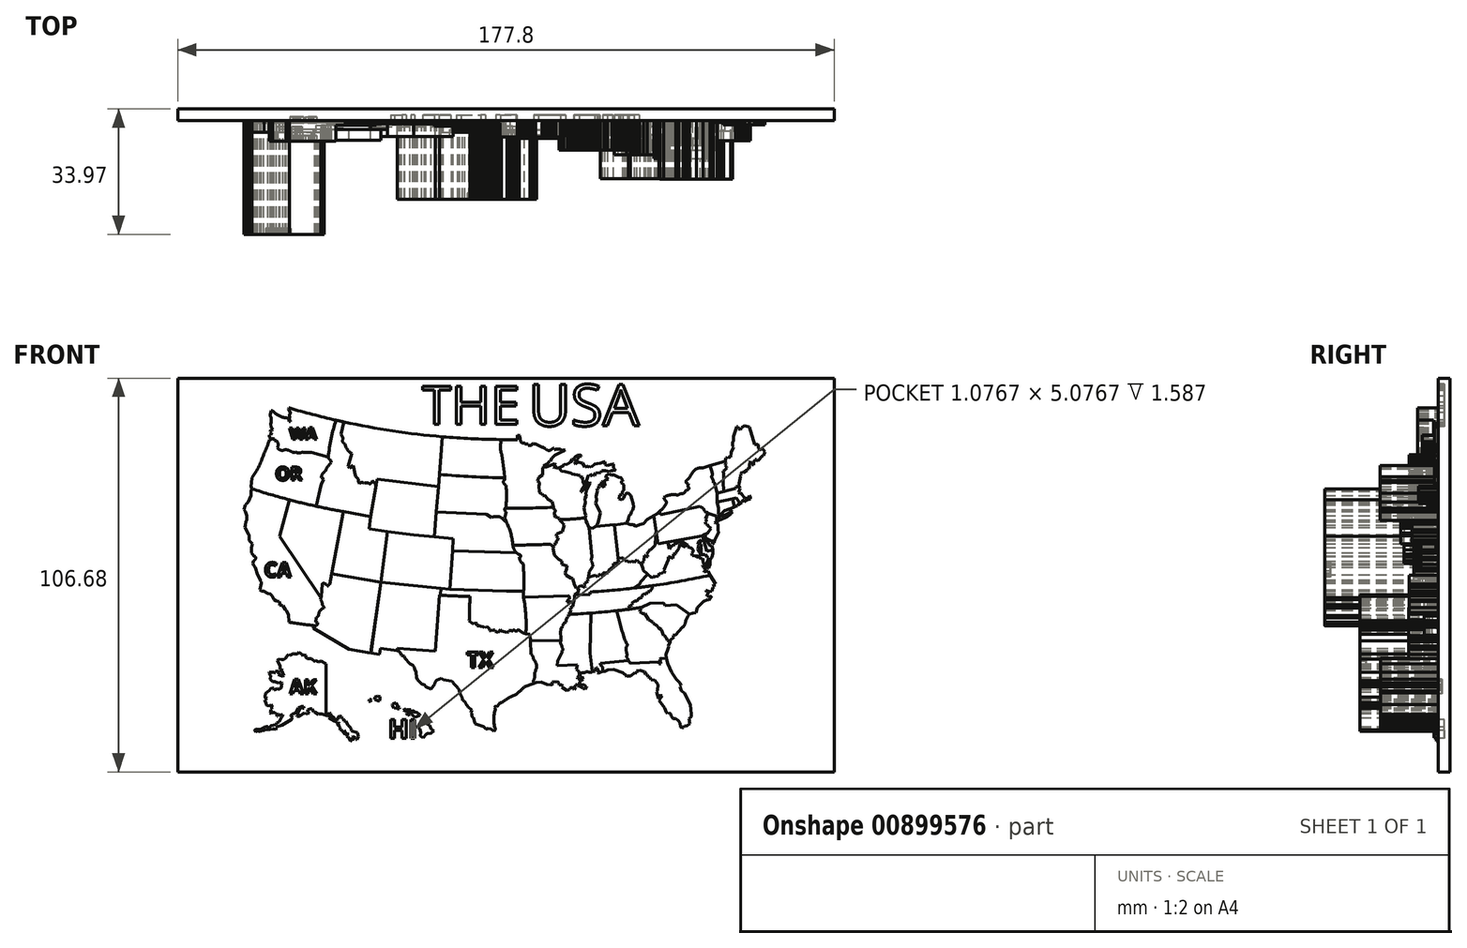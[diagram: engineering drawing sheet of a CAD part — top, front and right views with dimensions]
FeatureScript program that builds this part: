
annotation { "Feature Type Name" : "Feature", "Feature Type Description" : "" }
export const myFeature = defineFeature(function(context is Context, id is Id, definition is map)
    precondition{}
    {
        {
            var Q0;
            Q0=qCreatedBy(makeId("Front.planeOp"),FACE);
            var sketch = newSketch(context, id + "F0", { "sketchPlane" : qUnion([Q0])});
            skLineSegment(sketch, "E0.bottom", {"start": v(-88.8, 56.27) * mm, "end": v(89, 56.27) * mm});
            skLineSegment(sketch, "E0.top", {"start": v(-88.8, -50.4) * mm, "end": v(89, -50.4) * mm});
            skLineSegment(sketch, "E0.left", {"start": v(-88.8, 56.27) * mm, "end": v(-88.8, -50.4) * mm});
            skLineSegment(sketch, "E0.right", {"start": v(89, 56.27) * mm, "end": v(89, -50.4) * mm});
            skSolve(sketch);
        }
        {
            var Q0;
            Q0=qSketchRegion(id+"F0",true);
            extrude(context, id + "F1", {"entities" : qUnion([Q0]), "depth" : 3.17 * mm, "offsetDistance" : 25.4 * mm});
        }
        {
            var Q0;
            Q0=makeQuery(id+"F1.opExtrude","CAP_FACE",FACE,{"disambiguationData":[OSD([sQuery(id+"F0.wireOp",EDGE,"E0.bottom"),sQuery(id+"F0.wireOp",EDGE,"E0.top"),sQuery(id+"F0.wireOp",EDGE,"E0.left"),sQuery(id+"F0.wireOp",EDGE,"E0.right")])],"isStart":false});
            var sketch = newSketch(context, id + "F2", { "sketchPlane" : qUnion([Q0])});
            skLineSegment(sketch, "E1", {"start": v(-9.1, -34.54) * mm, "end": v(-9.38, -34.36) * mm});
            skLineSegment(sketch, "E2", {"start": v(-9.38, -34.36) * mm, "end": v(-9.15, -33.69) * mm});
            skLineSegment(sketch, "E3", {"start": v(-9.48, -33.25) * mm, "end": v(-9.15, -33.69) * mm});
            skLineSegment(sketch, "E4", {"start": v(-9.48, -33.25) * mm, "end": v(-9.93, -33.05) * mm});
            skArc(sketch, "E5", {"start": v(-11.02, -31.35) * mm, "mid": v(-10.52, -32.23) * mm, "end": v(-9.93, -33.05) * mm});
            skArc(sketch, "E6", {"start": v(-11.62, -30.95) * mm, "mid": v(-11.32, -31.15) * mm, "end": v(-11.02, -31.35) * mm});
            skArc(sketch, "E7", {"start": v(-11.62, -30.6) * mm, "mid": v(-11.62, -30.77) * mm, "end": v(-11.62, -30.95) * mm});
            skArc(sketch, "E8", {"start": v(-12.45, -28.74) * mm, "mid": v(-12.06, -29.68) * mm, "end": v(-11.62, -30.6) * mm});
            skArc(sketch, "E9", {"start": v(-12.57, -28.08) * mm, "mid": v(-12.72, -27.93) * mm, "end": v(-12.88, -27.8) * mm});
            skArc(sketch, "E10", {"start": v(-12.57, -28.08) * mm, "mid": v(-12.52, -28.41) * mm, "end": v(-12.45, -28.74) * mm});
            skLineSegment(sketch, "E11", {"start": v(-32.02, 14.71) * mm, "end": v(-33.75, 1.04) * mm});
            skLineSegment(sketch, "E12", {"start": v(-14.18, 12.88) * mm, "end": v(-14.4, 9.48) * mm});
            skLineSegment(sketch, "E13", {"start": v(-43.9, 20.13) * mm, "end": v(-36.59, 18.84) * mm});
            skLineSegment(sketch, "E14", {"start": v(-36.59, 18.84) * mm, "end": v(-36.99, 15.45) * mm});
            skLineSegment(sketch, "E15", {"start": v(-36.99, 15.45) * mm, "end": v(-32.02, 14.71) * mm});
            skLineSegment(sketch, "E16", {"start": v(-47.13, 3.28) * mm, "end": v(-43.9, 20.13) * mm});
            skArc(sketch, "E17", {"start": v(-68.66, 26.3) * mm, "mid": v(-56.39, 22.78) * mm, "end": v(-43.9, 20.13) * mm});
            skLineSegment(sketch, "E18", {"start": v(-61.22, 13.45) * mm, "end": v(-58.54, 23.33) * mm});
            skLineSegment(sketch, "E19", {"start": v(-61.22, 13.45) * mm, "end": v(-50.06, -3.17) * mm});
            skLineSegment(sketch, "E20", {"start": v(-36.59, 18.84) * mm, "end": v(-34.8, 28.96) * mm});
            skLineSegment(sketch, "E21", {"start": v(-18.19, 26.91) * mm, "end": v(-34.8, 28.96) * mm});
            skLineSegment(sketch, "E22", {"start": v(-19.02, -17.7) * mm, "end": v(-17.83, -2.47) * mm});
            skLineSegment(sketch, "E23", {"start": v(-17.83, -2.47) * mm, "end": v(-17.67, -2.48) * mm});
            skLineSegment(sketch, "E24", {"start": v(-17.67, -2.48) * mm, "end": v(-17.55, -0.7) * mm});
            skLineSegment(sketch, "E25", {"start": v(-36.49, -18.16) * mm, "end": v(-34.1, -18.5) * mm});
            skLineSegment(sketch, "E26", {"start": v(-34.1, -18.5) * mm, "end": v(-33.94, -16.9) * mm});
            skLineSegment(sketch, "E27", {"start": v(-33.94, -16.9) * mm, "end": v(-29.3, -17.55) * mm});
            skLineSegment(sketch, "E28", {"start": v(-29.3, -17.55) * mm, "end": v(-29.3, -16.9) * mm});
            skLineSegment(sketch, "E29", {"start": v(-29.3, -16.9) * mm, "end": v(-19.02, -17.7) * mm});
            skLineSegment(sketch, "E30", {"start": v(-52.08, -11.46) * mm, "end": v(-42.37, -17.2) * mm});
            skLineSegment(sketch, "E31", {"start": v(-42.37, -17.2) * mm, "end": v(-36.49, -18.16) * mm});
            skArc(sketch, "E32", {"start": v(-17.67, -2.48) * mm, "mid": v(-13.64, -2.72) * mm, "end": v(-9.6, -2.8) * mm});
            skArc(sketch, "E33", {"start": v(-9.6, -2.8) * mm, "mid": v(-9.75, -6.1) * mm, "end": v(-9.83, -9.42) * mm});
            skArc(sketch, "E34", {"start": v(-58.57, 48.22) * mm, "mid": v(-28.03, 41.65) * mm, "end": v(3.15, 39.65) * mm});
            skLineSegment(sketch, "E35", {"start": v(-18.19, 26.91) * mm, "end": v(-17.13, 40.43) * mm});
            skLineSegment(sketch, "E36", {"start": v(-18.72, 20.1) * mm, "end": v(-5.16, 19.43) * mm});
            skLineSegment(sketch, "E37", {"start": v(-14.4, 9.48) * mm, "end": v(2.98, 8.97) * mm});
            skArc(sketch, "E38", {"start": v(-0.16, 21.02) * mm, "mid": v(6.38, 21.09) * mm, "end": v(12.91, 21.3) * mm});
            skArc(sketch, "E39", {"start": v(1.99, 11.04) * mm, "mid": v(7.08, 11.14) * mm, "end": v(12.16, 11.34) * mm});
            skArc(sketch, "E40", {"start": v(14.65, 18.08) * mm, "mid": v(18.11, 18.12) * mm, "end": v(21.55, 18.48) * mm});
            skLineSegment(sketch, "E41", {"start": v(24.38, 16.11) * mm, "end": v(29.49, 16.69) * mm});
            skLineSegment(sketch, "E42", {"start": v(29.49, 16.69) * mm, "end": v(30.5, 7.53) * mm});
            skLineSegment(sketch, "E43", {"start": v(29.51, 16.46) * mm, "end": v(32.84, 16.98) * mm});
            skLineSegment(sketch, "E44", {"start": v(41.78, 20.28) * mm, "end": v(41.88, 19.31) * mm});
            skLineSegment(sketch, "E45", {"start": v(41.88, 19.31) * mm, "end": v(52.75, 21.52) * mm});
            skLineSegment(sketch, "E46", {"start": v(4.89, -1.39) * mm, "end": v(4.89, -3.06) * mm});
            skLineSegment(sketch, "E47", {"start": v(4.89, -3.06) * mm, "end": v(17.03, -2.65) * mm});
            skArc(sketch, "E48", {"start": v(4.89, -1.39) * mm, "mid": v(4.97, 2.33) * mm, "end": v(4.78, 6.05) * mm});
            skArc(sketch, "E49", {"start": v(-45.96, 44.93) * mm, "mid": v(-47.2, 40) * mm, "end": v(-48.05, 34.97) * mm});
            skArc(sketch, "E50", {"start": v(22.93, -1.62) * mm, "mid": v(39.24, 0) * mm, "end": v(55.38, 2.91) * mm});
            skLineSegment(sketch, "E51", {"start": v(18.72, -2.44) * mm, "end": v(22.88, -2.24) * mm});
            skLineSegment(sketch, "E52", {"start": v(22.88, -2.24) * mm, "end": v(22.93, -1.62) * mm});
            skArc(sketch, "E53", {"start": v(17.09, -7.7) * mm, "mid": v(26.93, -7.04) * mm, "end": v(36.73, -5.84) * mm});
            skLineSegment(sketch, "E54", {"start": v(6.77, -14.92) * mm, "end": v(14.99, -14.76) * mm});
            skLineSegment(sketch, "E55", {"start": v(-50.06, -3.17) * mm, "end": v(-49.84, -2.85) * mm});
            skLineSegment(sketch, "E56", {"start": v(-49.84, -2.85) * mm, "end": v(-49.7, 0.5) * mm});
            skArc(sketch, "E57", {"start": v(-49.19, 0.72) * mm, "mid": v(-49.46, 0.66) * mm, "end": v(-49.7, 0.5) * mm});
            skArc(sketch, "E58", {"start": v(-48.81, 0.5) * mm, "mid": v(-48.99, 0.64) * mm, "end": v(-49.19, 0.72) * mm});
            skArc(sketch, "E59", {"start": v(-48.55, 0.5) * mm, "mid": v(-48.68, 0.5) * mm, "end": v(-48.81, 0.5) * mm});
            skArc(sketch, "E60", {"start": v(-47.61, 0.5) * mm, "mid": v(-47.84, 0.3) * mm, "end": v(-48, 0.05) * mm});
            skArc(sketch, "E61", {"start": v(-48.34, 0.07) * mm, "mid": v(-48.42, 0.3) * mm, "end": v(-48.55, 0.5) * mm});
            skArc(sketch, "E62", {"start": v(-48.34, 0.07) * mm, "mid": v(-48.17, 0.03) * mm, "end": v(-48, 0.05) * mm});
            skLineSegment(sketch, "E63", {"start": v(-47.61, 0.5) * mm, "end": v(-47.13, 3.28) * mm});
            skArc(sketch, "E64", {"start": v(-58.69, -9.8) * mm, "mid": v(-55.2, -10.33) * mm, "end": v(-51.7, -10.77) * mm});
            skArc(sketch, "E65", {"start": v(-51.7, -10.77) * mm, "mid": v(-51.9, -11.1) * mm, "end": v(-52.08, -11.46) * mm});
            skLineSegment(sketch, "E66", {"start": v(-58.76, -7.76) * mm, "end": v(-58.69, -9.8) * mm});
            skLineSegment(sketch, "E67", {"start": v(-58.76, -7.76) * mm, "end": v(-59.36, -6.66) * mm});
            skLineSegment(sketch, "E68", {"start": v(-59.36, -6.66) * mm, "end": v(-59.68, -6.35) * mm});
            skLineSegment(sketch, "E69", {"start": v(-59.68, -6.35) * mm, "end": v(-60.33, -5.37) * mm});
            skLineSegment(sketch, "E70", {"start": v(-60.33, -5.37) * mm, "end": v(-61.25, -5.21) * mm});
            skLineSegment(sketch, "E71", {"start": v(-61.25, -5.21) * mm, "end": v(-61.25, -5.03) * mm});
            skLineSegment(sketch, "E72", {"start": v(-61.25, -5.03) * mm, "end": v(-61.11, -4.93) * mm});
            skLineSegment(sketch, "E73", {"start": v(-61.11, -4.93) * mm, "end": v(-61.17, -4.47) * mm});
            skLineSegment(sketch, "E74", {"start": v(-61.17, -4.47) * mm, "end": v(-61.38, -4.15) * mm});
            skLineSegment(sketch, "E75", {"start": v(-61.38, -4.15) * mm, "end": v(-62.13, -4.01) * mm});
            skLineSegment(sketch, "E76", {"start": v(-62.13, -4.01) * mm, "end": v(-62.7, -3.72) * mm});
            skLineSegment(sketch, "E77", {"start": v(-62.7, -3.72) * mm, "end": v(-63.29, -2.67) * mm});
            skLineSegment(sketch, "E78", {"start": v(-63.29, -2.67) * mm, "end": v(-63.76, -2.12) * mm});
            skLineSegment(sketch, "E79", {"start": v(-63.76, -2.12) * mm, "end": v(-64.32, -2.05) * mm});
            skLineSegment(sketch, "E80", {"start": v(-64.32, -2.05) * mm, "end": v(-65.53, -1.47) * mm});
            skLineSegment(sketch, "E81", {"start": v(-65.53, -1.47) * mm, "end": v(-66.13, -1.4) * mm});
            skLineSegment(sketch, "E82", {"start": v(-66.13, -1.4) * mm, "end": v(-66.55, -0.98) * mm});
            skLineSegment(sketch, "E83", {"start": v(-66.55, -0.98) * mm, "end": v(-66.13, 0.75) * mm});
            skLineSegment(sketch, "E84", {"start": v(-66.13, 0.75) * mm, "end": v(-66.13, 1.1) * mm});
            skLineSegment(sketch, "E85", {"start": v(-66.13, 1.1) * mm, "end": v(-66.37, 1.3) * mm});
            skLineSegment(sketch, "E86", {"start": v(-66.37, 1.3) * mm, "end": v(-66.37, 1.68) * mm});
            skLineSegment(sketch, "E87", {"start": v(-66.37, 1.68) * mm, "end": v(-67.18, 3.06) * mm});
            skLineSegment(sketch, "E88", {"start": v(-67.18, 3.06) * mm, "end": v(-67.82, 5.01) * mm});
            skLineSegment(sketch, "E89", {"start": v(-67.82, 5.01) * mm, "end": v(-68.25, 5.66) * mm});
            skLineSegment(sketch, "E90", {"start": v(-68.25, 5.66) * mm, "end": v(-68.4, 6.07) * mm});
            skLineSegment(sketch, "E91", {"start": v(-68.4, 6.07) * mm, "end": v(-68.3, 6.77) * mm});
            skArc(sketch, "E92", {"start": v(-68.3, 6.77) * mm, "mid": v(-67.74, 7.25) * mm, "end": v(-67.78, 7.99) * mm});
            skLineSegment(sketch, "E93", {"start": v(-67.78, 7.99) * mm, "end": v(-68.16, 8.08) * mm});
            skLineSegment(sketch, "E94", {"start": v(-68.16, 8.08) * mm, "end": v(-68.84, 9.03) * mm});
            skLineSegment(sketch, "E95", {"start": v(-68.84, 9.03) * mm, "end": v(-68.84, 10.39) * mm});
            skLineSegment(sketch, "E96", {"start": v(-68.84, 10.39) * mm, "end": v(-68.6, 11.38) * mm});
            skLineSegment(sketch, "E97", {"start": v(-68.6, 11.38) * mm, "end": v(-69.44, 12.35) * mm});
            skLineSegment(sketch, "E98", {"start": v(-69.44, 12.35) * mm, "end": v(-69.44, 12.72) * mm});
            skArc(sketch, "E99", {"start": v(-69.44, 12.72) * mm, "mid": v(-69.4, 13.38) * mm, "end": v(-69.61, 14.02) * mm});
            skLineSegment(sketch, "E100", {"start": v(-70.6, 15.92) * mm, "end": v(-69.61, 14.02) * mm});
            skLineSegment(sketch, "E101", {"start": v(-70.6, 15.92) * mm, "end": v(-70.44, 16.52) * mm});
            skLineSegment(sketch, "E102", {"start": v(-70.44, 16.52) * mm, "end": v(-70.37, 17.42) * mm});
            skLineSegment(sketch, "E103", {"start": v(-70.37, 17.42) * mm, "end": v(-70.09, 17.87) * mm});
            skLineSegment(sketch, "E104", {"start": v(-70.09, 17.87) * mm, "end": v(-70.04, 19) * mm});
            skLineSegment(sketch, "E105", {"start": v(-70.04, 19) * mm, "end": v(-70.44, 20.15) * mm});
            skLineSegment(sketch, "E106", {"start": v(-70.44, 20.15) * mm, "end": v(-70.87, 20.73) * mm});
            skLineSegment(sketch, "E107", {"start": v(-70.87, 20.73) * mm, "end": v(-70.52, 21.95) * mm});
            skLineSegment(sketch, "E108", {"start": v(-70.52, 21.95) * mm, "end": v(-70.25, 22.03) * mm});
            skLineSegment(sketch, "E109", {"start": v(-70.25, 22.03) * mm, "end": v(-70.2, 22.25) * mm});
            skLineSegment(sketch, "E110", {"start": v(-70.2, 22.25) * mm, "end": v(-69.73, 22.67) * mm});
            skLineSegment(sketch, "E111", {"start": v(-69.73, 22.67) * mm, "end": v(-68.92, 24.45) * mm});
            skLineSegment(sketch, "E112", {"start": v(-68.92, 24.45) * mm, "end": v(-68.92, 25.63) * mm});
            skLineSegment(sketch, "E113", {"start": v(-68.92, 25.63) * mm, "end": v(-68.66, 26.3) * mm});
            skArc(sketch, "E114", {"start": v(-49.62, -5.14) * mm, "mid": v(-49.75, -4.4) * mm, "end": v(-50.12, -3.72) * mm});
            skLineSegment(sketch, "E115", {"start": v(-50.06, -3.17) * mm, "end": v(-50.12, -3.72) * mm});
            skArc(sketch, "E116", {"start": v(-51.7, -10.77) * mm, "mid": v(-51.06, -10.59) * mm, "end": v(-50.91, -9.95) * mm});
            skLineSegment(sketch, "E117", {"start": v(-50.91, -9.95) * mm, "end": v(-51.41, -9.83) * mm});
            skLineSegment(sketch, "E118", {"start": v(-51.41, -9.83) * mm, "end": v(-51.35, -8.59) * mm});
            skArc(sketch, "E119", {"start": v(-51.35, -8.59) * mm, "mid": v(-50.95, -8.36) * mm, "end": v(-50.63, -8.02) * mm});
            skArc(sketch, "E120", {"start": v(-49.17, -5.94) * mm, "mid": v(-50.25, -6.73) * mm, "end": v(-50.63, -8.02) * mm});
            skArc(sketch, "E121", {"start": v(-49.17, -5.94) * mm, "mid": v(-49.33, -5.5) * mm, "end": v(-49.62, -5.14) * mm});
            skLineSegment(sketch, "E122", {"start": v(-51.27, 21.59) * mm, "end": v(-49.84, 27.7) * mm});
            skLineSegment(sketch, "E123", {"start": v(-49.84, 27.7) * mm, "end": v(-49.3, 28.86) * mm});
            skLineSegment(sketch, "E124", {"start": v(-49.3, 28.86) * mm, "end": v(-49.46, 29.22) * mm});
            skLineSegment(sketch, "E125", {"start": v(-49.46, 29.22) * mm, "end": v(-49.9, 29.33) * mm});
            skLineSegment(sketch, "E126", {"start": v(-48.05, 34.97) * mm, "end": v(-52.51, 36.15) * mm});
            skLineSegment(sketch, "E127", {"start": v(-52.51, 36.15) * mm, "end": v(-54.88, 36.15) * mm});
            skLineSegment(sketch, "E128", {"start": v(-54.88, 36.15) * mm, "end": v(-54.88, 36.33) * mm});
            skLineSegment(sketch, "E129", {"start": v(-54.88, 36.33) * mm, "end": v(-55.67, 36.03) * mm});
            skLineSegment(sketch, "E130", {"start": v(-55.67, 36.03) * mm, "end": v(-56.35, 36.03) * mm});
            skLineSegment(sketch, "E131", {"start": v(-56.35, 36.03) * mm, "end": v(-56.82, 36.36) * mm});
            skLineSegment(sketch, "E132", {"start": v(-56.82, 36.36) * mm, "end": v(-57.02, 36.24) * mm});
            skLineSegment(sketch, "E133", {"start": v(-57.02, 36.24) * mm, "end": v(-57.71, 36.24) * mm});
            skArc(sketch, "E134", {"start": v(-57.71, 36.24) * mm, "mid": v(-58.63, 36.7) * mm, "end": v(-59.61, 36.98) * mm});
            skArc(sketch, "E135", {"start": v(-61.79, 37.4) * mm, "mid": v(-60.78, 36.77) * mm, "end": v(-59.61, 36.98) * mm});
            skArc(sketch, "E136", {"start": v(-61.79, 37.4) * mm, "mid": v(-61.62, 38.43) * mm, "end": v(-62.05, 39.38) * mm});
            skLineSegment(sketch, "E137", {"start": v(-62.05, 39.38) * mm, "end": v(-62.63, 39.38) * mm});
            skLineSegment(sketch, "E138", {"start": v(-62.63, 39.38) * mm, "end": v(-62.63, 39.8) * mm});
            skLineSegment(sketch, "E139", {"start": v(-62.63, 39.8) * mm, "end": v(-62.98, 39.8) * mm});
            skLineSegment(sketch, "E140", {"start": v(-62.98, 39.8) * mm, "end": v(-63.4, 40.12) * mm});
            skLineSegment(sketch, "E141", {"start": v(-63.4, 40.12) * mm, "end": v(-63.66, 40.01) * mm});
            skLineSegment(sketch, "E142", {"start": v(-63.66, 40.01) * mm, "end": v(-64.02, 40.43) * mm});
            skLineSegment(sketch, "E143", {"start": v(-64.02, 40.43) * mm, "end": v(-63.96, 40.89) * mm});
            skLineSegment(sketch, "E144", {"start": v(-63.96, 40.89) * mm, "end": v(-63.56, 40.89) * mm});
            skLineSegment(sketch, "E145", {"start": v(-63.56, 40.89) * mm, "end": v(-63.31, 41.55) * mm});
            skLineSegment(sketch, "E146", {"start": v(-63.31, 41.55) * mm, "end": v(-63.7, 41.75) * mm});
            skLineSegment(sketch, "E147", {"start": v(-63.7, 41.75) * mm, "end": v(-63.64, 42.3) * mm});
            skLineSegment(sketch, "E148", {"start": v(-63.64, 42.3) * mm, "end": v(-62.94, 42.37) * mm});
            skLineSegment(sketch, "E149", {"start": v(-62.94, 42.37) * mm, "end": v(-63.43, 42.86) * mm});
            skLineSegment(sketch, "E150", {"start": v(-63.43, 42.86) * mm, "end": v(-63.63, 43.93) * mm});
            skLineSegment(sketch, "E151", {"start": v(-63.63, 43.93) * mm, "end": v(-63.53, 44.29) * mm});
            skLineSegment(sketch, "E152", {"start": v(-63.53, 44.29) * mm, "end": v(-63.53, 45.61) * mm});
            skLineSegment(sketch, "E153", {"start": v(-63.53, 45.61) * mm, "end": v(-63.8, 46.06) * mm});
            skLineSegment(sketch, "E154", {"start": v(-63.8, 46.06) * mm, "end": v(-63.8, 46.32) * mm});
            skLineSegment(sketch, "E155", {"start": v(-63.8, 46.32) * mm, "end": v(-63.5, 47.54) * mm});
            skLineSegment(sketch, "E156", {"start": v(-63.5, 47.54) * mm, "end": v(-63.15, 47.5) * mm});
            skArc(sketch, "E157", {"start": v(-63.15, 47.5) * mm, "mid": v(-61.45, 46.16) * mm, "end": v(-59.37, 45.54) * mm});
            skArc(sketch, "E158", {"start": v(-58.6, 44.6) * mm, "mid": v(-58.84, 45.18) * mm, "end": v(-59.37, 45.54) * mm});
            skArc(sketch, "E159", {"start": v(-58.43, 45.74) * mm, "mid": v(-58.55, 45.28) * mm, "end": v(-58.33, 44.85) * mm});
            skArc(sketch, "E160", {"start": v(-58.27, 46.84) * mm, "mid": v(-58.51, 46.32) * mm, "end": v(-58.43, 45.74) * mm});
            skLineSegment(sketch, "E161", {"start": v(-58.33, 44.85) * mm, "end": v(-58.33, 44.58) * mm});
            skLineSegment(sketch, "E162", {"start": v(-58.33, 44.58) * mm, "end": v(-58.6, 44.6) * mm});
            skLineSegment(sketch, "E163", {"start": v(-58.27, 46.84) * mm, "end": v(-58.75, 47.98) * mm});
            skLineSegment(sketch, "E164", {"start": v(-58.75, 47.98) * mm, "end": v(-58.67, 48.22) * mm});
            skLineSegment(sketch, "E165", {"start": v(-58.67, 48.22) * mm, "end": v(-58.57, 48.22) * mm});
            skArc(sketch, "E166", {"start": v(-48.84, 31.04) * mm, "mid": v(-49.61, 30.33) * mm, "end": v(-49.9, 29.33) * mm});
            skArc(sketch, "E167", {"start": v(-48.84, 31.04) * mm, "mid": v(-48.7, 31.33) * mm, "end": v(-48.66, 31.66) * mm});
            skArc(sketch, "E168", {"start": v(-47.26, 33.37) * mm, "mid": v(-48, 32.54) * mm, "end": v(-48.66, 31.66) * mm});
            skArc(sketch, "E169", {"start": v(-48.05, 34.97) * mm, "mid": v(-47.81, 34.4) * mm, "end": v(-47.35, 34) * mm});
            skLineSegment(sketch, "E170", {"start": v(-47.35, 34) * mm, "end": v(-47.26, 33.37) * mm});
            skArc(sketch, "E171", {"start": v(41.78, 20.28) * mm, "mid": v(42.8, 21.26) * mm, "end": v(43.6, 22.45) * mm});
            skArc(sketch, "E172", {"start": v(42.87, 24) * mm, "mid": v(43, 23.62) * mm, "end": v(43.15, 23.24) * mm});
            skArc(sketch, "E173", {"start": v(43.6, 22.45) * mm, "mid": v(43.5, 22.92) * mm, "end": v(43.15, 23.24) * mm});
            skArc(sketch, "E174", {"start": v(46.14, 24.74) * mm, "mid": v(44.44, 24.63) * mm, "end": v(42.87, 24) * mm});
            skArc(sketch, "E175", {"start": v(46.14, 24.74) * mm, "mid": v(46.51, 24.58) * mm, "end": v(46.88, 24.74) * mm});
            skArc(sketch, "E176", {"start": v(48.13, 24.97) * mm, "mid": v(47.48, 24.97) * mm, "end": v(46.88, 24.74) * mm});
            skArc(sketch, "E177", {"start": v(48.13, 24.97) * mm, "mid": v(48.6, 25.5) * mm, "end": v(49.04, 26.06) * mm});
            skArc(sketch, "E178", {"start": v(49.04, 26.06) * mm, "mid": v(49.61, 26.3) * mm, "end": v(49.4, 26.88) * mm});
            skArc(sketch, "E179", {"start": v(49.6, 27.7) * mm, "mid": v(49.44, 27.3) * mm, "end": v(49.4, 26.88) * mm});
            skArc(sketch, "E180", {"start": v(49.31, 28.84) * mm, "mid": v(48.9, 28.13) * mm, "end": v(49.6, 27.7) * mm});
            skArc(sketch, "E181", {"start": v(49.31, 28.84) * mm, "mid": v(49.58, 29.08) * mm, "end": v(49.8, 29.36) * mm});
            skArc(sketch, "E182", {"start": v(51.65, 31.73) * mm, "mid": v(50.6, 30.65) * mm, "end": v(49.8, 29.36) * mm});
            skArc(sketch, "E183", {"start": v(52.75, 21.52) * mm, "mid": v(53.14, 21.22) * mm, "end": v(53.62, 21.08) * mm});
            skArc(sketch, "E184", {"start": v(53.62, 21.08) * mm, "mid": v(53.82, 20.47) * mm, "end": v(54.23, 19.96) * mm});
            skArc(sketch, "E185", {"start": v(54.9, 19.66) * mm, "mid": v(54.62, 19.94) * mm, "end": v(54.23, 19.96) * mm});
            skLineSegment(sketch, "E186", {"start": v(54.9, 19.66) * mm, "end": v(57.2, 18.95) * mm});
            skLineSegment(sketch, "E187", {"start": v(57.2, 18.95) * mm, "end": v(57.2, 17.71) * mm});
            skArc(sketch, "E188", {"start": v(57.2, 17.71) * mm, "mid": v(59.56, 18.49) * mm, "end": v(61.5, 20.05) * mm});
            skLineSegment(sketch, "E189", {"start": v(61.5, 20.05) * mm, "end": v(60.92, 20.3) * mm});
            skArc(sketch, "E190", {"start": v(59.08, 19.13) * mm, "mid": v(60.1, 19.57) * mm, "end": v(60.92, 20.3) * mm});
            skArc(sketch, "E191", {"start": v(58.47, 19.13) * mm, "mid": v(58.78, 19.07) * mm, "end": v(59.08, 19.13) * mm});
            skLineSegment(sketch, "E192", {"start": v(58.47, 19.13) * mm, "end": v(57.77, 18.52) * mm});
            skLineSegment(sketch, "E193", {"start": v(57.77, 18.52) * mm, "end": v(57.5, 18.45) * mm});
            skLineSegment(sketch, "E194", {"start": v(57.5, 18.45) * mm, "end": v(57.5, 18.65) * mm});
            skLineSegment(sketch, "E195", {"start": v(57.5, 18.65) * mm, "end": v(57.78, 18.95) * mm});
            skLineSegment(sketch, "E196", {"start": v(57.78, 18.95) * mm, "end": v(57.78, 19.2) * mm});
            skLineSegment(sketch, "E197", {"start": v(57.78, 19.2) * mm, "end": v(57.49, 19.47) * mm});
            skLineSegment(sketch, "E198", {"start": v(57.49, 19.47) * mm, "end": v(57.67, 19.67) * mm});
            skLineSegment(sketch, "E199", {"start": v(57.67, 19.67) * mm, "end": v(57.67, 21.09) * mm});
            skLineSegment(sketch, "E200", {"start": v(57.67, 21.09) * mm, "end": v(57.28, 22.73) * mm});
            skLineSegment(sketch, "E201", {"start": v(57.28, 22.73) * mm, "end": v(57.28, 25.2) * mm});
            skLineSegment(sketch, "E202", {"start": v(57.28, 25.2) * mm, "end": v(56.71, 27.8) * mm});
            skArc(sketch, "E203", {"start": v(56.71, 27.8) * mm, "mid": v(56.5, 28) * mm, "end": v(56.24, 27.88) * mm});
            skArc(sketch, "E204", {"start": v(53.5, 32.05) * mm, "mid": v(52.56, 31.97) * mm, "end": v(51.65, 31.73) * mm});
            skLineSegment(sketch, "E205", {"start": v(53.5, 32.05) * mm, "end": v(55.36, 32.56) * mm});
            skLineSegment(sketch, "E206", {"start": v(55.36, 32.56) * mm, "end": v(55.96, 30.42) * mm});
            skArc(sketch, "E207", {"start": v(55.76, 29.55) * mm, "mid": v(55.97, 29.96) * mm, "end": v(55.96, 30.42) * mm});
            skLineSegment(sketch, "E208", {"start": v(55.76, 29.55) * mm, "end": v(56.3, 28.53) * mm});
            skLineSegment(sketch, "E209", {"start": v(56.3, 28.53) * mm, "end": v(56.24, 27.88) * mm});
            skLineSegment(sketch, "E210", {"start": v(-68.66, 26.3) * mm, "end": v(-69, 27) * mm});
            skLineSegment(sketch, "E211", {"start": v(-69, 27) * mm, "end": v(-68.78, 27.95) * mm});
            skLineSegment(sketch, "E212", {"start": v(-68.78, 27.95) * mm, "end": v(-68.69, 29.3) * mm});
            skArc(sketch, "E213", {"start": v(-68.69, 29.3) * mm, "mid": v(-66.76, 32.51) * mm, "end": v(-65.4, 36) * mm});
            skLineSegment(sketch, "E214", {"start": v(-62.98, 39.8) * mm, "end": v(-63.97, 39.58) * mm});
            skArc(sketch, "E215", {"start": v(-65.4, 36) * mm, "mid": v(-64.6, 37.76) * mm, "end": v(-63.97, 39.58) * mm});
            skLineSegment(sketch, "E216", {"start": v(-5.16, 19.43) * mm, "end": v(-3.85, 18.56) * mm});
            skArc(sketch, "E217", {"start": v(-0.64, 18.14) * mm, "mid": v(-2.18, 18.8) * mm, "end": v(-3.85, 18.56) * mm});
            skArc(sketch, "E218", {"start": v(-0.64, 18.14) * mm, "mid": v(-0.37, 17.68) * mm, "end": v(0.14, 17.53) * mm});
            skArc(sketch, "E219", {"start": v(1.99, 11.04) * mm, "mid": v(1.38, 14.38) * mm, "end": v(0.14, 17.53) * mm});
            skArc(sketch, "E220", {"start": v(1.99, 11.04) * mm, "mid": v(2.32, 9.92) * mm, "end": v(2.98, 8.97) * mm});
            skArc(sketch, "E221", {"start": v(2.98, 8.97) * mm, "mid": v(3.44, 8.62) * mm, "end": v(3.99, 8.44) * mm});
            skArc(sketch, "E222", {"start": v(3.76, 7.68) * mm, "mid": v(4.1, 8) * mm, "end": v(3.99, 8.44) * mm});
            skArc(sketch, "E223", {"start": v(3.76, 7.68) * mm, "mid": v(4.03, 6.72) * mm, "end": v(4.78, 6.05) * mm});
            skLineSegment(sketch, "E224", {"start": v(-43.85, 44.46) * mm, "end": v(-44.52, 41.17) * mm});
            skLineSegment(sketch, "E225", {"start": v(-44.52, 41.17) * mm, "end": v(-44.01, 40.13) * mm});
            skLineSegment(sketch, "E226", {"start": v(-44.01, 40.13) * mm, "end": v(-44.17, 39.13) * mm});
            skArc(sketch, "E227", {"start": v(-44.17, 39.13) * mm, "mid": v(-43.87, 38.72) * mm, "end": v(-43.45, 38.46) * mm});
            skArc(sketch, "E228", {"start": v(-43.45, 38.46) * mm, "mid": v(-42.84, 36.95) * mm, "end": v(-41.6, 35.9) * mm});
            skLineSegment(sketch, "E229", {"start": v(-42.68, 32.35) * mm, "end": v(-41.6, 35.9) * mm});
            skLineSegment(sketch, "E230", {"start": v(-42.22, 31.95) * mm, "end": v(-42.68, 32.35) * mm});
            skLineSegment(sketch, "E231", {"start": v(-39.88, 28.95) * mm, "end": v(-40.63, 29.7) * mm});
            skLineSegment(sketch, "E232", {"start": v(-40.63, 29.7) * mm, "end": v(-41.21, 32.58) * mm});
            skLineSegment(sketch, "E233", {"start": v(-41.21, 32.58) * mm, "end": v(-42.22, 31.95) * mm});
            skArc(sketch, "E234", {"start": v(-39.88, 28.95) * mm, "mid": v(-39.84, 28.28) * mm, "end": v(-39.57, 27.67) * mm});
            skArc(sketch, "E235", {"start": v(-38.36, 27.82) * mm, "mid": v(-39, 28.06) * mm, "end": v(-39.57, 27.67) * mm});
            skArc(sketch, "E236", {"start": v(-36.82, 27.67) * mm, "mid": v(-37.56, 27.98) * mm, "end": v(-38.36, 27.82) * mm});
            skArc(sketch, "E237", {"start": v(-36.82, 27.67) * mm, "mid": v(-36.42, 27.84) * mm, "end": v(-36.25, 28.24) * mm});
            skArc(sketch, "E238", {"start": v(-35.66, 28.22) * mm, "mid": v(-35.46, 27.73) * mm, "end": v(-35.1, 27.36) * mm});
            skArc(sketch, "E239", {"start": v(-35.66, 28.22) * mm, "mid": v(-35.95, 28.3) * mm, "end": v(-36.25, 28.24) * mm});
            skArc(sketch, "E240", {"start": v(5.5, -12.94) * mm, "mid": v(5.5, -7.98) * mm, "end": v(4.89, -3.06) * mm});
            skLineSegment(sketch, "E241", {"start": v(5.5, -12.94) * mm, "end": v(6.68, -13.15) * mm});
            skLineSegment(sketch, "E242", {"start": v(6.68, -13.15) * mm, "end": v(6.77, -14.92) * mm});
            skLineSegment(sketch, "E243", {"start": v(6.77, -14.92) * mm, "end": v(6.84, -18.48) * mm});
            skLineSegment(sketch, "E244", {"start": v(-9.1, -34.54) * mm, "end": v(-9.1, -35.16) * mm});
            skArc(sketch, "E245", {"start": v(-9.1, -35.16) * mm, "mid": v(-8.97, -35.54) * mm, "end": v(-8.63, -35.76) * mm});
            skArc(sketch, "E246", {"start": v(-8.63, -35.76) * mm, "mid": v(-8.47, -36.57) * mm, "end": v(-8.21, -37.36) * mm});
            skLineSegment(sketch, "E247", {"start": v(-2.72, -39.03) * mm, "end": v(-3.16, -39.35) * mm});
            skLineSegment(sketch, "E248", {"start": v(-3.16, -39.35) * mm, "end": v(-3.9, -38.77) * mm});
            skLineSegment(sketch, "E249", {"start": v(-3.9, -38.77) * mm, "end": v(-4.76, -38.63) * mm});
            skLineSegment(sketch, "E250", {"start": v(-4.76, -38.63) * mm, "end": v(-5.09, -38.73) * mm});
            skLineSegment(sketch, "E251", {"start": v(-5.09, -38.73) * mm, "end": v(-5.36, -38.75) * mm});
            skLineSegment(sketch, "E252", {"start": v(-5.36, -38.75) * mm, "end": v(-6.01, -38.15) * mm});
            skLineSegment(sketch, "E253", {"start": v(-6.01, -38.15) * mm, "end": v(-8.21, -37.36) * mm});
            skLineSegment(sketch, "E254", {"start": v(18.4, -4.3) * mm, "end": v(16.66, -4.3) * mm});
            skArc(sketch, "E255", {"start": v(17.32, -3.48) * mm, "mid": v(16.92, -3.83) * mm, "end": v(16.66, -4.3) * mm});
            skArc(sketch, "E256", {"start": v(17.32, -3.48) * mm, "mid": v(17.3, -3.03) * mm, "end": v(17.03, -2.65) * mm});
            skLineSegment(sketch, "E257", {"start": v(0.14, 17.53) * mm, "end": v(-0.28, 18.36) * mm});
            skLineSegment(sketch, "E258", {"start": v(-0.28, 18.36) * mm, "end": v(0.14, 19.94) * mm});
            skArc(sketch, "E259", {"start": v(-0.16, 21.02) * mm, "mid": v(-0.17, 20.43) * mm, "end": v(0.14, 19.94) * mm});
            skArc(sketch, "E260", {"start": v(-17.93, 30.24) * mm, "mid": v(-9.08, 29.6) * mm, "end": v(-0.22, 29.29) * mm});
            skArc(sketch, "E261", {"start": v(0.14, 21.02) * mm, "mid": v(0.24, 24.11) * mm, "end": v(0.18, 27.2) * mm});
            skArc(sketch, "E262", {"start": v(-0.69, 28.38) * mm, "mid": v(-0.27, 28.74) * mm, "end": v(-0.22, 29.29) * mm});
            skArc(sketch, "E263", {"start": v(-0.69, 28.38) * mm, "mid": v(-0.4, 27.68) * mm, "end": v(0.18, 27.2) * mm});
            skArc(sketch, "E264", {"start": v(-1.32, 38.54) * mm, "mid": v(-1.3, 39.13) * mm, "end": v(-1.56, 39.66) * mm});
            skArc(sketch, "E265", {"start": v(-1.32, 38.54) * mm, "mid": v(-1.36, 36.95) * mm, "end": v(-0.94, 35.43) * mm});
            skLineSegment(sketch, "E266", {"start": v(-0.94, 35.43) * mm, "end": v(-0.31, 30.87) * mm});
            skLineSegment(sketch, "E267", {"start": v(-0.31, 30.87) * mm, "end": v(-0.22, 29.29) * mm});
            skArc(sketch, "E268", {"start": v(7.55, -19.87) * mm, "mid": v(7.39, -19.08) * mm, "end": v(6.84, -18.48) * mm});
            skArc(sketch, "E269", {"start": v(7.83, -23.41) * mm, "mid": v(8.38, -21.59) * mm, "end": v(7.55, -19.87) * mm});
            skArc(sketch, "E270", {"start": v(7.55, -25.7) * mm, "mid": v(7.9, -24.58) * mm, "end": v(7.83, -23.41) * mm});
            skLineSegment(sketch, "E271", {"start": v(7.55, -25.7) * mm, "end": v(7.69, -26.38) * mm});
            skLineSegment(sketch, "E272", {"start": v(7.69, -26.38) * mm, "end": v(5.12, -27.3) * mm});
            skArc(sketch, "E273", {"start": v(1.3, -30.14) * mm, "mid": v(3.38, -28.96) * mm, "end": v(5.12, -27.3) * mm});
            skArc(sketch, "E274", {"start": v(1.3, -30.14) * mm, "mid": v(0.1, -30.82) * mm, "end": v(-1.03, -31.62) * mm});
            skArc(sketch, "E275", {"start": v(-2.72, -33.22) * mm, "mid": v(-3.2, -36.12) * mm, "end": v(-2.72, -39.03) * mm});
            skLineSegment(sketch, "E276", {"start": v(-1.03, -31.62) * mm, "end": v(-1.54, -31.62) * mm});
            skLineSegment(sketch, "E277", {"start": v(-1.54, -31.62) * mm, "end": v(-2.18, -32.56) * mm});
            skLineSegment(sketch, "E278", {"start": v(-2.18, -32.56) * mm, "end": v(-2.8, -32.62) * mm});
            skLineSegment(sketch, "E279", {"start": v(-2.8, -32.62) * mm, "end": v(-2.98, -32.94) * mm});
            skLineSegment(sketch, "E280", {"start": v(-2.98, -32.94) * mm, "end": v(-2.72, -33.22) * mm});
            skLineSegment(sketch, "E281", {"start": v(-12.88, -27.8) * mm, "end": v(-12.88, -27.57) * mm});
            skLineSegment(sketch, "E282", {"start": v(-12.88, -27.57) * mm, "end": v(-14.17, -26.32) * mm});
            skLineSegment(sketch, "E283", {"start": v(-14.17, -26.32) * mm, "end": v(-14.17, -26.08) * mm});
            skLineSegment(sketch, "E284", {"start": v(-14.17, -26.08) * mm, "end": v(-14.61, -25.74) * mm});
            skLineSegment(sketch, "E285", {"start": v(-14.61, -25.74) * mm, "end": v(-16.86, -25.47) * mm});
            skLineSegment(sketch, "E286", {"start": v(-16.86, -25.47) * mm, "end": v(-17.34, -25.08) * mm});
            skLineSegment(sketch, "E287", {"start": v(-17.34, -25.08) * mm, "end": v(-18.65, -25.6) * mm});
            skLineSegment(sketch, "E288", {"start": v(-18.65, -25.6) * mm, "end": v(-19.1, -26.16) * mm});
            skLineSegment(sketch, "E289", {"start": v(-19.1, -26.16) * mm, "end": v(-19.15, -26.6) * mm});
            skLineSegment(sketch, "E290", {"start": v(-19.15, -26.6) * mm, "end": v(-20.13, -27.91) * mm});
            skLineSegment(sketch, "E291", {"start": v(-20.13, -27.91) * mm, "end": v(-21.58, -27.33) * mm});
            skLineSegment(sketch, "E292", {"start": v(-21.58, -27.33) * mm, "end": v(-21.93, -26.85) * mm});
            skLineSegment(sketch, "E293", {"start": v(-21.93, -26.85) * mm, "end": v(-22.74, -26.5) * mm});
            skLineSegment(sketch, "E294", {"start": v(-22.74, -26.5) * mm, "end": v(-23.81, -25.36) * mm});
            skLineSegment(sketch, "E295", {"start": v(-23.81, -25.36) * mm, "end": v(-24.16, -24.75) * mm});
            skLineSegment(sketch, "E296", {"start": v(-24.16, -24.75) * mm, "end": v(-24.2, -23.32) * mm});
            skLineSegment(sketch, "E297", {"start": v(-24.2, -23.32) * mm, "end": v(-24.67, -22.45) * mm});
            skLineSegment(sketch, "E298", {"start": v(-24.67, -22.45) * mm, "end": v(-24.77, -21.92) * mm});
            skLineSegment(sketch, "E299", {"start": v(-24.77, -21.92) * mm, "end": v(-25.17, -21.52) * mm});
            skLineSegment(sketch, "E300", {"start": v(-25.17, -21.52) * mm, "end": v(-25.9, -21.15) * mm});
            skLineSegment(sketch, "E301", {"start": v(-25.9, -21.15) * mm, "end": v(-27.27, -19.57) * mm});
            skLineSegment(sketch, "E302", {"start": v(-27.27, -19.57) * mm, "end": v(-27.46, -19.12) * mm});
            skLineSegment(sketch, "E303", {"start": v(-27.46, -19.12) * mm, "end": v(-28.12, -18.82) * mm});
            skLineSegment(sketch, "E304", {"start": v(-28.12, -18.82) * mm, "end": v(-28.37, -18.17) * mm});
            skLineSegment(sketch, "E305", {"start": v(-28.37, -18.17) * mm, "end": v(-28.88, -17.64) * mm});
            skLineSegment(sketch, "E306", {"start": v(-28.88, -17.64) * mm, "end": v(-29.3, -17.55) * mm});
            skArc(sketch, "E307", {"start": v(30.08, -6.71) * mm, "mid": v(31.14, -10.7) * mm, "end": v(32.33, -14.66) * mm});
            skLineSegment(sketch, "E308", {"start": v(23.1, -7.36) * mm, "end": v(22.94, -18.23) * mm});
            skLineSegment(sketch, "E309", {"start": v(22.94, -18.23) * mm, "end": v(23.56, -23.22) * mm});
            skLineSegment(sketch, "E310", {"start": v(23.56, -23.22) * mm, "end": v(24.1, -23.16) * mm});
            skLineSegment(sketch, "E311", {"start": v(24.1, -23.16) * mm, "end": v(24.5, -22.12) * mm});
            skLineSegment(sketch, "E312", {"start": v(24.5, -22.12) * mm, "end": v(24.82, -22.26) * mm});
            skLineSegment(sketch, "E313", {"start": v(24.82, -22.26) * mm, "end": v(25.33, -23.2) * mm});
            skLineSegment(sketch, "E314", {"start": v(25.33, -23.2) * mm, "end": v(24.86, -23.52) * mm});
            skLineSegment(sketch, "E315", {"start": v(24.86, -23.52) * mm, "end": v(25.22, -23.6) * mm});
            skLineSegment(sketch, "E316", {"start": v(25.22, -23.6) * mm, "end": v(26.3, -23.18) * mm});
            skLineSegment(sketch, "E317", {"start": v(26.3, -23.18) * mm, "end": v(26.89, -23.08) * mm});
            skLineSegment(sketch, "E318", {"start": v(26.89, -23.08) * mm, "end": v(27.75, -22.8) * mm});
            skLineSegment(sketch, "E319", {"start": v(27.75, -22.8) * mm, "end": v(29.29, -22.65) * mm});
            skLineSegment(sketch, "E320", {"start": v(29.29, -22.65) * mm, "end": v(31.83, -23.56) * mm});
            skLineSegment(sketch, "E321", {"start": v(31.83, -23.56) * mm, "end": v(32.1, -23.87) * mm});
            skLineSegment(sketch, "E322", {"start": v(32.1, -23.87) * mm, "end": v(32.28, -23.87) * mm});
            skLineSegment(sketch, "E323", {"start": v(32.28, -23.87) * mm, "end": v(32.61, -24.15) * mm});
            skLineSegment(sketch, "E324", {"start": v(32.61, -24.15) * mm, "end": v(32.77, -24.68) * mm});
            skLineSegment(sketch, "E325", {"start": v(32.77, -24.68) * mm, "end": v(33.15, -24.44) * mm});
            skLineSegment(sketch, "E326", {"start": v(33.15, -24.44) * mm, "end": v(33.97, -24.38) * mm});
            skLineSegment(sketch, "E327", {"start": v(33.97, -24.38) * mm, "end": v(34.98, -23.56) * mm});
            skLineSegment(sketch, "E328", {"start": v(34.98, -23.56) * mm, "end": v(35.53, -23.64) * mm});
            skLineSegment(sketch, "E329", {"start": v(35.53, -23.64) * mm, "end": v(35.49, -23.03) * mm});
            skLineSegment(sketch, "E330", {"start": v(35.49, -23.03) * mm, "end": v(36.5, -22.87) * mm});
            skLineSegment(sketch, "E331", {"start": v(36.5, -22.87) * mm, "end": v(37.55, -23.26) * mm});
            skLineSegment(sketch, "E332", {"start": v(37.55, -23.26) * mm, "end": v(37.99, -23.83) * mm});
            skLineSegment(sketch, "E333", {"start": v(37.99, -23.83) * mm, "end": v(38.42, -24.05) * mm});
            skLineSegment(sketch, "E334", {"start": v(38.42, -24.05) * mm, "end": v(38.6, -24.68) * mm});
            skLineSegment(sketch, "E335", {"start": v(38.6, -24.68) * mm, "end": v(39.09, -24.8) * mm});
            skLineSegment(sketch, "E336", {"start": v(39.09, -24.8) * mm, "end": v(39.4, -25.4) * mm});
            skLineSegment(sketch, "E337", {"start": v(39.4, -25.4) * mm, "end": v(40.45, -25.52) * mm});
            skLineSegment(sketch, "E338", {"start": v(33.74, -21) * mm, "end": v(41.53, -20.61) * mm});
            skLineSegment(sketch, "E339", {"start": v(25.7, -20.91) * mm, "end": v(33.23, -20.14) * mm});
            skLineSegment(sketch, "E340", {"start": v(33.23, -20.14) * mm, "end": v(33.74, -21) * mm});
            skLineSegment(sketch, "E341", {"start": v(25.7, -20.91) * mm, "end": v(25.64, -21.4) * mm});
            skLineSegment(sketch, "E342", {"start": v(25.64, -21.4) * mm, "end": v(26.29, -21.98) * mm});
            skLineSegment(sketch, "E343", {"start": v(26.29, -21.98) * mm, "end": v(26.3, -23.18) * mm});
            skArc(sketch, "E344", {"start": v(32.6, -15.46) * mm, "mid": v(32.58, -15.02) * mm, "end": v(32.33, -14.66) * mm});
            skArc(sketch, "E345", {"start": v(33, -16.01) * mm, "mid": v(32.9, -15.67) * mm, "end": v(32.6, -15.46) * mm});
            skArc(sketch, "E346", {"start": v(33, -16.01) * mm, "mid": v(32.64, -16.94) * mm, "end": v(32.78, -17.93) * mm});
            skArc(sketch, "E347", {"start": v(32.78, -19.33) * mm, "mid": v(32.86, -18.63) * mm, "end": v(32.78, -17.93) * mm});
            skArc(sketch, "E348", {"start": v(33.23, -20.14) * mm, "mid": v(33.1, -19.69) * mm, "end": v(32.78, -19.33) * mm});
            skLineSegment(sketch, "E349", {"start": v(19.43, -21.38) * mm, "end": v(13.98, -21.64) * mm});
            skLineSegment(sketch, "E350", {"start": v(13.98, -21.64) * mm, "end": v(14.06, -20.32) * mm});
            skLineSegment(sketch, "E351", {"start": v(14.06, -20.32) * mm, "end": v(15.41, -17.74) * mm});
            skLineSegment(sketch, "E352", {"start": v(19.43, -21.38) * mm, "end": v(19.24, -22.62) * mm});
            skLineSegment(sketch, "E353", {"start": v(19.24, -22.62) * mm, "end": v(19.79, -23.17) * mm});
            skLineSegment(sketch, "E354", {"start": v(19.79, -23.17) * mm, "end": v(20.13, -24.06) * mm});
            skLineSegment(sketch, "E355", {"start": v(20.13, -24.06) * mm, "end": v(20.73, -23.44) * mm});
            skArc(sketch, "E356", {"start": v(20.73, -23.44) * mm, "mid": v(21.14, -23.5) * mm, "end": v(21.55, -23.44) * mm});
            skArc(sketch, "E357", {"start": v(22.6, -23.44) * mm, "mid": v(22.07, -23.22) * mm, "end": v(21.55, -23.44) * mm});
            skLineSegment(sketch, "E358", {"start": v(23.56, -23.22) * mm, "end": v(23.4, -23.4) * mm});
            skLineSegment(sketch, "E359", {"start": v(23.4, -23.4) * mm, "end": v(22.6, -23.44) * mm});
            skArc(sketch, "E360", {"start": v(3.72, -11.95) * mm, "mid": v(4.52, -12.6) * mm, "end": v(5.5, -12.94) * mm});
            skArc(sketch, "E361", {"start": v(3.72, -11.95) * mm, "mid": v(3.38, -11.92) * mm, "end": v(3.16, -12.18) * mm});
            skArc(sketch, "E362", {"start": v(2.57, -12.16) * mm, "mid": v(2.17, -11.96) * mm, "end": v(1.83, -12.25) * mm});
            skLineSegment(sketch, "E363", {"start": v(3.16, -12.18) * mm, "end": v(2.57, -12.16) * mm});
            skLineSegment(sketch, "E364", {"start": v(1.83, -12.25) * mm, "end": v(1.54, -12.1) * mm});
            skLineSegment(sketch, "E365", {"start": v(1.54, -12.1) * mm, "end": v(0.88, -12.12) * mm});
            skLineSegment(sketch, "E366", {"start": v(0.88, -12.12) * mm, "end": v(0.79, -12.43) * mm});
            skLineSegment(sketch, "E367", {"start": v(0.79, -12.43) * mm, "end": v(0.43, -12.6) * mm});
            skLineSegment(sketch, "E368", {"start": v(0.43, -12.6) * mm, "end": v(-1.14, -12.16) * mm});
            skLineSegment(sketch, "E369", {"start": v(-1.14, -12.16) * mm, "end": v(-1.33, -11.88) * mm});
            skLineSegment(sketch, "E370", {"start": v(-1.33, -11.88) * mm, "end": v(-1.52, -11.9) * mm});
            skLineSegment(sketch, "E371", {"start": v(-1.52, -11.9) * mm, "end": v(-1.83, -12.5) * mm});
            skLineSegment(sketch, "E372", {"start": v(-1.83, -12.5) * mm, "end": v(-2.05, -12.58) * mm});
            skLineSegment(sketch, "E373", {"start": v(-2.05, -12.58) * mm, "end": v(-2.76, -12.3) * mm});
            skLineSegment(sketch, "E374", {"start": v(-2.76, -12.3) * mm, "end": v(-2.86, -11.95) * mm});
            skLineSegment(sketch, "E375", {"start": v(-2.86, -11.95) * mm, "end": v(-3.36, -11.94) * mm});
            skLineSegment(sketch, "E376", {"start": v(-3.36, -11.94) * mm, "end": v(-3.5, -11.83) * mm});
            skLineSegment(sketch, "E377", {"start": v(-3.5, -11.83) * mm, "end": v(-3.9, -12.2) * mm});
            skLineSegment(sketch, "E378", {"start": v(-3.9, -12.2) * mm, "end": v(-4.26, -12.08) * mm});
            skLineSegment(sketch, "E379", {"start": v(-4.26, -12.08) * mm, "end": v(-4.32, -11.75) * mm});
            skLineSegment(sketch, "E380", {"start": v(-4.32, -11.75) * mm, "end": v(-4.82, -11.2) * mm});
            skLineSegment(sketch, "E381", {"start": v(-4.82, -11.2) * mm, "end": v(-5.34, -11.1) * mm});
            skLineSegment(sketch, "E382", {"start": v(-5.34, -11.1) * mm, "end": v(-5.65, -11.37) * mm});
            skLineSegment(sketch, "E383", {"start": v(-5.65, -11.37) * mm, "end": v(-6.14, -11.04) * mm});
            skLineSegment(sketch, "E384", {"start": v(-6.14, -11.04) * mm, "end": v(-6.69, -10.99) * mm});
            skLineSegment(sketch, "E385", {"start": v(-6.69, -10.99) * mm, "end": v(-7.07, -10.8) * mm});
            skLineSegment(sketch, "E386", {"start": v(-7.07, -10.8) * mm, "end": v(-7.7, -10.76) * mm});
            skLineSegment(sketch, "E387", {"start": v(-7.7, -10.76) * mm, "end": v(-7.72, -10.16) * mm});
            skLineSegment(sketch, "E388", {"start": v(-7.72, -10.16) * mm, "end": v(-8.06, -10) * mm});
            skLineSegment(sketch, "E389", {"start": v(-8.06, -10) * mm, "end": v(-8.1, -10.2) * mm});
            skLineSegment(sketch, "E390", {"start": v(-8.1, -10.2) * mm, "end": v(-8.36, -10.21) * mm});
            skLineSegment(sketch, "E391", {"start": v(-8.36, -10.21) * mm, "end": v(-8.63, -9.9) * mm});
            skLineSegment(sketch, "E392", {"start": v(-8.63, -9.9) * mm, "end": v(-8.76, -10.2) * mm});
            skLineSegment(sketch, "E393", {"start": v(-8.76, -10.2) * mm, "end": v(-8.95, -10.21) * mm});
            skLineSegment(sketch, "E394", {"start": v(-8.95, -10.21) * mm, "end": v(-9.83, -9.42) * mm});
            skLineSegment(sketch, "E395", {"start": v(7.69, -26.38) * mm, "end": v(8.3, -26.17) * mm});
            skLineSegment(sketch, "E396", {"start": v(8.3, -26.17) * mm, "end": v(9.62, -26.08) * mm});
            skLineSegment(sketch, "E397", {"start": v(9.62, -26.08) * mm, "end": v(11.23, -26.64) * mm});
            skLineSegment(sketch, "E398", {"start": v(11.23, -26.64) * mm, "end": v(12.18, -26.8) * mm});
            skLineSegment(sketch, "E399", {"start": v(12.18, -26.8) * mm, "end": v(12.9, -26.47) * mm});
            skLineSegment(sketch, "E400", {"start": v(12.9, -26.47) * mm, "end": v(12.58, -26.28) * mm});
            skLineSegment(sketch, "E401", {"start": v(12.58, -26.28) * mm, "end": v(12.67, -26.04) * mm});
            skLineSegment(sketch, "E402", {"start": v(12.67, -26.04) * mm, "end": v(13.15, -25.87) * mm});
            skLineSegment(sketch, "E403", {"start": v(13.15, -25.87) * mm, "end": v(13.42, -26.08) * mm});
            skLineSegment(sketch, "E404", {"start": v(13.42, -26.08) * mm, "end": v(13.74, -25.9) * mm});
            skLineSegment(sketch, "E405", {"start": v(13.74, -25.9) * mm, "end": v(14.2, -26.01) * mm});
            skLineSegment(sketch, "E406", {"start": v(14.2, -26.01) * mm, "end": v(14.49, -26.47) * mm});
            skLineSegment(sketch, "E407", {"start": v(14.49, -26.47) * mm, "end": v(14.48, -26.79) * mm});
            skLineSegment(sketch, "E408", {"start": v(14.48, -26.79) * mm, "end": v(15.2, -26.8) * mm});
            skLineSegment(sketch, "E409", {"start": v(15.2, -26.8) * mm, "end": v(15.48, -27.04) * mm});
            skLineSegment(sketch, "E410", {"start": v(15.48, -27.04) * mm, "end": v(15.22, -27.45) * mm});
            skLineSegment(sketch, "E411", {"start": v(15.22, -27.45) * mm, "end": v(16.7, -28.28) * mm});
            skLineSegment(sketch, "E412", {"start": v(16.7, -28.28) * mm, "end": v(17.3, -28.07) * mm});
            skLineSegment(sketch, "E413", {"start": v(17.3, -28.07) * mm, "end": v(17.4, -27.7) * mm});
            skLineSegment(sketch, "E414", {"start": v(17.4, -27.7) * mm, "end": v(17.83, -27.61) * mm});
            skLineSegment(sketch, "E415", {"start": v(17.83, -27.61) * mm, "end": v(18.04, -27.36) * mm});
            skLineSegment(sketch, "E416", {"start": v(18.04, -27.36) * mm, "end": v(18.31, -27.53) * mm});
            skLineSegment(sketch, "E417", {"start": v(18.31, -27.53) * mm, "end": v(18.41, -27.95) * mm});
            skLineSegment(sketch, "E418", {"start": v(18.41, -27.95) * mm, "end": v(18.59, -28.04) * mm});
            skLineSegment(sketch, "E419", {"start": v(18.59, -28.04) * mm, "end": v(18.98, -27.5) * mm});
            skLineSegment(sketch, "E420", {"start": v(18.98, -27.5) * mm, "end": v(18.98, -27.39) * mm});
            skLineSegment(sketch, "E421", {"start": v(18.98, -27.39) * mm, "end": v(18.8, -27.34) * mm});
            skLineSegment(sketch, "E422", {"start": v(18.8, -27.34) * mm, "end": v(18.9, -27.17) * mm});
            skLineSegment(sketch, "E423", {"start": v(18.9, -27.17) * mm, "end": v(18.94, -26.83) * mm});
            skLineSegment(sketch, "E424", {"start": v(18.94, -26.83) * mm, "end": v(19.24, -26.8) * mm});
            skLineSegment(sketch, "E425", {"start": v(19.24, -26.8) * mm, "end": v(19.42, -26.58) * mm});
            skLineSegment(sketch, "E426", {"start": v(19.42, -26.58) * mm, "end": v(19.56, -26.7) * mm});
            skLineSegment(sketch, "E427", {"start": v(19.56, -26.7) * mm, "end": v(19.53, -27.12) * mm});
            skLineSegment(sketch, "E428", {"start": v(19.53, -27.12) * mm, "end": v(20.03, -27.22) * mm});
            skLineSegment(sketch, "E429", {"start": v(20.03, -27.22) * mm, "end": v(20.9, -27.61) * mm});
            skLineSegment(sketch, "E430", {"start": v(20.9, -27.61) * mm, "end": v(21, -27.8) * mm});
            skLineSegment(sketch, "E431", {"start": v(21, -27.8) * mm, "end": v(21.49, -27.81) * mm});
            skLineSegment(sketch, "E432", {"start": v(21.49, -27.81) * mm, "end": v(21.66, -27.94) * mm});
            skLineSegment(sketch, "E433", {"start": v(21.66, -27.94) * mm, "end": v(22.02, -27.5) * mm});
            skLineSegment(sketch, "E434", {"start": v(22.02, -27.5) * mm, "end": v(22, -27.3) * mm});
            skLineSegment(sketch, "E435", {"start": v(22, -27.3) * mm, "end": v(21.8, -27.26) * mm});
            skLineSegment(sketch, "E436", {"start": v(21.8, -27.26) * mm, "end": v(21.3, -26.84) * mm});
            skLineSegment(sketch, "E437", {"start": v(21.3, -26.84) * mm, "end": v(20.36, -26.67) * mm});
            skLineSegment(sketch, "E438", {"start": v(20.36, -26.67) * mm, "end": v(19.9, -26.4) * mm});
            skLineSegment(sketch, "E439", {"start": v(19.9, -26.4) * mm, "end": v(20.23, -25.87) * mm});
            skLineSegment(sketch, "E440", {"start": v(20.23, -25.87) * mm, "end": v(20.17, -25.66) * mm});
            skLineSegment(sketch, "E441", {"start": v(20.17, -25.66) * mm, "end": v(20.65, -25.65) * mm});
            skLineSegment(sketch, "E442", {"start": v(20.65, -25.65) * mm, "end": v(20.92, -25.26) * mm});
            skLineSegment(sketch, "E443", {"start": v(20.92, -25.26) * mm, "end": v(20.67, -24.5) * mm});
            skLineSegment(sketch, "E444", {"start": v(20.67, -24.5) * mm, "end": v(20.2, -24.72) * mm});
            skLineSegment(sketch, "E445", {"start": v(20.2, -24.72) * mm, "end": v(20.14, -25.2) * mm});
            skLineSegment(sketch, "E446", {"start": v(20.14, -25.2) * mm, "end": v(19.63, -25.12) * mm});
            skLineSegment(sketch, "E447", {"start": v(19.63, -25.12) * mm, "end": v(19.48, -24.83) * mm});
            skLineSegment(sketch, "E448", {"start": v(19.48, -24.83) * mm, "end": v(20.13, -24.06) * mm});
            skLineSegment(sketch, "E449", {"start": v(15.41, -17.74) * mm, "end": v(15.28, -17.4) * mm});
            skLineSegment(sketch, "E450", {"start": v(15.28, -17.4) * mm, "end": v(15.5, -17.37) * mm});
            skLineSegment(sketch, "E451", {"start": v(15.5, -17.37) * mm, "end": v(15.48, -16.93) * mm});
            skLineSegment(sketch, "E452", {"start": v(15.48, -16.93) * mm, "end": v(15.23, -16.69) * mm});
            skLineSegment(sketch, "E453", {"start": v(15.23, -16.69) * mm, "end": v(15.22, -16.26) * mm});
            skLineSegment(sketch, "E454", {"start": v(15.22, -16.26) * mm, "end": v(14.92, -15.52) * mm});
            skLineSegment(sketch, "E455", {"start": v(14.92, -15.52) * mm, "end": v(14.99, -14.76) * mm});
            skLineSegment(sketch, "E456", {"start": v(14.99, -14.76) * mm, "end": v(15.06, -13.88) * mm});
            skLineSegment(sketch, "E457", {"start": v(15.06, -13.88) * mm, "end": v(14.84, -12.79) * mm});
            skLineSegment(sketch, "E458", {"start": v(14.84, -12.79) * mm, "end": v(14.94, -11.5) * mm});
            skLineSegment(sketch, "E459", {"start": v(14.94, -11.5) * mm, "end": v(15.51, -11.06) * mm});
            skLineSegment(sketch, "E460", {"start": v(15.51, -11.06) * mm, "end": v(15.44, -10.78) * mm});
            skLineSegment(sketch, "E461", {"start": v(15.44, -10.78) * mm, "end": v(15.92, -10.02) * mm});
            skLineSegment(sketch, "E462", {"start": v(15.92, -10.02) * mm, "end": v(16.45, -9.82) * mm});
            skLineSegment(sketch, "E463", {"start": v(16.45, -9.82) * mm, "end": v(16.35, -9.14) * mm});
            skLineSegment(sketch, "E464", {"start": v(16.35, -9.14) * mm, "end": v(16.8, -8.34) * mm});
            skLineSegment(sketch, "E465", {"start": v(16.8, -8.34) * mm, "end": v(17, -8.22) * mm});
            skLineSegment(sketch, "E466", {"start": v(17, -8.22) * mm, "end": v(17.17, -7.99) * mm});
            skLineSegment(sketch, "E467", {"start": v(17.17, -7.99) * mm, "end": v(17.09, -7.7) * mm});
            skLineSegment(sketch, "E468", {"start": v(17.09, -7.7) * mm, "end": v(17.56, -7.14) * mm});
            skLineSegment(sketch, "E469", {"start": v(17.56, -7.14) * mm, "end": v(17.71, -6.44) * mm});
            skLineSegment(sketch, "E470", {"start": v(17.71, -6.44) * mm, "end": v(17.52, -5.9) * mm});
            skLineSegment(sketch, "E471", {"start": v(17.52, -5.9) * mm, "end": v(18.16, -5.64) * mm});
            skLineSegment(sketch, "E472", {"start": v(18.16, -5.64) * mm, "end": v(18.4, -4.3) * mm});
            skLineSegment(sketch, "E473", {"start": v(18.72, -2.44) * mm, "end": v(18.72, -3.38) * mm});
            skLineSegment(sketch, "E474", {"start": v(18.72, -3.38) * mm, "end": v(18.4, -4.3) * mm});
            skLineSegment(sketch, "E475", {"start": v(18.72, -2.44) * mm, "end": v(19.66, -1.8) * mm});
            skLineSegment(sketch, "E476", {"start": v(19.66, -1.8) * mm, "end": v(19.72, -1.24) * mm});
            skLineSegment(sketch, "E477", {"start": v(19.72, -1.24) * mm, "end": v(19.83, -0.99) * mm});
            skLineSegment(sketch, "E478", {"start": v(19.83, -0.99) * mm, "end": v(19.82, -0.76) * mm});
            skLineSegment(sketch, "E479", {"start": v(19.82, -0.76) * mm, "end": v(19.59, -0.7) * mm});
            skLineSegment(sketch, "E480", {"start": v(19.59, -0.7) * mm, "end": v(19.18, -0.67) * mm});
            skLineSegment(sketch, "E481", {"start": v(19.18, -0.67) * mm, "end": v(18.63, 0.23) * mm});
            skLineSegment(sketch, "E482", {"start": v(18.63, 0.23) * mm, "end": v(18.18, 2.02) * mm});
            skLineSegment(sketch, "E483", {"start": v(18.18, 2.02) * mm, "end": v(17.6, 2.09) * mm});
            skLineSegment(sketch, "E484", {"start": v(17.6, 2.09) * mm, "end": v(16.39, 2.96) * mm});
            skLineSegment(sketch, "E485", {"start": v(16.39, 2.96) * mm, "end": v(16.13, 3.52) * mm});
            skLineSegment(sketch, "E486", {"start": v(16.13, 3.52) * mm, "end": v(16.47, 4.61) * mm});
            skLineSegment(sketch, "E487", {"start": v(16.47, 4.61) * mm, "end": v(16.68, 5.46) * mm});
            skLineSegment(sketch, "E488", {"start": v(16.68, 5.46) * mm, "end": v(15.26, 5.8) * mm});
            skLineSegment(sketch, "E489", {"start": v(15.26, 5.8) * mm, "end": v(15.22, 6.72) * mm});
            skLineSegment(sketch, "E490", {"start": v(15.22, 6.72) * mm, "end": v(14.39, 7.2) * mm});
            skLineSegment(sketch, "E491", {"start": v(14.39, 7.2) * mm, "end": v(13.26, 8.36) * mm});
            skLineSegment(sketch, "E492", {"start": v(13.26, 8.36) * mm, "end": v(12.82, 10.21) * mm});
            skLineSegment(sketch, "E493", {"start": v(12.82, 10.21) * mm, "end": v(12.95, 10.5) * mm});
            skLineSegment(sketch, "E494", {"start": v(12.95, 10.5) * mm, "end": v(13.18, 10.78) * mm});
            skLineSegment(sketch, "E495", {"start": v(13.18, 10.78) * mm, "end": v(13.15, 11.3) * mm});
            skLineSegment(sketch, "E496", {"start": v(13.15, 11.3) * mm, "end": v(13.71, 11.58) * mm});
            skLineSegment(sketch, "E497", {"start": v(12.16, 11.34) * mm, "end": v(12.95, 10.5) * mm});
            skLineSegment(sketch, "E498", {"start": v(13.71, 11.58) * mm, "end": v(13.71, 12.16) * mm});
            skLineSegment(sketch, "E499", {"start": v(13.71, 12.16) * mm, "end": v(14.1, 12.4) * mm});
            skLineSegment(sketch, "E500", {"start": v(14.1, 12.4) * mm, "end": v(14.19, 13.08) * mm});
            skLineSegment(sketch, "E501", {"start": v(14.19, 13.08) * mm, "end": v(13.74, 13.44) * mm});
            skLineSegment(sketch, "E502", {"start": v(13.74, 13.44) * mm, "end": v(13.92, 14.1) * mm});
            skLineSegment(sketch, "E503", {"start": v(13.92, 14.1) * mm, "end": v(15.4, 14.7) * mm});
            skLineSegment(sketch, "E504", {"start": v(15.4, 14.7) * mm, "end": v(15.87, 16.5) * mm});
            skLineSegment(sketch, "E505", {"start": v(15.87, 16.5) * mm, "end": v(15.22, 17.22) * mm});
            skLineSegment(sketch, "E506", {"start": v(15.22, 17.22) * mm, "end": v(15.19, 17.47) * mm});
            skLineSegment(sketch, "E507", {"start": v(15.19, 17.47) * mm, "end": v(14.64, 17.78) * mm});
            skLineSegment(sketch, "E508", {"start": v(14.64, 17.78) * mm, "end": v(14.65, 18.08) * mm});
            skLineSegment(sketch, "E509", {"start": v(14.45, 18.4) * mm, "end": v(13.59, 18.7) * mm});
            skLineSegment(sketch, "E510", {"start": v(14.45, 18.4) * mm, "end": v(14.65, 18.08) * mm});
            skLineSegment(sketch, "E511", {"start": v(13.59, 18.7) * mm, "end": v(13.23, 19.33) * mm});
            skLineSegment(sketch, "E512", {"start": v(13.23, 19.33) * mm, "end": v(13.2, 19.8) * mm});
            skLineSegment(sketch, "E513", {"start": v(13.2, 19.8) * mm, "end": v(13.48, 20.3) * mm});
            skLineSegment(sketch, "E514", {"start": v(13.48, 20.3) * mm, "end": v(13.47, 20.53) * mm});
            skLineSegment(sketch, "E515", {"start": v(13.47, 20.53) * mm, "end": v(13.1, 20.8) * mm});
            skLineSegment(sketch, "E516", {"start": v(13.1, 20.8) * mm, "end": v(12.91, 21.3) * mm});
            skLineSegment(sketch, "E517", {"start": v(23.33, 7.83) * mm, "end": v(22.67, 15.9) * mm});
            skLineSegment(sketch, "E518", {"start": v(22.67, 15.9) * mm, "end": v(23.48, 15.63) * mm});
            skLineSegment(sketch, "E519", {"start": v(23.48, 15.63) * mm, "end": v(24.38, 16.11) * mm});
            skLineSegment(sketch, "E520", {"start": v(21.55, 18.48) * mm, "end": v(21.76, 17.6) * mm});
            skLineSegment(sketch, "E521", {"start": v(21.76, 17.6) * mm, "end": v(22.16, 17.02) * mm});
            skLineSegment(sketch, "E522", {"start": v(22.16, 17.02) * mm, "end": v(22.45, 16.04) * mm});
            skLineSegment(sketch, "E523", {"start": v(22.45, 16.04) * mm, "end": v(22.67, 15.9) * mm});
            skLineSegment(sketch, "E524", {"start": v(3.15, 39.65) * mm, "end": v(3.25, 40.92) * mm});
            skLineSegment(sketch, "E525", {"start": v(3.25, 40.92) * mm, "end": v(3.8, 40.8) * mm});
            skLineSegment(sketch, "E526", {"start": v(3.8, 40.8) * mm, "end": v(4.13, 39.08) * mm});
            skLineSegment(sketch, "E527", {"start": v(4.13, 39.08) * mm, "end": v(4.46, 38.71) * mm});
            skLineSegment(sketch, "E528", {"start": v(4.46, 38.71) * mm, "end": v(5.2, 38.72) * mm});
            skLineSegment(sketch, "E529", {"start": v(5.2, 38.72) * mm, "end": v(5.22, 38.5) * mm});
            skLineSegment(sketch, "E530", {"start": v(5.22, 38.5) * mm, "end": v(6.17, 38.44) * mm});
            skLineSegment(sketch, "E531", {"start": v(6.17, 38.44) * mm, "end": v(6.15, 38.09) * mm});
            skLineSegment(sketch, "E532", {"start": v(6.15, 38.09) * mm, "end": v(7.06, 38.11) * mm});
            skLineSegment(sketch, "E533", {"start": v(7.06, 38.11) * mm, "end": v(7.24, 38.45) * mm});
            skLineSegment(sketch, "E534", {"start": v(7.24, 38.45) * mm, "end": v(7.54, 38.58) * mm});
            skLineSegment(sketch, "E535", {"start": v(7.54, 38.58) * mm, "end": v(7.77, 38.42) * mm});
            skLineSegment(sketch, "E536", {"start": v(7.77, 38.42) * mm, "end": v(8.2, 38.42) * mm});
            skLineSegment(sketch, "E537", {"start": v(8.2, 38.42) * mm, "end": v(9.97, 37.56) * mm});
            skLineSegment(sketch, "E538", {"start": v(9.97, 37.56) * mm, "end": v(10.29, 37.62) * mm});
            skLineSegment(sketch, "E539", {"start": v(10.29, 37.62) * mm, "end": v(10.33, 37.39) * mm});
            skLineSegment(sketch, "E540", {"start": v(10.33, 37.39) * mm, "end": v(10.77, 37.18) * mm});
            skLineSegment(sketch, "E541", {"start": v(10.77, 37.18) * mm, "end": v(10.96, 37.17) * mm});
            skLineSegment(sketch, "E542", {"start": v(10.96, 37.17) * mm, "end": v(11.01, 36.9) * mm});
            skLineSegment(sketch, "E543", {"start": v(11.01, 36.9) * mm, "end": v(11.42, 36.73) * mm});
            skLineSegment(sketch, "E544", {"start": v(11.42, 36.73) * mm, "end": v(11.77, 36.67) * mm});
            skLineSegment(sketch, "E545", {"start": v(11.77, 36.67) * mm, "end": v(12.07, 36.74) * mm});
            skLineSegment(sketch, "E546", {"start": v(12.07, 36.74) * mm, "end": v(12.8, 37.37) * mm});
            skLineSegment(sketch, "E547", {"start": v(12.8, 37.37) * mm, "end": v(13.07, 37.39) * mm});
            skLineSegment(sketch, "E548", {"start": v(13.07, 37.39) * mm, "end": v(13.22, 37) * mm});
            skLineSegment(sketch, "E549", {"start": v(13.22, 37) * mm, "end": v(13.45, 36.9) * mm});
            skLineSegment(sketch, "E550", {"start": v(13.45, 36.9) * mm, "end": v(13.65, 37.06) * mm});
            skLineSegment(sketch, "E551", {"start": v(13.65, 37.06) * mm, "end": v(14.9, 37.09) * mm});
            skLineSegment(sketch, "E552", {"start": v(14.9, 37.09) * mm, "end": v(15.18, 36.68) * mm});
            skLineSegment(sketch, "E553", {"start": v(15.18, 36.68) * mm, "end": v(15.42, 36.66) * mm});
            skLineSegment(sketch, "E554", {"start": v(15.42, 36.66) * mm, "end": v(15.55, 36.79) * mm});
            skLineSegment(sketch, "E555", {"start": v(15.55, 36.79) * mm, "end": v(16.12, 36.84) * mm});
            skLineSegment(sketch, "E556", {"start": v(16.12, 36.84) * mm, "end": v(15.81, 36.5) * mm});
            skLineSegment(sketch, "E557", {"start": v(15.81, 36.5) * mm, "end": v(15.16, 36.26) * mm});
            skLineSegment(sketch, "E558", {"start": v(15.16, 36.26) * mm, "end": v(13.42, 35.46) * mm});
            skLineSegment(sketch, "E559", {"start": v(13.42, 35.46) * mm, "end": v(12.9, 35.1) * mm});
            skLineSegment(sketch, "E560", {"start": v(12.9, 35.1) * mm, "end": v(12.57, 34.6) * mm});
            skLineSegment(sketch, "E561", {"start": v(12.57, 34.6) * mm, "end": v(12.05, 33.8) * mm});
            skLineSegment(sketch, "E562", {"start": v(12.05, 33.8) * mm, "end": v(11.83, 33.73) * mm});
            skLineSegment(sketch, "E563", {"start": v(11.83, 33.73) * mm, "end": v(11.13, 32.88) * mm});
            skLineSegment(sketch, "E564", {"start": v(11.13, 32.88) * mm, "end": v(10.68, 32.9) * mm});
            skLineSegment(sketch, "E565", {"start": v(10.68, 32.9) * mm, "end": v(10.32, 32.47) * mm});
            skLineSegment(sketch, "E566", {"start": v(10.32, 32.47) * mm, "end": v(10.44, 32.27) * mm});
            skLineSegment(sketch, "E567", {"start": v(10.44, 32.27) * mm, "end": v(11.08, 32.2) * mm});
            skLineSegment(sketch, "E568", {"start": v(11.08, 32.2) * mm, "end": v(13.31, 33.18) * mm});
            skLineSegment(sketch, "E569", {"start": v(13.31, 33.18) * mm, "end": v(13.62, 32.93) * mm});
            skLineSegment(sketch, "E570", {"start": v(13.62, 32.93) * mm, "end": v(13.1, 32.12) * mm});
            skLineSegment(sketch, "E571", {"start": v(13.1, 32.12) * mm, "end": v(13.17, 31.86) * mm});
            skLineSegment(sketch, "E572", {"start": v(13.17, 31.86) * mm, "end": v(13.55, 32.06) * mm});
            skLineSegment(sketch, "E573", {"start": v(13.55, 32.06) * mm, "end": v(14.01, 32.06) * mm});
            skLineSegment(sketch, "E574", {"start": v(14.01, 32.06) * mm, "end": v(14.2, 31.73) * mm});
            skLineSegment(sketch, "E575", {"start": v(14.2, 31.73) * mm, "end": v(14.3, 31.73) * mm});
            skLineSegment(sketch, "E576", {"start": v(14.3, 31.73) * mm, "end": v(14.55, 32.02) * mm});
            skLineSegment(sketch, "E577", {"start": v(14.55, 32.02) * mm, "end": v(15.03, 32.2) * mm});
            skLineSegment(sketch, "E578", {"start": v(15.03, 32.2) * mm, "end": v(15.71, 32.6) * mm});
            skLineSegment(sketch, "E579", {"start": v(15.71, 32.6) * mm, "end": v(15.68, 32.72) * mm});
            skLineSegment(sketch, "E580", {"start": v(15.68, 32.72) * mm, "end": v(15.81, 32.88) * mm});
            skLineSegment(sketch, "E581", {"start": v(15.81, 32.88) * mm, "end": v(16.8, 33) * mm});
            skLineSegment(sketch, "E582", {"start": v(16.8, 33) * mm, "end": v(17.7, 33.6) * mm});
            skLineSegment(sketch, "E583", {"start": v(17.7, 33.6) * mm, "end": v(18.08, 34.3) * mm});
            skLineSegment(sketch, "E584", {"start": v(18.08, 34.3) * mm, "end": v(18.37, 34.37) * mm});
            skLineSegment(sketch, "E585", {"start": v(18.37, 34.37) * mm, "end": v(18.9, 35.03) * mm});
            skLineSegment(sketch, "E586", {"start": v(18.9, 35.03) * mm, "end": v(19.49, 35.4) * mm});
            skLineSegment(sketch, "E587", {"start": v(19.49, 35.4) * mm, "end": v(20.24, 35.5) * mm});
            skLineSegment(sketch, "E588", {"start": v(20.24, 35.5) * mm, "end": v(20.5, 35.35) * mm});
            skLineSegment(sketch, "E589", {"start": v(20.5, 35.35) * mm, "end": v(20.45, 35.16) * mm});
            skLineSegment(sketch, "E590", {"start": v(20.45, 35.16) * mm, "end": v(19.9, 35.03) * mm});
            skLineSegment(sketch, "E591", {"start": v(19.9, 35.03) * mm, "end": v(19.62, 34.52) * mm});
            skLineSegment(sketch, "E592", {"start": v(19.62, 34.52) * mm, "end": v(19.28, 34.34) * mm});
            skLineSegment(sketch, "E593", {"start": v(19.28, 34.34) * mm, "end": v(19.23, 34.1) * mm});
            skLineSegment(sketch, "E594", {"start": v(19.23, 34.1) * mm, "end": v(18.8, 33.47) * mm});
            skLineSegment(sketch, "E595", {"start": v(18.8, 33.47) * mm, "end": v(18.83, 33.1) * mm});
            skLineSegment(sketch, "E596", {"start": v(18.83, 33.1) * mm, "end": v(18.92, 33.02) * mm});
            skLineSegment(sketch, "E597", {"start": v(18.92, 33.02) * mm, "end": v(19.62, 33.68) * mm});
            skLineSegment(sketch, "E598", {"start": v(19.62, 33.68) * mm, "end": v(19.82, 33.47) * mm});
            skLineSegment(sketch, "E599", {"start": v(19.82, 33.47) * mm, "end": v(20.84, 33.22) * mm});
            skLineSegment(sketch, "E600", {"start": v(20.84, 33.22) * mm, "end": v(21.5, 32.3) * mm});
            skLineSegment(sketch, "E601", {"start": v(21.5, 32.3) * mm, "end": v(22.18, 32.3) * mm});
            skLineSegment(sketch, "E602", {"start": v(41.78, 20.28) * mm, "end": v(41.02, 19.6) * mm});
            skLineSegment(sketch, "E603", {"start": v(41.02, 19.6) * mm, "end": v(40.12, 18.98) * mm});
            skLineSegment(sketch, "E604", {"start": v(40.12, 18.98) * mm, "end": v(41.3, 11.36) * mm});
            skLineSegment(sketch, "E605", {"start": v(41.3, 11.36) * mm, "end": v(53.33, 13.6) * mm});
            skLineSegment(sketch, "E606", {"start": v(53.33, 13.6) * mm, "end": v(54.51, 9.42) * mm});
            skLineSegment(sketch, "E607", {"start": v(54.51, 9.42) * mm, "end": v(56.17, 9.73) * mm});
            skLineSegment(sketch, "E608", {"start": v(61.97, 21.47) * mm, "end": v(61.52, 23.58) * mm});
            skLineSegment(sketch, "E609", {"start": v(61.52, 23.58) * mm, "end": v(62.44, 23.83) * mm});
            skLineSegment(sketch, "E610", {"start": v(62.44, 23.83) * mm, "end": v(63.57, 22.39) * mm});
            skLineSegment(sketch, "E611", {"start": v(63.57, 22.39) * mm, "end": v(62.92, 22) * mm});
            skLineSegment(sketch, "E612", {"start": v(62.92, 22) * mm, "end": v(62.78, 21.76) * mm});
            skLineSegment(sketch, "E613", {"start": v(62.78, 21.76) * mm, "end": v(61.97, 21.47) * mm});
            skLineSegment(sketch, "E614", {"start": v(61.97, 21.47) * mm, "end": v(61.88, 21.26) * mm});
            skLineSegment(sketch, "E615", {"start": v(61.88, 21.26) * mm, "end": v(59.5, 20.4) * mm});
            skLineSegment(sketch, "E616", {"start": v(59.5, 20.4) * mm, "end": v(59.42, 20.5) * mm});
            skLineSegment(sketch, "E617", {"start": v(59.42, 20.5) * mm, "end": v(58.57, 19.7) * mm});
            skLineSegment(sketch, "E618", {"start": v(58.57, 19.7) * mm, "end": v(57.78, 19.2) * mm});
            skLineSegment(sketch, "E619", {"start": v(61.52, 23.58) * mm, "end": v(57.28, 22.73) * mm});
            skLineSegment(sketch, "E620", {"start": v(57.28, 25.2) * mm, "end": v(62.18, 26.35) * mm});
            skLineSegment(sketch, "E621", {"start": v(62.18, 26.35) * mm, "end": v(62.53, 26.85) * mm});
            skLineSegment(sketch, "E622", {"start": v(62.53, 26.85) * mm, "end": v(63.1, 27.05) * mm});
            skLineSegment(sketch, "E623", {"start": v(63.1, 27.05) * mm, "end": v(63.49, 26.46) * mm});
            skLineSegment(sketch, "E624", {"start": v(63.49, 26.46) * mm, "end": v(63.15, 25.44) * mm});
            skLineSegment(sketch, "E625", {"start": v(63.15, 25.44) * mm, "end": v(63.43, 25.01) * mm});
            skLineSegment(sketch, "E626", {"start": v(63.43, 25.01) * mm, "end": v(63.59, 25.14) * mm});
            skLineSegment(sketch, "E627", {"start": v(63.59, 25.14) * mm, "end": v(63.92, 25.06) * mm});
            skLineSegment(sketch, "E628", {"start": v(63.92, 25.06) * mm, "end": v(64.78, 23.8) * mm});
            skLineSegment(sketch, "E629", {"start": v(64.78, 23.8) * mm, "end": v(65.43, 23.73) * mm});
            skLineSegment(sketch, "E630", {"start": v(65.43, 23.73) * mm, "end": v(65.78, 23.9) * mm});
            skLineSegment(sketch, "E631", {"start": v(65.78, 23.9) * mm, "end": v(65.96, 24.09) * mm});
            skLineSegment(sketch, "E632", {"start": v(63.57, 22.39) * mm, "end": v(64, 22.57) * mm});
            skLineSegment(sketch, "E633", {"start": v(64, 22.57) * mm, "end": v(63.97, 22.94) * mm});
            skLineSegment(sketch, "E634", {"start": v(63.97, 22.94) * mm, "end": v(64.52, 23.33) * mm});
            skLineSegment(sketch, "E635", {"start": v(64.52, 23.33) * mm, "end": v(64.68, 22.67) * mm});
            skLineSegment(sketch, "E636", {"start": v(64.68, 22.67) * mm, "end": v(65.03, 23.05) * mm});
            skLineSegment(sketch, "E637", {"start": v(65.03, 23.05) * mm, "end": v(65.49, 23.33) * mm});
            skLineSegment(sketch, "E638", {"start": v(65.49, 23.33) * mm, "end": v(66.03, 23.52) * mm});
            skLineSegment(sketch, "E639", {"start": v(66.03, 23.52) * mm, "end": v(66.35, 23.63) * mm});
            skLineSegment(sketch, "E640", {"start": v(66.35, 23.63) * mm, "end": v(66.27, 24.2) * mm});
            skLineSegment(sketch, "E641", {"start": v(66.27, 24.2) * mm, "end": v(66.03, 24.53) * mm});
            skLineSegment(sketch, "E642", {"start": v(65.96, 24.09) * mm, "end": v(66.03, 24.53) * mm});
            skLineSegment(sketch, "E643", {"start": v(55.36, 32.56) * mm, "end": v(59.47, 33.7) * mm});
            skLineSegment(sketch, "E644", {"start": v(59.47, 33.7) * mm, "end": v(59.65, 33.32) * mm});
            skLineSegment(sketch, "E645", {"start": v(59.65, 33.32) * mm, "end": v(59.5, 32.74) * mm});
            skLineSegment(sketch, "E646", {"start": v(59.5, 32.74) * mm, "end": v(59.88, 32.3) * mm});
            skLineSegment(sketch, "E647", {"start": v(59.88, 32.3) * mm, "end": v(59.8, 32.18) * mm});
            skLineSegment(sketch, "E648", {"start": v(59.8, 32.18) * mm, "end": v(59.9, 31.96) * mm});
            skLineSegment(sketch, "E649", {"start": v(59.9, 31.96) * mm, "end": v(59.25, 31.22) * mm});
            skLineSegment(sketch, "E650", {"start": v(59.25, 31.22) * mm, "end": v(58.9, 31.07) * mm});
            skLineSegment(sketch, "E651", {"start": v(58.9, 31.07) * mm, "end": v(58.9, 30.8) * mm});
            skLineSegment(sketch, "E652", {"start": v(58.9, 30.8) * mm, "end": v(59.04, 30.63) * mm});
            skLineSegment(sketch, "E653", {"start": v(59.04, 30.63) * mm, "end": v(58.89, 27.04) * mm});
            skLineSegment(sketch, "E654", {"start": v(58.89, 27.04) * mm, "end": v(59.05, 26.97) * mm});
            skLineSegment(sketch, "E655", {"start": v(59.05, 26.97) * mm, "end": v(59.02, 26.24) * mm});
            skLineSegment(sketch, "E656", {"start": v(59.02, 26.24) * mm, "end": v(59.02, 25.9) * mm});
            skLineSegment(sketch, "E657", {"start": v(59.02, 25.9) * mm, "end": v(59.29, 25.67) * mm});
            skLineSegment(sketch, "E658", {"start": v(19.59, -0.7) * mm, "end": v(19.92, -0.2) * mm});
            skLineSegment(sketch, "E659", {"start": v(19.92, -0.2) * mm, "end": v(20.33, 0.07) * mm});
            skLineSegment(sketch, "E660", {"start": v(20.33, 0.07) * mm, "end": v(21.48, -0.34) * mm});
            skLineSegment(sketch, "E661", {"start": v(21.48, -0.34) * mm, "end": v(21.62, -0.1) * mm});
            skLineSegment(sketch, "E662", {"start": v(21.62, -0.1) * mm, "end": v(21.4, 0.24) * mm});
            skLineSegment(sketch, "E663", {"start": v(21.4, 0.24) * mm, "end": v(21.45, 0.78) * mm});
            skLineSegment(sketch, "E664", {"start": v(21.45, 0.78) * mm, "end": v(21.99, 1.05) * mm});
            skLineSegment(sketch, "E665", {"start": v(21.99, 1.05) * mm, "end": v(22.42, 1.26) * mm});
            skLineSegment(sketch, "E666", {"start": v(22.42, 1.26) * mm, "end": v(22.13, 1.77) * mm});
            skLineSegment(sketch, "E667", {"start": v(22.13, 1.77) * mm, "end": v(22.42, 2.07) * mm});
            skLineSegment(sketch, "E668", {"start": v(22.42, 2.07) * mm, "end": v(22.52, 2.45) * mm});
            skLineSegment(sketch, "E669", {"start": v(22.52, 2.45) * mm, "end": v(22.62, 3.82) * mm});
            skLineSegment(sketch, "E670", {"start": v(22.62, 3.82) * mm, "end": v(23.59, 5.32) * mm});
            skLineSegment(sketch, "E671", {"start": v(23.59, 5.32) * mm, "end": v(23.52, 6.37) * mm});
            skLineSegment(sketch, "E672", {"start": v(23.52, 6.37) * mm, "end": v(23.15, 6.9) * mm});
            skLineSegment(sketch, "E673", {"start": v(23.15, 6.9) * mm, "end": v(23.33, 7.83) * mm});
            skLineSegment(sketch, "E674", {"start": v(22.52, 2.45) * mm, "end": v(24.34, 2.9) * mm});
            skLineSegment(sketch, "E675", {"start": v(24.34, 2.9) * mm, "end": v(24.97, 2.44) * mm});
            skLineSegment(sketch, "E676", {"start": v(24.97, 2.44) * mm, "end": v(25.17, 2.94) * mm});
            skLineSegment(sketch, "E677", {"start": v(25.17, 2.94) * mm, "end": v(25.67, 3.2) * mm});
            skLineSegment(sketch, "E678", {"start": v(25.67, 3.2) * mm, "end": v(26.12, 2.8) * mm});
            skLineSegment(sketch, "E679", {"start": v(26.12, 2.8) * mm, "end": v(26.36, 2.85) * mm});
            skLineSegment(sketch, "E680", {"start": v(26.36, 2.85) * mm, "end": v(26.46, 3.43) * mm});
            skLineSegment(sketch, "E681", {"start": v(26.46, 3.43) * mm, "end": v(26.99, 3.79) * mm});
            skLineSegment(sketch, "E682", {"start": v(26.99, 3.79) * mm, "end": v(27.18, 3.55) * mm});
            skLineSegment(sketch, "E683", {"start": v(27.18, 3.55) * mm, "end": v(27.89, 3.51) * mm});
            skLineSegment(sketch, "E684", {"start": v(27.89, 3.51) * mm, "end": v(27.94, 4.31) * mm});
            skLineSegment(sketch, "E685", {"start": v(27.94, 4.31) * mm, "end": v(29.18, 5.35) * mm});
            skLineSegment(sketch, "E686", {"start": v(29.18, 5.35) * mm, "end": v(29.2, 6.1) * mm});
            skLineSegment(sketch, "E687", {"start": v(29.2, 6.1) * mm, "end": v(29.7, 6.07) * mm});
            skLineSegment(sketch, "E688", {"start": v(29.7, 6.07) * mm, "end": v(30.68, 6.64) * mm});
            skLineSegment(sketch, "E689", {"start": v(30.68, 6.64) * mm, "end": v(30.66, 6.97) * mm});
            skLineSegment(sketch, "E690", {"start": v(30.66, 6.97) * mm, "end": v(30.3, 7.25) * mm});
            skLineSegment(sketch, "E691", {"start": v(30.3, 7.25) * mm, "end": v(30.5, 7.53) * mm});
            skLineSegment(sketch, "E692", {"start": v(33.55, -6.29) * mm, "end": v(33.46, -5.44) * mm});
            skLineSegment(sketch, "E693", {"start": v(33.46, -5.44) * mm, "end": v(34.26, -5.2) * mm});
            skLineSegment(sketch, "E694", {"start": v(34.26, -5.2) * mm, "end": v(34.22, -4.72) * mm});
            skLineSegment(sketch, "E695", {"start": v(34.22, -4.72) * mm, "end": v(34.92, -4.13) * mm});
            skLineSegment(sketch, "E696", {"start": v(34.92, -4.13) * mm, "end": v(35.63, -4.1) * mm});
            skLineSegment(sketch, "E697", {"start": v(35.63, -4.1) * mm, "end": v(36.14, -3.47) * mm});
            skLineSegment(sketch, "E698", {"start": v(36.14, -3.47) * mm, "end": v(36.92, -3.08) * mm});
            skLineSegment(sketch, "E699", {"start": v(36.92, -3.08) * mm, "end": v(36.96, -2.6) * mm});
            skLineSegment(sketch, "E700", {"start": v(36.96, -2.6) * mm, "end": v(37.66, -1.98) * mm});
            skLineSegment(sketch, "E701", {"start": v(37.66, -1.98) * mm, "end": v(37.82, -2.22) * mm});
            skLineSegment(sketch, "E702", {"start": v(37.82, -2.22) * mm, "end": v(38.13, -2.26) * mm});
            skLineSegment(sketch, "E703", {"start": v(38.13, -2.26) * mm, "end": v(38.44, -1.55) * mm});
            skLineSegment(sketch, "E704", {"start": v(38.44, -1.55) * mm, "end": v(39.11, -1.55) * mm});
            skLineSegment(sketch, "E705", {"start": v(39.11, -1.55) * mm, "end": v(39.34, -1) * mm});
            skLineSegment(sketch, "E706", {"start": v(39.34, -1) * mm, "end": v(39.81, -0.7) * mm});
            skLineSegment(sketch, "E707", {"start": v(39.81, -0.7) * mm, "end": v(39.87, 0.08) * mm});
            skLineSegment(sketch, "E708", {"start": v(34.84, -0.58) * mm, "end": v(36.5, 0.57) * mm});
            skLineSegment(sketch, "E709", {"start": v(36.5, 0.57) * mm, "end": v(36.48, 0.96) * mm});
            skLineSegment(sketch, "E710", {"start": v(36.48, 0.96) * mm, "end": v(38.55, 3.17) * mm});
            skLineSegment(sketch, "E711", {"start": v(38.55, 3.17) * mm, "end": v(37.25, 4.33) * mm});
            skLineSegment(sketch, "E712", {"start": v(37.25, 4.33) * mm, "end": v(37.17, 4.72) * mm});
            skLineSegment(sketch, "E713", {"start": v(37.17, 4.72) * mm, "end": v(36.7, 6.02) * mm});
            skLineSegment(sketch, "E714", {"start": v(36.7, 6.02) * mm, "end": v(35.84, 6.55) * mm});
            skLineSegment(sketch, "E715", {"start": v(35.84, 6.55) * mm, "end": v(35.62, 7.07) * mm});
            skLineSegment(sketch, "E716", {"start": v(35.62, 7.07) * mm, "end": v(34.76, 6.38) * mm});
            skLineSegment(sketch, "E717", {"start": v(34.76, 6.38) * mm, "end": v(34.54, 6.6) * mm});
            skLineSegment(sketch, "E718", {"start": v(34.54, 6.6) * mm, "end": v(34.1, 6.68) * mm});
            skLineSegment(sketch, "E719", {"start": v(34.1, 6.68) * mm, "end": v(33.6, 6.38) * mm});
            skLineSegment(sketch, "E720", {"start": v(33.6, 6.38) * mm, "end": v(33.19, 6.77) * mm});
            skLineSegment(sketch, "E721", {"start": v(33.19, 6.77) * mm, "end": v(32.3, 6.8) * mm});
            skLineSegment(sketch, "E722", {"start": v(32.3, 6.8) * mm, "end": v(31.89, 7.49) * mm});
            skLineSegment(sketch, "E723", {"start": v(31.89, 7.49) * mm, "end": v(31.55, 7.65) * mm});
            skLineSegment(sketch, "E724", {"start": v(31.55, 7.65) * mm, "end": v(30.5, 7.53) * mm});
            skLineSegment(sketch, "E725", {"start": v(53.33, 13.6) * mm, "end": v(53.93, 14.01) * mm});
            skLineSegment(sketch, "E726", {"start": v(53.93, 14.01) * mm, "end": v(54.72, 14.31) * mm});
            skLineSegment(sketch, "E727", {"start": v(54.72, 14.31) * mm, "end": v(55.68, 15.62) * mm});
            skLineSegment(sketch, "E728", {"start": v(55.68, 15.62) * mm, "end": v(54.81, 16.36) * mm});
            skLineSegment(sketch, "E729", {"start": v(54.81, 16.36) * mm, "end": v(54.63, 16.8) * mm});
            skLineSegment(sketch, "E730", {"start": v(54.63, 16.8) * mm, "end": v(54.26, 16.78) * mm});
            skLineSegment(sketch, "E731", {"start": v(54.26, 16.78) * mm, "end": v(54.07, 17.43) * mm});
            skLineSegment(sketch, "E732", {"start": v(54.07, 17.43) * mm, "end": v(54.42, 17.57) * mm});
            skLineSegment(sketch, "E733", {"start": v(54.42, 17.57) * mm, "end": v(54.4, 17.94) * mm});
            skLineSegment(sketch, "E734", {"start": v(54.4, 17.94) * mm, "end": v(54.14, 18.13) * mm});
            skLineSegment(sketch, "E735", {"start": v(54.14, 18.13) * mm, "end": v(54.51, 18.8) * mm});
            skLineSegment(sketch, "E736", {"start": v(54.51, 18.8) * mm, "end": v(54.6, 19.36) * mm});
            skLineSegment(sketch, "E737", {"start": v(54.6, 19.36) * mm, "end": v(54.9, 19.66) * mm});
            skLineSegment(sketch, "E738", {"start": v(54.22, 14.12) * mm, "end": v(54.1, 13.3) * mm});
            skLineSegment(sketch, "E739", {"start": v(54.1, 13.3) * mm, "end": v(54.54, 12.78) * mm});
            skLineSegment(sketch, "E740", {"start": v(54.54, 12.78) * mm, "end": v(55.45, 12.3) * mm});
            skLineSegment(sketch, "E741", {"start": v(55.45, 12.3) * mm, "end": v(56.12, 12.2) * mm});
            skLineSegment(sketch, "E742", {"start": v(56.12, 12.2) * mm, "end": v(56.11, 11.9) * mm});
            skLineSegment(sketch, "E743", {"start": v(56.11, 11.9) * mm, "end": v(56.01, 11.83) * mm});
            skLineSegment(sketch, "E744", {"start": v(56.01, 11.83) * mm, "end": v(56.02, 11.38) * mm});
            skLineSegment(sketch, "E745", {"start": v(56.02, 11.38) * mm, "end": v(56.48, 11.7) * mm});
            skLineSegment(sketch, "E746", {"start": v(56.48, 11.7) * mm, "end": v(56.6, 12.4) * mm});
            skLineSegment(sketch, "E747", {"start": v(56.6, 12.4) * mm, "end": v(57.2, 13.4) * mm});
            skLineSegment(sketch, "E748", {"start": v(57.2, 13.4) * mm, "end": v(57.63, 14.43) * mm});
            skLineSegment(sketch, "E749", {"start": v(57.63, 14.43) * mm, "end": v(57.58, 15.22) * mm});
            skLineSegment(sketch, "E750", {"start": v(57.58, 15.22) * mm, "end": v(57.58, 16.72) * mm});
            skLineSegment(sketch, "E751", {"start": v(57.58, 16.72) * mm, "end": v(57.34, 17.13) * mm});
            skLineSegment(sketch, "E752", {"start": v(57.34, 17.13) * mm, "end": v(56.79, 16.94) * mm});
            skLineSegment(sketch, "E753", {"start": v(56.79, 16.94) * mm, "end": v(56.69, 17.09) * mm});
            skLineSegment(sketch, "E754", {"start": v(56.69, 17.09) * mm, "end": v(57.13, 17.45) * mm});
            skLineSegment(sketch, "E755", {"start": v(57.13, 17.45) * mm, "end": v(57.2, 17.71) * mm});
            skLineSegment(sketch, "E756", {"start": v(36.7, 6.02) * mm, "end": v(37.18, 6.2) * mm});
            skLineSegment(sketch, "E757", {"start": v(37.18, 6.2) * mm, "end": v(37.28, 6.71) * mm});
            skLineSegment(sketch, "E758", {"start": v(37.28, 6.71) * mm, "end": v(37.5, 6.8) * mm});
            skLineSegment(sketch, "E759", {"start": v(37.5, 6.8) * mm, "end": v(37.6, 8.18) * mm});
            skLineSegment(sketch, "E760", {"start": v(37.6, 8.18) * mm, "end": v(37.92, 8.26) * mm});
            skLineSegment(sketch, "E761", {"start": v(37.92, 8.26) * mm, "end": v(38.18, 7.9) * mm});
            skLineSegment(sketch, "E762", {"start": v(38.18, 7.9) * mm, "end": v(38.45, 8.05) * mm});
            skLineSegment(sketch, "E763", {"start": v(38.45, 8.05) * mm, "end": v(38.47, 8.24) * mm});
            skLineSegment(sketch, "E764", {"start": v(38.47, 8.24) * mm, "end": v(38.23, 8.63) * mm});
            skLineSegment(sketch, "E765", {"start": v(38.23, 8.63) * mm, "end": v(39.08, 9.86) * mm});
            skLineSegment(sketch, "E766", {"start": v(39.08, 9.86) * mm, "end": v(39.31, 9.75) * mm});
            skLineSegment(sketch, "E767", {"start": v(39.31, 9.75) * mm, "end": v(40.52, 11.06) * mm});
            skLineSegment(sketch, "E768", {"start": v(40.52, 11.06) * mm, "end": v(40.64, 13.5) * mm});
            skLineSegment(sketch, "E769", {"start": v(40.64, 13.5) * mm, "end": v(40.41, 14.1) * mm});
            skLineSegment(sketch, "E770", {"start": v(40.41, 14.1) * mm, "end": v(40.84, 14.34) * mm});
            skLineSegment(sketch, "E771", {"start": v(32.84, 16.98) * mm, "end": v(33.74, 16.63) * mm});
            skLineSegment(sketch, "E772", {"start": v(33.74, 16.63) * mm, "end": v(34.56, 16.67) * mm});
            skLineSegment(sketch, "E773", {"start": v(34.56, 16.67) * mm, "end": v(35.14, 16.22) * mm});
            skLineSegment(sketch, "E774", {"start": v(35.14, 16.22) * mm, "end": v(35.47, 16.29) * mm});
            skLineSegment(sketch, "E775", {"start": v(35.47, 16.29) * mm, "end": v(36.33, 16.68) * mm});
            skLineSegment(sketch, "E776", {"start": v(36.33, 16.68) * mm, "end": v(37.3, 16.84) * mm});
            skLineSegment(sketch, "E777", {"start": v(37.3, 16.84) * mm, "end": v(38.43, 18) * mm});
            skLineSegment(sketch, "E778", {"start": v(38.43, 18) * mm, "end": v(40.12, 18.98) * mm});
            skLineSegment(sketch, "E779", {"start": v(12.91, 21.3) * mm, "end": v(12.73, 22.47) * mm});
            skLineSegment(sketch, "E780", {"start": v(12.73, 22.47) * mm, "end": v(12.55, 22.88) * mm});
            skLineSegment(sketch, "E781", {"start": v(12.55, 22.88) * mm, "end": v(11.48, 23.44) * mm});
            skLineSegment(sketch, "E782", {"start": v(11.48, 23.44) * mm, "end": v(10.87, 24.42) * mm});
            skLineSegment(sketch, "E783", {"start": v(10.87, 24.42) * mm, "end": v(10.15, 24.49) * mm});
            skLineSegment(sketch, "E784", {"start": v(10.15, 24.49) * mm, "end": v(9.97, 25.02) * mm});
            skLineSegment(sketch, "E785", {"start": v(9.97, 25.02) * mm, "end": v(9.6, 25) * mm});
            skLineSegment(sketch, "E786", {"start": v(9.6, 25) * mm, "end": v(9.15, 25.37) * mm});
            skLineSegment(sketch, "E787", {"start": v(9.15, 25.37) * mm, "end": v(8.99, 27.14) * mm});
            skLineSegment(sketch, "E788", {"start": v(8.99, 27.14) * mm, "end": v(9.22, 27.49) * mm});
            skLineSegment(sketch, "E789", {"start": v(9.22, 27.49) * mm, "end": v(9.15, 28.1) * mm});
            skLineSegment(sketch, "E790", {"start": v(9.15, 28.1) * mm, "end": v(8.66, 28.4) * mm});
            skLineSegment(sketch, "E791", {"start": v(8.66, 28.4) * mm, "end": v(9.03, 29.4) * mm});
            skLineSegment(sketch, "E792", {"start": v(9.03, 29.4) * mm, "end": v(10.04, 30.12) * mm});
            skLineSegment(sketch, "E793", {"start": v(10.04, 30.12) * mm, "end": v(10.04, 31.93) * mm});
            skLineSegment(sketch, "E794", {"start": v(10.04, 31.93) * mm, "end": v(10.44, 32.27) * mm});
            skLineSegment(sketch, "E795", {"start": v(14.55, 32.02) * mm, "end": v(15.13, 31.1) * mm});
            skLineSegment(sketch, "E796", {"start": v(15.13, 31.1) * mm, "end": v(16.1, 31) * mm});
            skLineSegment(sketch, "E797", {"start": v(16.1, 31) * mm, "end": v(17.73, 30.58) * mm});
            skLineSegment(sketch, "E798", {"start": v(17.73, 30.58) * mm, "end": v(18.1, 30.33) * mm});
            skLineSegment(sketch, "E799", {"start": v(18.1, 30.33) * mm, "end": v(20.07, 30) * mm});
            skLineSegment(sketch, "E800", {"start": v(20.07, 30) * mm, "end": v(20.2, 29.6) * mm});
            skLineSegment(sketch, "E801", {"start": v(20.2, 29.6) * mm, "end": v(20.78, 29.43) * mm});
            skLineSegment(sketch, "E802", {"start": v(20.78, 29.43) * mm, "end": v(20.95, 27.92) * mm});
            skLineSegment(sketch, "E803", {"start": v(20.95, 27.92) * mm, "end": v(21.44, 27.46) * mm});
            skLineSegment(sketch, "E804", {"start": v(22.18, 32.3) * mm, "end": v(22.37, 32.44) * mm});
            skLineSegment(sketch, "E805", {"start": v(22.37, 32.44) * mm, "end": v(22.77, 32.14) * mm});
            skLineSegment(sketch, "E806", {"start": v(22.77, 32.14) * mm, "end": v(23.1, 32.35) * mm});
            skLineSegment(sketch, "E807", {"start": v(23.1, 32.35) * mm, "end": v(23.32, 32.25) * mm});
            skLineSegment(sketch, "E808", {"start": v(23.32, 32.25) * mm, "end": v(24.17, 33.01) * mm});
            skLineSegment(sketch, "E809", {"start": v(24.17, 33.01) * mm, "end": v(24.75, 33.17) * mm});
            skLineSegment(sketch, "E810", {"start": v(24.75, 33.17) * mm, "end": v(25.62, 33.23) * mm});
            skLineSegment(sketch, "E811", {"start": v(25.62, 33.23) * mm, "end": v(26.72, 33.69) * mm});
            skLineSegment(sketch, "E812", {"start": v(26.72, 33.69) * mm, "end": v(26.99, 33.64) * mm});
            skLineSegment(sketch, "E813", {"start": v(26.99, 33.64) * mm, "end": v(26.96, 32.82) * mm});
            skLineSegment(sketch, "E814", {"start": v(26.96, 32.82) * mm, "end": v(27.59, 32.63) * mm});
            skLineSegment(sketch, "E815", {"start": v(27.59, 32.63) * mm, "end": v(28.8, 32.98) * mm});
            skLineSegment(sketch, "E816", {"start": v(28.8, 32.98) * mm, "end": v(28.93, 33.15) * mm});
            skLineSegment(sketch, "E817", {"start": v(28.93, 33.15) * mm, "end": v(29.16, 33.06) * mm});
            skLineSegment(sketch, "E818", {"start": v(29.16, 33.06) * mm, "end": v(29.16, 32.05) * mm});
            skLineSegment(sketch, "E819", {"start": v(29.16, 32.05) * mm, "end": v(29.9, 31.28) * mm});
            skLineSegment(sketch, "E820", {"start": v(29.9, 31.28) * mm, "end": v(29.26, 31.3) * mm});
            skLineSegment(sketch, "E821", {"start": v(29.26, 31.3) * mm, "end": v(28.97, 31.2) * mm});
            skLineSegment(sketch, "E822", {"start": v(28.97, 31.2) * mm, "end": v(28.5, 31.25) * mm});
            skLineSegment(sketch, "E823", {"start": v(28.5, 31.25) * mm, "end": v(28.06, 31) * mm});
            skLineSegment(sketch, "E824", {"start": v(28.06, 31) * mm, "end": v(27.05, 31.17) * mm});
            skLineSegment(sketch, "E825", {"start": v(27.05, 31.17) * mm, "end": v(26.06, 31.17) * mm});
            skLineSegment(sketch, "E826", {"start": v(26.06, 31.17) * mm, "end": v(25.8, 30.77) * mm});
            skLineSegment(sketch, "E827", {"start": v(25.8, 30.77) * mm, "end": v(24.36, 30.62) * mm});
            skLineSegment(sketch, "E828", {"start": v(24.36, 30.62) * mm, "end": v(24.06, 30.02) * mm});
            skLineSegment(sketch, "E829", {"start": v(24.06, 30.02) * mm, "end": v(23.93, 29.94) * mm});
            skLineSegment(sketch, "E830", {"start": v(23.93, 29.94) * mm, "end": v(23.57, 30.16) * mm});
            skLineSegment(sketch, "E831", {"start": v(23.57, 30.16) * mm, "end": v(22.86, 29.83) * mm});
            skLineSegment(sketch, "E832", {"start": v(22.86, 29.83) * mm, "end": v(22.55, 30.08) * mm});
            skLineSegment(sketch, "E833", {"start": v(22.55, 30.08) * mm, "end": v(22.47, 30.06) * mm});
            skLineSegment(sketch, "E834", {"start": v(22.47, 30.06) * mm, "end": v(21.44, 27.46) * mm});
            skLineSegment(sketch, "E835", {"start": v(21.44, 27.46) * mm, "end": v(20.47, 25.89) * mm});
            skLineSegment(sketch, "E836", {"start": v(20.47, 25.89) * mm, "end": v(20.51, 25.56) * mm});
            skLineSegment(sketch, "E837", {"start": v(20.51, 25.56) * mm, "end": v(20.77, 25.48) * mm});
            skLineSegment(sketch, "E838", {"start": v(20.77, 25.48) * mm, "end": v(20.86, 25.86) * mm});
            skLineSegment(sketch, "E839", {"start": v(20.86, 25.86) * mm, "end": v(21.57, 26.46) * mm});
            skLineSegment(sketch, "E840", {"start": v(21.57, 26.46) * mm, "end": v(22.7, 28.16) * mm});
            skLineSegment(sketch, "E841", {"start": v(22.7, 28.16) * mm, "end": v(22.83, 27.75) * mm});
            skLineSegment(sketch, "E842", {"start": v(22.83, 27.75) * mm, "end": v(21.88, 25.81) * mm});
            skLineSegment(sketch, "E843", {"start": v(21.88, 25.81) * mm, "end": v(21.73, 24.88) * mm});
            skLineSegment(sketch, "E844", {"start": v(21.73, 24.88) * mm, "end": v(21.85, 24.74) * mm});
            skLineSegment(sketch, "E845", {"start": v(21.85, 24.74) * mm, "end": v(21.9, 24.38) * mm});
            skLineSegment(sketch, "E846", {"start": v(21.9, 24.38) * mm, "end": v(21.44, 23.75) * mm});
            skLineSegment(sketch, "E847", {"start": v(21.44, 23.75) * mm, "end": v(21.66, 22.5) * mm});
            skLineSegment(sketch, "E848", {"start": v(21.66, 22.5) * mm, "end": v(21.18, 21.16) * mm});
            skLineSegment(sketch, "E849", {"start": v(21.18, 21.16) * mm, "end": v(21.36, 20.6) * mm});
            skLineSegment(sketch, "E850", {"start": v(21.36, 20.6) * mm, "end": v(21.43, 19.78) * mm});
            skLineSegment(sketch, "E851", {"start": v(21.43, 19.78) * mm, "end": v(21.7, 19.18) * mm});
            skLineSegment(sketch, "E852", {"start": v(21.7, 19.18) * mm, "end": v(21.55, 18.48) * mm});
            skLineSegment(sketch, "E853", {"start": v(63.1, 27.05) * mm, "end": v(63.32, 27.85) * mm});
            skLineSegment(sketch, "E854", {"start": v(63.32, 27.85) * mm, "end": v(62.9, 28.01) * mm});
            skLineSegment(sketch, "E855", {"start": v(62.9, 28.01) * mm, "end": v(62.88, 28.48) * mm});
            skLineSegment(sketch, "E856", {"start": v(62.88, 28.48) * mm, "end": v(62.32, 28.63) * mm});
            skLineSegment(sketch, "E857", {"start": v(62.32, 28.63) * mm, "end": v(60.3, 34.89) * mm});
            skLineSegment(sketch, "E858", {"start": v(60.3, 34.89) * mm, "end": v(60.2, 34.53) * mm});
            skLineSegment(sketch, "E859", {"start": v(60.2, 34.53) * mm, "end": v(59.92, 34.78) * mm});
            skLineSegment(sketch, "E860", {"start": v(59.92, 34.78) * mm, "end": v(59.76, 34.72) * mm});
            skLineSegment(sketch, "E861", {"start": v(59.76, 34.72) * mm, "end": v(59.47, 33.7) * mm});
            skLineSegment(sketch, "E862", {"start": v(60.3, 34.89) * mm, "end": v(60.5, 34.95) * mm});
            skLineSegment(sketch, "E863", {"start": v(60.5, 34.95) * mm, "end": v(61.03, 34.87) * mm});
            skLineSegment(sketch, "E864", {"start": v(61.03, 34.87) * mm, "end": v(61.15, 36.2) * mm});
            skLineSegment(sketch, "E865", {"start": v(61.15, 36.2) * mm, "end": v(61.78, 37.64) * mm});
            skLineSegment(sketch, "E866", {"start": v(61.78, 37.64) * mm, "end": v(61.47, 37.96) * mm});
            skLineSegment(sketch, "E867", {"start": v(61.47, 37.96) * mm, "end": v(61.47, 38.88) * mm});
            skLineSegment(sketch, "E868", {"start": v(61.47, 38.88) * mm, "end": v(61.73, 39.34) * mm});
            skLineSegment(sketch, "E869", {"start": v(61.73, 39.34) * mm, "end": v(61.73, 40.54) * mm});
            skLineSegment(sketch, "E870", {"start": v(61.73, 40.54) * mm, "end": v(62.67, 43.1) * mm});
            skLineSegment(sketch, "E871", {"start": v(62.67, 43.1) * mm, "end": v(62.9, 43.12) * mm});
            skLineSegment(sketch, "E872", {"start": v(62.9, 43.12) * mm, "end": v(63.19, 42.55) * mm});
            skLineSegment(sketch, "E873", {"start": v(63.19, 42.55) * mm, "end": v(63.69, 42.46) * mm});
            skLineSegment(sketch, "E874", {"start": v(63.69, 42.46) * mm, "end": v(63.89, 42.64) * mm});
            skLineSegment(sketch, "E875", {"start": v(63.89, 42.64) * mm, "end": v(63.85, 42.87) * mm});
            skLineSegment(sketch, "E876", {"start": v(63.85, 42.87) * mm, "end": v(64.73, 43.48) * mm});
            skLineSegment(sketch, "E877", {"start": v(64.73, 43.48) * mm, "end": v(66.06, 43) * mm});
            skLineSegment(sketch, "E878", {"start": v(66.06, 43) * mm, "end": v(67.47, 38.31) * mm});
            skLineSegment(sketch, "E879", {"start": v(67.47, 38.31) * mm, "end": v(68.33, 38.33) * mm});
            skLineSegment(sketch, "E880", {"start": v(68.33, 38.33) * mm, "end": v(68.5, 38.15) * mm});
            skLineSegment(sketch, "E881", {"start": v(68.5, 38.15) * mm, "end": v(68.46, 37.33) * mm});
            skLineSegment(sketch, "E882", {"start": v(68.46, 37.33) * mm, "end": v(68.94, 36.92) * mm});
            skLineSegment(sketch, "E883", {"start": v(68.94, 36.92) * mm, "end": v(69.21, 36.9) * mm});
            skLineSegment(sketch, "E884", {"start": v(69.21, 36.9) * mm, "end": v(69.27, 37.17) * mm});
            skLineSegment(sketch, "E885", {"start": v(69.27, 37.17) * mm, "end": v(69.63, 37.2) * mm});
            skLineSegment(sketch, "E886", {"start": v(69.63, 37.2) * mm, "end": v(70.25, 36.29) * mm});
            skLineSegment(sketch, "E887", {"start": v(70.25, 36.29) * mm, "end": v(69.9, 35.3) * mm});
            skLineSegment(sketch, "E888", {"start": v(69.9, 35.3) * mm, "end": v(69.64, 35.3) * mm});
            skLineSegment(sketch, "E889", {"start": v(69.64, 35.3) * mm, "end": v(68.32, 33.85) * mm});
            skLineSegment(sketch, "E890", {"start": v(68.32, 33.85) * mm, "end": v(68.08, 34) * mm});
            skLineSegment(sketch, "E891", {"start": v(68.08, 34) * mm, "end": v(67.96, 34.24) * mm});
            skLineSegment(sketch, "E892", {"start": v(67.96, 34.24) * mm, "end": v(67.64, 34.22) * mm});
            skLineSegment(sketch, "E893", {"start": v(67.64, 34.22) * mm, "end": v(67.55, 34) * mm});
            skLineSegment(sketch, "E894", {"start": v(67.55, 34) * mm, "end": v(67.12, 33.52) * mm});
            skLineSegment(sketch, "E895", {"start": v(67.12, 33.52) * mm, "end": v(67.2, 33.28) * mm});
            skLineSegment(sketch, "E896", {"start": v(67.2, 33.28) * mm, "end": v(67.18, 32.81) * mm});
            skLineSegment(sketch, "E897", {"start": v(67.18, 32.81) * mm, "end": v(66.88, 32.84) * mm});
            skLineSegment(sketch, "E898", {"start": v(66.88, 32.84) * mm, "end": v(66.8, 33.19) * mm});
            skLineSegment(sketch, "E899", {"start": v(66.53, 33.2) * mm, "end": v(66.25, 33.69) * mm});
            skLineSegment(sketch, "E900", {"start": v(66.25, 33.69) * mm, "end": v(65.98, 33.55) * mm});
            skLineSegment(sketch, "E901", {"start": v(65.98, 33.55) * mm, "end": v(66.14, 33.28) * mm});
            skLineSegment(sketch, "E902", {"start": v(66.14, 33.28) * mm, "end": v(66.1, 32.68) * mm});
            skLineSegment(sketch, "E903", {"start": v(66.1, 32.68) * mm, "end": v(66.11, 32.2) * mm});
            skLineSegment(sketch, "E904", {"start": v(66.11, 32.2) * mm, "end": v(65.88, 31.8) * mm});
            skLineSegment(sketch, "E905", {"start": v(65.88, 31.8) * mm, "end": v(65.6, 31.77) * mm});
            skLineSegment(sketch, "E906", {"start": v(65.6, 31.77) * mm, "end": v(65.43, 31.74) * mm});
            skLineSegment(sketch, "E907", {"start": v(65.43, 31.74) * mm, "end": v(65.43, 31.3) * mm});
            skLineSegment(sketch, "E908", {"start": v(65.43, 31.3) * mm, "end": v(64.38, 30.74) * mm});
            skLineSegment(sketch, "E909", {"start": v(64.38, 30.74) * mm, "end": v(64.06, 30.9) * mm});
            skLineSegment(sketch, "E910", {"start": v(64.06, 30.9) * mm, "end": v(63.64, 30.4) * mm});
            skLineSegment(sketch, "E911", {"start": v(63.64, 30.4) * mm, "end": v(63.76, 29.87) * mm});
            skLineSegment(sketch, "E912", {"start": v(63.76, 29.87) * mm, "end": v(63.6, 29.73) * mm});
            skLineSegment(sketch, "E913", {"start": v(63.6, 29.73) * mm, "end": v(63.32, 27.85) * mm});
            skLineSegment(sketch, "E914", {"start": v(66.53, 33.2) * mm, "end": v(66.8, 33.19) * mm});
            skLineSegment(sketch, "E915", {"start": v(43.95, 11.85) * mm, "end": v(44.28, 10.06) * mm});
            skLineSegment(sketch, "E916", {"start": v(44.28, 10.06) * mm, "end": v(45, 11.06) * mm});
            skLineSegment(sketch, "E917", {"start": v(45, 11.06) * mm, "end": v(45.48, 10.96) * mm});
            skLineSegment(sketch, "E918", {"start": v(45.48, 10.96) * mm, "end": v(45.95, 11.6) * mm});
            skLineSegment(sketch, "E919", {"start": v(45.95, 11.6) * mm, "end": v(46.27, 11.5) * mm});
            skLineSegment(sketch, "E920", {"start": v(46.27, 11.5) * mm, "end": v(46.54, 11.59) * mm});
            skLineSegment(sketch, "E921", {"start": v(32.84, 16.98) * mm, "end": v(33.3, 18.19) * mm});
            skLineSegment(sketch, "E922", {"start": v(33.3, 18.19) * mm, "end": v(33.42, 19.04) * mm});
            skLineSegment(sketch, "E923", {"start": v(33.42, 19.04) * mm, "end": v(33.87, 19.45) * mm});
            skLineSegment(sketch, "E924", {"start": v(33.87, 19.45) * mm, "end": v(34.03, 20.03) * mm});
            skLineSegment(sketch, "E925", {"start": v(34.03, 20.03) * mm, "end": v(34.45, 20.61) * mm});
            skLineSegment(sketch, "E926", {"start": v(34.45, 20.61) * mm, "end": v(34.67, 21.5) * mm});
            skLineSegment(sketch, "E927", {"start": v(34.67, 21.5) * mm, "end": v(34.53, 22.33) * mm});
            skLineSegment(sketch, "E928", {"start": v(34.53, 22.33) * mm, "end": v(34.12, 23.63) * mm});
            skLineSegment(sketch, "E929", {"start": v(34.12, 23.63) * mm, "end": v(33.9, 24.54) * mm});
            skLineSegment(sketch, "E930", {"start": v(33.9, 24.54) * mm, "end": v(33.18, 25.29) * mm});
            skLineSegment(sketch, "E931", {"start": v(33.18, 25.29) * mm, "end": v(32.35, 24.82) * mm});
            skLineSegment(sketch, "E932", {"start": v(32.35, 24.82) * mm, "end": v(32.04, 23.9) * mm});
            skLineSegment(sketch, "E933", {"start": v(32.04, 23.9) * mm, "end": v(31.52, 23.38) * mm});
            skLineSegment(sketch, "E934", {"start": v(31.52, 23.38) * mm, "end": v(30.77, 23.66) * mm});
            skLineSegment(sketch, "E935", {"start": v(30.77, 23.66) * mm, "end": v(30.9, 24.57) * mm});
            skLineSegment(sketch, "E936", {"start": v(30.9, 24.57) * mm, "end": v(31.49, 24.74) * mm});
            skLineSegment(sketch, "E937", {"start": v(31.49, 24.74) * mm, "end": v(31.6, 25.68) * mm});
            skLineSegment(sketch, "E938", {"start": v(31.6, 25.68) * mm, "end": v(32.01, 25.87) * mm});
            skLineSegment(sketch, "E939", {"start": v(32.01, 25.87) * mm, "end": v(31.96, 27.42) * mm});
            skLineSegment(sketch, "E940", {"start": v(31.96, 27.42) * mm, "end": v(31.4, 27.94) * mm});
            skLineSegment(sketch, "E941", {"start": v(31.4, 27.94) * mm, "end": v(31.35, 28.2) * mm});
            skLineSegment(sketch, "E942", {"start": v(31.35, 28.2) * mm, "end": v(31.49, 28.44) * mm});
            skLineSegment(sketch, "E943", {"start": v(31.49, 28.44) * mm, "end": v(31.74, 28.39) * mm});
            skLineSegment(sketch, "E944", {"start": v(31.74, 28.39) * mm, "end": v(31.8, 28.58) * mm});
            skLineSegment(sketch, "E945", {"start": v(31.8, 28.58) * mm, "end": v(31.21, 29.36) * mm});
            skLineSegment(sketch, "E946", {"start": v(31.21, 29.36) * mm, "end": v(30.57, 29.41) * mm});
            skLineSegment(sketch, "E947", {"start": v(30.57, 29.41) * mm, "end": v(29.36, 30.08) * mm});
            skLineSegment(sketch, "E948", {"start": v(29.36, 30.08) * mm, "end": v(28.86, 30.13) * mm});
            skLineSegment(sketch, "E949", {"start": v(28.86, 30.13) * mm, "end": v(28.64, 30) * mm});
            skLineSegment(sketch, "E950", {"start": v(28.64, 30) * mm, "end": v(28.14, 30.4) * mm});
            skLineSegment(sketch, "E951", {"start": v(28.14, 30.4) * mm, "end": v(27.17, 29.88) * mm});
            skLineSegment(sketch, "E952", {"start": v(27.17, 29.88) * mm, "end": v(27.23, 29.3) * mm});
            skLineSegment(sketch, "E953", {"start": v(27.23, 29.3) * mm, "end": v(27.59, 29.22) * mm});
            skLineSegment(sketch, "E954", {"start": v(27.59, 29.22) * mm, "end": v(27.8, 28.97) * mm});
            skLineSegment(sketch, "E955", {"start": v(27.8, 28.97) * mm, "end": v(27.45, 28.8) * mm});
            skLineSegment(sketch, "E956", {"start": v(27.45, 28.8) * mm, "end": v(27.14, 28.86) * mm});
            skLineSegment(sketch, "E957", {"start": v(27.14, 28.86) * mm, "end": v(26.81, 28.47) * mm});
            skLineSegment(sketch, "E958", {"start": v(26.81, 28.47) * mm, "end": v(26.9, 27.17) * mm});
            skLineSegment(sketch, "E959", {"start": v(26.9, 27.17) * mm, "end": v(26.23, 26.73) * mm});
            skLineSegment(sketch, "E960", {"start": v(26.23, 26.73) * mm, "end": v(26.1, 27.42) * mm});
            skLineSegment(sketch, "E961", {"start": v(26.1, 27.42) * mm, "end": v(26.5, 28.14) * mm});
            skLineSegment(sketch, "E962", {"start": v(26.5, 28.14) * mm, "end": v(26.34, 28.3) * mm});
            skLineSegment(sketch, "E963", {"start": v(26.34, 28.3) * mm, "end": v(26.04, 28.2) * mm});
            skLineSegment(sketch, "E964", {"start": v(26.04, 28.2) * mm, "end": v(25.87, 27.64) * mm});
            skLineSegment(sketch, "E965", {"start": v(25.87, 27.64) * mm, "end": v(25.2, 27.11) * mm});
            skLineSegment(sketch, "E966", {"start": v(25.2, 27.11) * mm, "end": v(25.23, 26.9) * mm});
            skLineSegment(sketch, "E967", {"start": v(25.23, 26.9) * mm, "end": v(25.2, 26.42) * mm});
            skLineSegment(sketch, "E968", {"start": v(25.2, 26.42) * mm, "end": v(24.82, 26.4) * mm});
            skLineSegment(sketch, "E969", {"start": v(24.82, 26.4) * mm, "end": v(24.96, 25.76) * mm});
            skLineSegment(sketch, "E970", {"start": v(24.96, 25.76) * mm, "end": v(24.54, 24.35) * mm});
            skLineSegment(sketch, "E971", {"start": v(24.54, 24.35) * mm, "end": v(24.7, 23.27) * mm});
            skLineSegment(sketch, "E972", {"start": v(24.7, 23.27) * mm, "end": v(24.38, 22.47) * mm});
            skLineSegment(sketch, "E973", {"start": v(24.38, 22.47) * mm, "end": v(25.7, 19.81) * mm});
            skLineSegment(sketch, "E974", {"start": v(25.7, 19.81) * mm, "end": v(25.18, 17.46) * mm});
            skLineSegment(sketch, "E975", {"start": v(25.18, 17.46) * mm, "end": v(24.96, 16.8) * mm});
            skLineSegment(sketch, "E976", {"start": v(24.96, 16.8) * mm, "end": v(24.38, 16.11) * mm});
            skLineSegment(sketch, "E977", {"start": v(46.54, 11.59) * mm, "end": v(47.4, 12.2) * mm});
            skLineSegment(sketch, "E978", {"start": v(47.4, 12.2) * mm, "end": v(48.7, 11.38) * mm});
            skLineSegment(sketch, "E979", {"start": v(48.7, 11.38) * mm, "end": v(48.61, 10.57) * mm});
            skLineSegment(sketch, "E980", {"start": v(48.61, 10.57) * mm, "end": v(47.13, 11.25) * mm});
            skLineSegment(sketch, "E981", {"start": v(47.13, 11.25) * mm, "end": v(47, 10.32) * mm});
            skLineSegment(sketch, "E982", {"start": v(47, 10.32) * mm, "end": v(46.52, 9.46) * mm});
            skLineSegment(sketch, "E983", {"start": v(46.52, 9.46) * mm, "end": v(46.1, 9.14) * mm});
            skLineSegment(sketch, "E984", {"start": v(46.1, 9.14) * mm, "end": v(46.06, 8.79) * mm});
            skLineSegment(sketch, "E985", {"start": v(46.06, 8.79) * mm, "end": v(45.47, 8.67) * mm});
            skLineSegment(sketch, "E986", {"start": v(45.47, 8.67) * mm, "end": v(45.35, 7.43) * mm});
            skLineSegment(sketch, "E987", {"start": v(45.35, 7.43) * mm, "end": v(44.45, 7.86) * mm});
            skLineSegment(sketch, "E988", {"start": v(44.45, 7.86) * mm, "end": v(44.12, 7.84) * mm});
            skLineSegment(sketch, "E989", {"start": v(38.55, 3.17) * mm, "end": v(39.34, 2.43) * mm});
            skLineSegment(sketch, "E990", {"start": v(39.34, 2.43) * mm, "end": v(39.96, 2.29) * mm});
            skLineSegment(sketch, "E991", {"start": v(39.96, 2.29) * mm, "end": v(40.35, 2.8) * mm});
            skLineSegment(sketch, "E992", {"start": v(40.35, 2.8) * mm, "end": v(40.52, 2.53) * mm});
            skLineSegment(sketch, "E993", {"start": v(40.52, 2.53) * mm, "end": v(41.4, 2.65) * mm});
            skLineSegment(sketch, "E994", {"start": v(41.4, 2.65) * mm, "end": v(41.6, 3.4) * mm});
            skLineSegment(sketch, "E995", {"start": v(41.6, 3.4) * mm, "end": v(42.05, 3.3) * mm});
            skLineSegment(sketch, "E996", {"start": v(42.05, 3.3) * mm, "end": v(42.54, 3.63) * mm});
            skLineSegment(sketch, "E997", {"start": v(42.54, 3.63) * mm, "end": v(42.86, 3.58) * mm});
            skLineSegment(sketch, "E998", {"start": v(42.86, 3.58) * mm, "end": v(43.15, 4.23) * mm});
            skLineSegment(sketch, "E999", {"start": v(43.15, 4.23) * mm, "end": v(42.93, 4.48) * mm});
            skLineSegment(sketch, "E1000", {"start": v(42.93, 4.48) * mm, "end": v(44.14, 7.12) * mm});
            skLineSegment(sketch, "E1001", {"start": v(44.14, 7.12) * mm, "end": v(44.12, 7.84) * mm});
            skLineSegment(sketch, "E1002", {"start": v(54.1, 13.3) * mm, "end": v(53.92, 13.4) * mm});
            skLineSegment(sketch, "E1003", {"start": v(53.92, 13.4) * mm, "end": v(53.85, 13.15) * mm});
            skLineSegment(sketch, "E1004", {"start": v(53.85, 13.15) * mm, "end": v(54.24, 12.62) * mm});
            skLineSegment(sketch, "E1005", {"start": v(54.24, 12.62) * mm, "end": v(54.55, 12.52) * mm});
            skLineSegment(sketch, "E1006", {"start": v(54.55, 12.52) * mm, "end": v(55.14, 11.2) * mm});
            skLineSegment(sketch, "E1007", {"start": v(55.14, 11.2) * mm, "end": v(55.69, 10.8) * mm});
            skLineSegment(sketch, "E1008", {"start": v(55.69, 10.8) * mm, "end": v(55.86, 10.88) * mm});
            skLineSegment(sketch, "E1009", {"start": v(55.86, 10.88) * mm, "end": v(56.17, 9.83) * mm});
            skLineSegment(sketch, "E1010", {"start": v(56.17, 9.83) * mm, "end": v(56.18, 8.86) * mm});
            skLineSegment(sketch, "E1011", {"start": v(56.18, 8.86) * mm, "end": v(55.84, 7.69) * mm});
            skLineSegment(sketch, "E1012", {"start": v(55.84, 7.69) * mm, "end": v(55.39, 7.06) * mm});
            skLineSegment(sketch, "E1013", {"start": v(55.39, 7.06) * mm, "end": v(55.37, 5.83) * mm});
            skLineSegment(sketch, "E1014", {"start": v(55.37, 5.83) * mm, "end": v(54.98, 4.75) * mm});
            skLineSegment(sketch, "E1015", {"start": v(54.98, 4.75) * mm, "end": v(54.74, 4.75) * mm});
            skLineSegment(sketch, "E1016", {"start": v(54.74, 4.75) * mm, "end": v(54.55, 5.13) * mm});
            skLineSegment(sketch, "E1017", {"start": v(54.55, 5.13) * mm, "end": v(54.53, 6.32) * mm});
            skLineSegment(sketch, "E1018", {"start": v(54.53, 6.32) * mm, "end": v(54.94, 7.04) * mm});
            skLineSegment(sketch, "E1019", {"start": v(54.94, 7.04) * mm, "end": v(54.96, 7.77) * mm});
            skLineSegment(sketch, "E1020", {"start": v(54.96, 7.77) * mm, "end": v(54.69, 7.73) * mm});
            skLineSegment(sketch, "E1021", {"start": v(54.69, 7.73) * mm, "end": v(54.16, 8.65) * mm});
            skLineSegment(sketch, "E1022", {"start": v(54.16, 8.65) * mm, "end": v(54.04, 8.5) * mm});
            skLineSegment(sketch, "E1023", {"start": v(54.04, 8.5) * mm, "end": v(53.22, 8.51) * mm});
            skLineSegment(sketch, "E1024", {"start": v(53.22, 8.51) * mm, "end": v(52.94, 9.02) * mm});
            skLineSegment(sketch, "E1025", {"start": v(52.94, 9.02) * mm, "end": v(52.89, 9.55) * mm});
            skLineSegment(sketch, "E1026", {"start": v(52.89, 9.55) * mm, "end": v(53.22, 9.74) * mm});
            skLineSegment(sketch, "E1027", {"start": v(53.22, 9.74) * mm, "end": v(52.92, 10.13) * mm});
            skLineSegment(sketch, "E1028", {"start": v(52.92, 10.13) * mm, "end": v(52.73, 9.8) * mm});
            skLineSegment(sketch, "E1029", {"start": v(52.73, 9.8) * mm, "end": v(52.63, 10.27) * mm});
            skLineSegment(sketch, "E1030", {"start": v(52.63, 10.27) * mm, "end": v(53, 10.55) * mm});
            skLineSegment(sketch, "E1031", {"start": v(53, 10.55) * mm, "end": v(52.94, 11.3) * mm});
            skLineSegment(sketch, "E1032", {"start": v(52.94, 11.3) * mm, "end": v(52.61, 11.29) * mm});
            skLineSegment(sketch, "E1033", {"start": v(52.61, 11.29) * mm, "end": v(52.67, 11.84) * mm});
            skLineSegment(sketch, "E1034", {"start": v(52.67, 11.84) * mm, "end": v(53.1, 12.29) * mm});
            skLineSegment(sketch, "E1035", {"start": v(53.1, 12.29) * mm, "end": v(52.92, 12.52) * mm});
            skLineSegment(sketch, "E1036", {"start": v(52.92, 12.52) * mm, "end": v(52.38, 12.05) * mm});
            skLineSegment(sketch, "E1037", {"start": v(52.38, 12.05) * mm, "end": v(52.02, 11.35) * mm});
            skLineSegment(sketch, "E1038", {"start": v(52.02, 11.35) * mm, "end": v(52.34, 10.86) * mm});
            skLineSegment(sketch, "E1039", {"start": v(52.34, 10.86) * mm, "end": v(52.08, 10.08) * mm});
            skLineSegment(sketch, "E1040", {"start": v(52.08, 10.08) * mm, "end": v(52.44, 9.16) * mm});
            skLineSegment(sketch, "E1041", {"start": v(52.44, 9.16) * mm, "end": v(52.75, 8.88) * mm});
            skLineSegment(sketch, "E1042", {"start": v(52.75, 8.88) * mm, "end": v(52.7, 8.63) * mm});
            skLineSegment(sketch, "E1043", {"start": v(52.7, 8.63) * mm, "end": v(52.9, 8) * mm});
            skLineSegment(sketch, "E1044", {"start": v(52.9, 8) * mm, "end": v(52.06, 8.08) * mm});
            skLineSegment(sketch, "E1045", {"start": v(52.06, 8.08) * mm, "end": v(51.42, 8.12) * mm});
            skLineSegment(sketch, "E1046", {"start": v(51.42, 8.12) * mm, "end": v(50.58, 8.28) * mm});
            skLineSegment(sketch, "E1047", {"start": v(50.58, 8.28) * mm, "end": v(50.46, 8.88) * mm});
            skLineSegment(sketch, "E1048", {"start": v(50.46, 8.88) * mm, "end": v(50.75, 9.25) * mm});
            skLineSegment(sketch, "E1049", {"start": v(50.75, 9.25) * mm, "end": v(50.8, 9.74) * mm});
            skLineSegment(sketch, "E1050", {"start": v(50.8, 9.74) * mm, "end": v(50.32, 10.33) * mm});
            skLineSegment(sketch, "E1051", {"start": v(50.32, 10.33) * mm, "end": v(49.38, 10.56) * mm});
            skLineSegment(sketch, "E1052", {"start": v(49.38, 10.56) * mm, "end": v(49.42, 11.01) * mm});
            skLineSegment(sketch, "E1053", {"start": v(49.42, 11.01) * mm, "end": v(48.7, 11.38) * mm});
            skLineSegment(sketch, "E1054", {"start": v(51.42, 8.12) * mm, "end": v(51.67, 7.85) * mm});
            skLineSegment(sketch, "E1055", {"start": v(51.67, 7.85) * mm, "end": v(52.57, 7.78) * mm});
            skLineSegment(sketch, "E1056", {"start": v(52.57, 7.78) * mm, "end": v(52.84, 7.4) * mm});
            skLineSegment(sketch, "E1057", {"start": v(52.84, 7.4) * mm, "end": v(53.34, 7.42) * mm});
            skLineSegment(sketch, "E1058", {"start": v(53.34, 7.42) * mm, "end": v(53.54, 7.17) * mm});
            skLineSegment(sketch, "E1059", {"start": v(53.54, 7.17) * mm, "end": v(53.5, 6.45) * mm});
            skLineSegment(sketch, "E1060", {"start": v(53.5, 6.45) * mm, "end": v(53.65, 6.36) * mm});
            skLineSegment(sketch, "E1061", {"start": v(53.65, 6.36) * mm, "end": v(53.65, 5.97) * mm});
            skLineSegment(sketch, "E1062", {"start": v(53.65, 5.97) * mm, "end": v(53.92, 5.61) * mm});
            skLineSegment(sketch, "E1063", {"start": v(53.92, 5.61) * mm, "end": v(53.9, 5.36) * mm});
            skLineSegment(sketch, "E1064", {"start": v(53.9, 5.36) * mm, "end": v(53.33, 5.54) * mm});
            skLineSegment(sketch, "E1065", {"start": v(53.33, 5.54) * mm, "end": v(53.33, 5.4) * mm});
            skLineSegment(sketch, "E1066", {"start": v(53.33, 5.4) * mm, "end": v(53.63, 5.18) * mm});
            skLineSegment(sketch, "E1067", {"start": v(53.63, 5.18) * mm, "end": v(53.63, 5) * mm});
            skLineSegment(sketch, "E1068", {"start": v(53.63, 5) * mm, "end": v(54.06, 4.62) * mm});
            skLineSegment(sketch, "E1069", {"start": v(54.06, 4.62) * mm, "end": v(54.15, 4.12) * mm});
            skLineSegment(sketch, "E1070", {"start": v(54.15, 4.12) * mm, "end": v(53.74, 3.98) * mm});
            skLineSegment(sketch, "E1071", {"start": v(53.74, 3.98) * mm, "end": v(53.74, 3.82) * mm});
            skLineSegment(sketch, "E1072", {"start": v(53.74, 3.82) * mm, "end": v(54.89, 4.07) * mm});
            skLineSegment(sketch, "E1073", {"start": v(54.89, 4.07) * mm, "end": v(55.38, 2.91) * mm});
            skLineSegment(sketch, "E1074", {"start": v(55.38, 2.91) * mm, "end": v(56.85, 0.52) * mm});
            skLineSegment(sketch, "E1075", {"start": v(56.85, 0.52) * mm, "end": v(56.3, 0.52) * mm});
            skLineSegment(sketch, "E1076", {"start": v(36.73, -5.84) * mm, "end": v(39.09, -4.77) * mm});
            skLineSegment(sketch, "E1077", {"start": v(39.09, -4.77) * mm, "end": v(42.72, -4.54) * mm});
            skLineSegment(sketch, "E1078", {"start": v(42.72, -4.54) * mm, "end": v(43.13, -5) * mm});
            skLineSegment(sketch, "E1079", {"start": v(43.13, -5) * mm, "end": v(43.24, -5.36) * mm});
            skLineSegment(sketch, "E1080", {"start": v(43.24, -5.36) * mm, "end": v(46.24, -5.1) * mm});
            skLineSegment(sketch, "E1081", {"start": v(46.24, -5.1) * mm, "end": v(49.84, -7.58) * mm});
            skLineSegment(sketch, "E1082", {"start": v(49.84, -7.58) * mm, "end": v(50.63, -7.35) * mm});
            skLineSegment(sketch, "E1083", {"start": v(50.63, -7.35) * mm, "end": v(51.64, -7.28) * mm});
            skLineSegment(sketch, "E1084", {"start": v(51.64, -7.28) * mm, "end": v(51.9, -5.81) * mm});
            skLineSegment(sketch, "E1085", {"start": v(51.9, -5.81) * mm, "end": v(53.55, -4.24) * mm});
            skLineSegment(sketch, "E1086", {"start": v(53.55, -4.24) * mm, "end": v(54.71, -3.75) * mm});
            skLineSegment(sketch, "E1087", {"start": v(54.71, -3.75) * mm, "end": v(55.12, -3.87) * mm});
            skLineSegment(sketch, "E1088", {"start": v(55.12, -3.87) * mm, "end": v(55.83, -2.7) * mm});
            skLineSegment(sketch, "E1089", {"start": v(55.83, -2.7) * mm, "end": v(55.35, -3) * mm});
            skLineSegment(sketch, "E1090", {"start": v(55.35, -3) * mm, "end": v(55.16, -2.74) * mm});
            skLineSegment(sketch, "E1091", {"start": v(55.16, -2.74) * mm, "end": v(54.52, -2.78) * mm});
            skLineSegment(sketch, "E1092", {"start": v(54.52, -2.78) * mm, "end": v(54.9, -1.77) * mm});
            skLineSegment(sketch, "E1093", {"start": v(54.9, -1.77) * mm, "end": v(54.49, -1.62) * mm});
            skLineSegment(sketch, "E1094", {"start": v(54.49, -1.62) * mm, "end": v(54.3, -1.2) * mm});
            skLineSegment(sketch, "E1095", {"start": v(54.3, -1.2) * mm, "end": v(55.09, -1.58) * mm});
            skLineSegment(sketch, "E1096", {"start": v(55.09, -1.58) * mm, "end": v(55.83, -1.36) * mm});
            skLineSegment(sketch, "E1097", {"start": v(55.83, -1.36) * mm, "end": v(56.13, -0.42) * mm});
            skLineSegment(sketch, "E1098", {"start": v(56.13, -0.42) * mm, "end": v(56.5, -0.23) * mm});
            skLineSegment(sketch, "E1099", {"start": v(56.5, -0.23) * mm, "end": v(56.3, 0.52) * mm});
            skLineSegment(sketch, "E1100", {"start": v(36.73, -5.85) * mm, "end": v(36.88, -6.18) * mm});
            skLineSegment(sketch, "E1101", {"start": v(36.88, -6.18) * mm, "end": v(36.43, -6.44) * mm});
            skLineSegment(sketch, "E1102", {"start": v(36.43, -6.44) * mm, "end": v(36.3, -7) * mm});
            skLineSegment(sketch, "E1103", {"start": v(36.3, -7) * mm, "end": v(37.26, -7.57) * mm});
            skLineSegment(sketch, "E1104", {"start": v(37.26, -7.57) * mm, "end": v(37.68, -7.48) * mm});
            skLineSegment(sketch, "E1105", {"start": v(37.68, -7.48) * mm, "end": v(38.75, -9.18) * mm});
            skLineSegment(sketch, "E1106", {"start": v(38.75, -9.18) * mm, "end": v(39.83, -9.8) * mm});
            skLineSegment(sketch, "E1107", {"start": v(39.83, -9.8) * mm, "end": v(40.04, -10.2) * mm});
            skLineSegment(sketch, "E1108", {"start": v(40.04, -10.2) * mm, "end": v(40.86, -10.66) * mm});
            skLineSegment(sketch, "E1109", {"start": v(40.86, -10.66) * mm, "end": v(41.51, -11.48) * mm});
            skLineSegment(sketch, "E1110", {"start": v(41.51, -11.48) * mm, "end": v(42.15, -11.8) * mm});
            skLineSegment(sketch, "E1111", {"start": v(42.15, -11.8) * mm, "end": v(42.81, -13.48) * mm});
            skLineSegment(sketch, "E1112", {"start": v(42.81, -13.48) * mm, "end": v(43.13, -13.48) * mm});
            skLineSegment(sketch, "E1113", {"start": v(43.13, -13.48) * mm, "end": v(43.63, -14.1) * mm});
            skLineSegment(sketch, "E1114", {"start": v(43.63, -14.1) * mm, "end": v(43.79, -14.73) * mm});
            skLineSegment(sketch, "E1115", {"start": v(43.79, -14.73) * mm, "end": v(44.63, -15.1) * mm});
            skLineSegment(sketch, "E1116", {"start": v(44.63, -15.1) * mm, "end": v(44.54, -14.77) * mm});
            skLineSegment(sketch, "E1117", {"start": v(44.54, -14.77) * mm, "end": v(45.63, -13.82) * mm});
            skLineSegment(sketch, "E1118", {"start": v(45.63, -13.82) * mm, "end": v(45.4, -13.32) * mm});
            skLineSegment(sketch, "E1119", {"start": v(45.4, -13.32) * mm, "end": v(45.97, -13.3) * mm});
            skLineSegment(sketch, "E1120", {"start": v(45.97, -13.3) * mm, "end": v(47.84, -11.16) * mm});
            skLineSegment(sketch, "E1121", {"start": v(47.84, -11.16) * mm, "end": v(48.1, -11.04) * mm});
            skLineSegment(sketch, "E1122", {"start": v(48.1, -11.04) * mm, "end": v(48.7, -10.36) * mm});
            skLineSegment(sketch, "E1123", {"start": v(48.7, -10.36) * mm, "end": v(48.74, -9.43) * mm});
            skLineSegment(sketch, "E1124", {"start": v(48.74, -9.43) * mm, "end": v(49.45, -8.13) * mm});
            skLineSegment(sketch, "E1125", {"start": v(49.45, -8.13) * mm, "end": v(49.84, -7.58) * mm});
            skLineSegment(sketch, "E1126", {"start": v(44.63, -15.1) * mm, "end": v(44.15, -16.2) * mm});
            skLineSegment(sketch, "E1127", {"start": v(44.15, -16.2) * mm, "end": v(44.18, -16.46) * mm});
            skLineSegment(sketch, "E1128", {"start": v(44.18, -16.46) * mm, "end": v(43.97, -17.16) * mm});
            skLineSegment(sketch, "E1129", {"start": v(43.97, -17.16) * mm, "end": v(43.5, -18.59) * mm});
            skLineSegment(sketch, "E1130", {"start": v(43.5, -18.59) * mm, "end": v(43.6, -19.73) * mm});
            skLineSegment(sketch, "E1131", {"start": v(43.6, -19.73) * mm, "end": v(42.08, -19.61) * mm});
            skLineSegment(sketch, "E1132", {"start": v(42.08, -19.61) * mm, "end": v(41.84, -19.87) * mm});
            skLineSegment(sketch, "E1133", {"start": v(41.84, -19.87) * mm, "end": v(41.96, -20.43) * mm});
            skLineSegment(sketch, "E1134", {"start": v(41.96, -20.43) * mm, "end": v(42.02, -21.13) * mm});
            skLineSegment(sketch, "E1135", {"start": v(42.02, -21.13) * mm, "end": v(41.58, -21.1) * mm});
            skLineSegment(sketch, "E1136", {"start": v(41.58, -21.1) * mm, "end": v(41.52, -20.57) * mm});
            skLineSegment(sketch, "E1137", {"start": v(40.45, -25.52) * mm, "end": v(41.24, -26.63) * mm});
            skLineSegment(sketch, "E1138", {"start": v(41.24, -26.63) * mm, "end": v(41.2, -28.29) * mm});
            skLineSegment(sketch, "E1139", {"start": v(41.2, -28.29) * mm, "end": v(40.88, -28.72) * mm});
            skLineSegment(sketch, "E1140", {"start": v(40.88, -28.72) * mm, "end": v(41.47, -30.5) * mm});
            skLineSegment(sketch, "E1141", {"start": v(41.47, -30.5) * mm, "end": v(41.75, -30.03) * mm});
            skLineSegment(sketch, "E1142", {"start": v(41.75, -30.03) * mm, "end": v(41.28, -29.63) * mm});
            skLineSegment(sketch, "E1143", {"start": v(41.28, -29.63) * mm, "end": v(42.38, -29.67) * mm});
            skLineSegment(sketch, "E1144", {"start": v(42.38, -29.67) * mm, "end": v(41.51, -31.01) * mm});
            skLineSegment(sketch, "E1145", {"start": v(41.51, -31.01) * mm, "end": v(42.42, -32.16) * mm});
            skLineSegment(sketch, "E1146", {"start": v(42.42, -32.16) * mm, "end": v(43.05, -33.03) * mm});
            skLineSegment(sketch, "E1147", {"start": v(43.05, -33.03) * mm, "end": v(43.57, -34.33) * mm});
            skLineSegment(sketch, "E1148", {"start": v(43.57, -34.33) * mm, "end": v(43.88, -34.53) * mm});
            skLineSegment(sketch, "E1149", {"start": v(43.88, -34.53) * mm, "end": v(44.2, -34.25) * mm});
            skLineSegment(sketch, "E1150", {"start": v(44.2, -34.25) * mm, "end": v(44.75, -34.69) * mm});
            skLineSegment(sketch, "E1151", {"start": v(44.75, -34.69) * mm, "end": v(44.87, -35.2) * mm});
            skLineSegment(sketch, "E1152", {"start": v(44.87, -35.2) * mm, "end": v(45.35, -35.95) * mm});
            skLineSegment(sketch, "E1153", {"start": v(45.35, -35.95) * mm, "end": v(45.62, -35.91) * mm});
            skLineSegment(sketch, "E1154", {"start": v(45.62, -35.91) * mm, "end": v(46.14, -36) * mm});
            skLineSegment(sketch, "E1155", {"start": v(46.14, -36) * mm, "end": v(46.73, -36.47) * mm});
            skLineSegment(sketch, "E1156", {"start": v(46.73, -36.47) * mm, "end": v(47.2, -37.1) * mm});
            skLineSegment(sketch, "E1157", {"start": v(47.2, -37.1) * mm, "end": v(47.44, -38.25) * mm});
            skLineSegment(sketch, "E1158", {"start": v(47.44, -38.25) * mm, "end": v(47.72, -38.48) * mm});
            skLineSegment(sketch, "E1159", {"start": v(47.72, -38.48) * mm, "end": v(48.15, -38.32) * mm});
            skLineSegment(sketch, "E1160", {"start": v(48.15, -38.32) * mm, "end": v(48.39, -37.85) * mm});
            skLineSegment(sketch, "E1161", {"start": v(48.39, -37.85) * mm, "end": v(48.7, -37.93) * mm});
            skLineSegment(sketch, "E1162", {"start": v(48.7, -37.93) * mm, "end": v(49.22, -37.85) * mm});
            skLineSegment(sketch, "E1163", {"start": v(49.22, -37.85) * mm, "end": v(49.9, -37.38) * mm});
            skLineSegment(sketch, "E1164", {"start": v(49.9, -37.38) * mm, "end": v(49.77, -36.78) * mm});
            skLineSegment(sketch, "E1165", {"start": v(49.77, -36.78) * mm, "end": v(49.77, -36.43) * mm});
            skLineSegment(sketch, "E1166", {"start": v(49.77, -36.43) * mm, "end": v(49.65, -35.91) * mm});
            skLineSegment(sketch, "E1167", {"start": v(49.65, -35.91) * mm, "end": v(50.25, -35.48) * mm});
            skLineSegment(sketch, "E1168", {"start": v(50.25, -35.48) * mm, "end": v(50.25, -34.85) * mm});
            skLineSegment(sketch, "E1169", {"start": v(50.25, -34.85) * mm, "end": v(50.05, -32.12) * mm});
            skLineSegment(sketch, "E1170", {"start": v(50.05, -32.12) * mm, "end": v(48.35, -28.96) * mm});
            skLineSegment(sketch, "E1171", {"start": v(48.35, -28.96) * mm, "end": v(47.6, -28.45) * mm});
            skLineSegment(sketch, "E1172", {"start": v(47.6, -28.45) * mm, "end": v(47.28, -27.34) * mm});
            skLineSegment(sketch, "E1173", {"start": v(47.28, -27.34) * mm, "end": v(47.52, -26.94) * mm});
            skLineSegment(sketch, "E1174", {"start": v(47.52, -26.94) * mm, "end": v(47.24, -26.27) * mm});
            skLineSegment(sketch, "E1175", {"start": v(47.24, -26.27) * mm, "end": v(46.22, -25.29) * mm});
            skLineSegment(sketch, "E1176", {"start": v(46.22, -25.29) * mm, "end": v(44.95, -23.35) * mm});
            skLineSegment(sketch, "E1177", {"start": v(44.95, -23.35) * mm, "end": v(43.96, -21.06) * mm});
            skLineSegment(sketch, "E1178", {"start": v(43.96, -21.06) * mm, "end": v(43.6, -19.73) * mm});
            skLineSegment(sketch, "E1179", {"start": v(-48.66, -21.06) * mm, "end": v(-50.01, -20.37) * mm});
            skLineSegment(sketch, "E1180", {"start": v(-50.01, -20.37) * mm, "end": v(-50.5, -20.62) * mm});
            skLineSegment(sketch, "E1181", {"start": v(-50.5, -20.62) * mm, "end": v(-51.48, -20.19) * mm});
            skLineSegment(sketch, "E1182", {"start": v(-51.48, -20.19) * mm, "end": v(-51.6, -20.62) * mm});
            skLineSegment(sketch, "E1183", {"start": v(-51.6, -20.62) * mm, "end": v(-52.59, -19.7) * mm});
            skLineSegment(sketch, "E1184", {"start": v(-52.59, -19.7) * mm, "end": v(-53.75, -19.63) * mm});
            skLineSegment(sketch, "E1185", {"start": v(-53.75, -19.63) * mm, "end": v(-54.1, -19.46) * mm});
            skLineSegment(sketch, "E1186", {"start": v(-54.1, -19.46) * mm, "end": v(-54.12, -18.77) * mm});
            skLineSegment(sketch, "E1187", {"start": v(-54.12, -18.77) * mm, "end": v(-54.7, -18.7) * mm});
            skLineSegment(sketch, "E1188", {"start": v(-54.7, -18.7) * mm, "end": v(-54.88, -19.07) * mm});
            skLineSegment(sketch, "E1189", {"start": v(-54.88, -19.07) * mm, "end": v(-54.97, -18.65) * mm});
            skLineSegment(sketch, "E1190", {"start": v(-54.97, -18.65) * mm, "end": v(-55.97, -17.94) * mm});
            skLineSegment(sketch, "E1191", {"start": v(-55.97, -17.94) * mm, "end": v(-56.42, -18.41) * mm});
            skLineSegment(sketch, "E1192", {"start": v(-56.42, -18.41) * mm, "end": v(-57.08, -18.48) * mm});
            skLineSegment(sketch, "E1193", {"start": v(-57.08, -18.48) * mm, "end": v(-57.36, -18.33) * mm});
            skLineSegment(sketch, "E1194", {"start": v(-57.36, -18.33) * mm, "end": v(-58.45, -18.82) * mm});
            skLineSegment(sketch, "E1195", {"start": v(-58.45, -18.82) * mm, "end": v(-58.81, -18.54) * mm});
            skLineSegment(sketch, "E1196", {"start": v(-58.81, -18.54) * mm, "end": v(-59.24, -19) * mm});
            skLineSegment(sketch, "E1197", {"start": v(-59.24, -19) * mm, "end": v(-59.39, -19.46) * mm});
            skLineSegment(sketch, "E1198", {"start": v(-59.39, -19.46) * mm, "end": v(-60, -20) * mm});
            skLineSegment(sketch, "E1199", {"start": v(-60, -20) * mm, "end": v(-60.65, -20) * mm});
            skLineSegment(sketch, "E1200", {"start": v(-60.65, -20) * mm, "end": v(-60.75, -19.97) * mm});
            skLineSegment(sketch, "E1201", {"start": v(-60.75, -19.97) * mm, "end": v(-61.4, -19.84) * mm});
            skLineSegment(sketch, "E1202", {"start": v(-61.4, -19.84) * mm, "end": v(-61.86, -20.2) * mm});
            skLineSegment(sketch, "E1203", {"start": v(-61.86, -20.2) * mm, "end": v(-61.03, -21.63) * mm});
            skLineSegment(sketch, "E1204", {"start": v(-61.03, -21.63) * mm, "end": v(-61.03, -22.61) * mm});
            skLineSegment(sketch, "E1205", {"start": v(-61.03, -22.61) * mm, "end": v(-60.33, -22.93) * mm});
            skLineSegment(sketch, "E1206", {"start": v(-60.33, -22.93) * mm, "end": v(-60.58, -23.08) * mm});
            skLineSegment(sketch, "E1207", {"start": v(-60.58, -23.08) * mm, "end": v(-60.1, -24.26) * mm});
            skLineSegment(sketch, "E1208", {"start": v(-60.1, -24.26) * mm, "end": v(-60.35, -24.47) * mm});
            skLineSegment(sketch, "E1209", {"start": v(-60.35, -24.47) * mm, "end": v(-61.52, -23.96) * mm});
            skLineSegment(sketch, "E1210", {"start": v(-61.52, -23.96) * mm, "end": v(-61.24, -23.34) * mm});
            skLineSegment(sketch, "E1211", {"start": v(-61.24, -23.34) * mm, "end": v(-61.54, -23.1) * mm});
            skLineSegment(sketch, "E1212", {"start": v(-61.54, -23.1) * mm, "end": v(-62.4, -23.2) * mm});
            skLineSegment(sketch, "E1213", {"start": v(-62.4, -23.2) * mm, "end": v(-62.4, -23.47) * mm});
            skLineSegment(sketch, "E1214", {"start": v(-62.4, -23.47) * mm, "end": v(-62.57, -23.49) * mm});
            skLineSegment(sketch, "E1215", {"start": v(-62.57, -23.49) * mm, "end": v(-62.7, -23.36) * mm});
            skLineSegment(sketch, "E1216", {"start": v(-62.7, -23.36) * mm, "end": v(-63.97, -23.38) * mm});
            skLineSegment(sketch, "E1217", {"start": v(-63.97, -23.38) * mm, "end": v(-64.1, -23.64) * mm});
            skLineSegment(sketch, "E1218", {"start": v(-64.1, -23.64) * mm, "end": v(-63.59, -24.32) * mm});
            skLineSegment(sketch, "E1219", {"start": v(-63.59, -24.32) * mm, "end": v(-63.72, -25.28) * mm});
            skLineSegment(sketch, "E1220", {"start": v(-63.72, -25.28) * mm, "end": v(-63.12, -25.96) * mm});
            skLineSegment(sketch, "E1221", {"start": v(-63.12, -25.96) * mm, "end": v(-62.44, -25.92) * mm});
            skLineSegment(sketch, "E1222", {"start": v(-62.44, -25.92) * mm, "end": v(-61.63, -26.28) * mm});
            skLineSegment(sketch, "E1223", {"start": v(-61.63, -26.28) * mm, "end": v(-60.69, -26.07) * mm});
            skLineSegment(sketch, "E1224", {"start": v(-60.69, -26.07) * mm, "end": v(-60.52, -26.35) * mm});
            skLineSegment(sketch, "E1225", {"start": v(-60.52, -26.35) * mm, "end": v(-60.88, -27.7) * mm});
            skLineSegment(sketch, "E1226", {"start": v(-48.66, -21.06) * mm, "end": v(-48.66, -34.34) * mm});
            skLineSegment(sketch, "E1227", {"start": v(-48.66, -34.34) * mm, "end": v(-48.45, -34.72) * mm});
            skLineSegment(sketch, "E1228", {"start": v(-48.45, -34.72) * mm, "end": v(-48.08, -34.62) * mm});
            skLineSegment(sketch, "E1229", {"start": v(-48.08, -34.62) * mm, "end": v(-47.9, -34.62) * mm});
            skLineSegment(sketch, "E1230", {"start": v(-47.9, -34.62) * mm, "end": v(-47.6, -34.42) * mm});
            skLineSegment(sketch, "E1231", {"start": v(-47.6, -34.42) * mm, "end": v(-47.37, -34.5) * mm});
            skLineSegment(sketch, "E1232", {"start": v(-47.37, -34.5) * mm, "end": v(-47.35, -34.94) * mm});
            skLineSegment(sketch, "E1233", {"start": v(-47.35, -34.94) * mm, "end": v(-46.36, -35.85) * mm});
            skLineSegment(sketch, "E1234", {"start": v(-46.36, -35.85) * mm, "end": v(-46.13, -36.4) * mm});
            skLineSegment(sketch, "E1235", {"start": v(-46.13, -36.4) * mm, "end": v(-45.38, -36.02) * mm});
            skLineSegment(sketch, "E1236", {"start": v(-45.38, -36.02) * mm, "end": v(-45.35, -35.44) * mm});
            skLineSegment(sketch, "E1237", {"start": v(-45.35, -35.44) * mm, "end": v(-44.97, -35.24) * mm});
            skLineSegment(sketch, "E1238", {"start": v(-44.48, -35.38) * mm, "end": v(-44.28, -35.93) * mm});
            skLineSegment(sketch, "E1239", {"start": v(-44.28, -35.93) * mm, "end": v(-43.9, -35.93) * mm});
            skLineSegment(sketch, "E1240", {"start": v(-43.9, -35.93) * mm, "end": v(-43.85, -36.54) * mm});
            skLineSegment(sketch, "E1241", {"start": v(-44.97, -35.24) * mm, "end": v(-44.48, -35.38) * mm});
            skLineSegment(sketch, "E1242", {"start": v(-43.85, -36.54) * mm, "end": v(-43.28, -36.54) * mm});
            skLineSegment(sketch, "E1243", {"start": v(-43.28, -36.54) * mm, "end": v(-42.67, -37.74) * mm});
            skLineSegment(sketch, "E1244", {"start": v(-42.67, -37.74) * mm, "end": v(-41.94, -38.53) * mm});
            skLineSegment(sketch, "E1245", {"start": v(-41.94, -38.53) * mm, "end": v(-41.75, -39.2) * mm});
            skLineSegment(sketch, "E1246", {"start": v(-41.75, -39.2) * mm, "end": v(-40.1, -39.73) * mm});
            skLineSegment(sketch, "E1247", {"start": v(-40.1, -39.73) * mm, "end": v(-39.92, -40.76) * mm});
            skLineSegment(sketch, "E1248", {"start": v(-39.92, -40.76) * mm, "end": v(-40.3, -41.72) * mm});
            skLineSegment(sketch, "E1249", {"start": v(-40.3, -41.72) * mm, "end": v(-40.5, -41.6) * mm});
            skLineSegment(sketch, "E1250", {"start": v(-40.5, -41.6) * mm, "end": v(-40.64, -41.2) * mm});
            skLineSegment(sketch, "E1251", {"start": v(-40.64, -41.2) * mm, "end": v(-41.35, -40.78) * mm});
            skLineSegment(sketch, "E1252", {"start": v(-41.35, -40.78) * mm, "end": v(-41.55, -40.86) * mm});
            skLineSegment(sketch, "E1253", {"start": v(-41.55, -40.86) * mm, "end": v(-41.33, -41.18) * mm});
            skLineSegment(sketch, "E1254", {"start": v(-41.33, -41.18) * mm, "end": v(-41.33, -41.98) * mm});
            skLineSegment(sketch, "E1255", {"start": v(-41.33, -41.98) * mm, "end": v(-41.75, -41.64) * mm});
            skLineSegment(sketch, "E1256", {"start": v(-41.75, -41.64) * mm, "end": v(-42.14, -41.34) * mm});
            skLineSegment(sketch, "E1257", {"start": v(-42.14, -41.34) * mm, "end": v(-41.83, -41.93) * mm});
            skLineSegment(sketch, "E1258", {"start": v(-41.83, -41.93) * mm, "end": v(-41.96, -42.11) * mm});
            skLineSegment(sketch, "E1259", {"start": v(-41.96, -42.11) * mm, "end": v(-42.58, -41.06) * mm});
            skLineSegment(sketch, "E1260", {"start": v(-42.58, -41.06) * mm, "end": v(-42.73, -41.22) * mm});
            skLineSegment(sketch, "E1261", {"start": v(-42.62, -40.71) * mm, "end": v(-42.83, -40.53) * mm});
            skLineSegment(sketch, "E1262", {"start": v(-42.83, -40.53) * mm, "end": v(-42.83, -39.74) * mm});
            skLineSegment(sketch, "E1263", {"start": v(-42.83, -39.74) * mm, "end": v(-43.11, -40.25) * mm});
            skLineSegment(sketch, "E1264", {"start": v(-43.11, -40.25) * mm, "end": v(-43.36, -40.44) * mm});
            skLineSegment(sketch, "E1265", {"start": v(-43.36, -40.44) * mm, "end": v(-43.52, -39.2) * mm});
            skLineSegment(sketch, "E1266", {"start": v(-43.52, -39.2) * mm, "end": v(-43.7, -39.1) * mm});
            skLineSegment(sketch, "E1267", {"start": v(-43.7, -39.1) * mm, "end": v(-43.7, -40.04) * mm});
            skLineSegment(sketch, "E1268", {"start": v(-43.7, -40.04) * mm, "end": v(-44.38, -39.05) * mm});
            skLineSegment(sketch, "E1269", {"start": v(-44.38, -39.05) * mm, "end": v(-44.82, -38.97) * mm});
            skLineSegment(sketch, "E1270", {"start": v(-44.82, -38.97) * mm, "end": v(-44.84, -38.41) * mm});
            skLineSegment(sketch, "E1271", {"start": v(-44.84, -38.41) * mm, "end": v(-45.07, -37.95) * mm});
            skLineSegment(sketch, "E1272", {"start": v(-45.07, -37.95) * mm, "end": v(-45.41, -37.7) * mm});
            skLineSegment(sketch, "E1273", {"start": v(-45.41, -37.7) * mm, "end": v(-45.41, -37.42) * mm});
            skLineSegment(sketch, "E1274", {"start": v(-45.41, -37.42) * mm, "end": v(-44.97, -37.2) * mm});
            skLineSegment(sketch, "E1275", {"start": v(-44.97, -37.2) * mm, "end": v(-45.13, -37.08) * mm});
            skLineSegment(sketch, "E1276", {"start": v(-45.13, -37.08) * mm, "end": v(-45.45, -37.27) * mm});
            skLineSegment(sketch, "E1277", {"start": v(-45.45, -37.27) * mm, "end": v(-46.13, -36.77) * mm});
            skLineSegment(sketch, "E1278", {"start": v(-46.13, -36.77) * mm, "end": v(-46.3, -36.53) * mm});
            skLineSegment(sketch, "E1279", {"start": v(-46.3, -36.53) * mm, "end": v(-47.8, -35.66) * mm});
            skLineSegment(sketch, "E1280", {"start": v(-47.8, -35.66) * mm, "end": v(-47.56, -35.21) * mm});
            skLineSegment(sketch, "E1281", {"start": v(-47.56, -35.21) * mm, "end": v(-47.55, -34.76) * mm});
            skLineSegment(sketch, "E1282", {"start": v(-47.55, -34.76) * mm, "end": v(-48.2, -35.24) * mm});
            skLineSegment(sketch, "E1283", {"start": v(-48.2, -35.24) * mm, "end": v(-49.72, -34.71) * mm});
            skLineSegment(sketch, "E1284", {"start": v(-49.72, -34.71) * mm, "end": v(-50.58, -34.69) * mm});
            skLineSegment(sketch, "E1285", {"start": v(-50.58, -34.69) * mm, "end": v(-50.7, -34.8) * mm});
            skLineSegment(sketch, "E1286", {"start": v(-50.7, -34.8) * mm, "end": v(-51.62, -34.19) * mm});
            skLineSegment(sketch, "E1287", {"start": v(-51.62, -34.19) * mm, "end": v(-51.91, -34.17) * mm});
            skLineSegment(sketch, "E1288", {"start": v(-51.91, -34.17) * mm, "end": v(-52.4, -33.27) * mm});
            skLineSegment(sketch, "E1289", {"start": v(-52.4, -33.27) * mm, "end": v(-52.87, -33.26) * mm});
            skLineSegment(sketch, "E1290", {"start": v(-52.87, -33.26) * mm, "end": v(-53.55, -33.52) * mm});
            skLineSegment(sketch, "E1291", {"start": v(-53.55, -33.52) * mm, "end": v(-53.54, -34.1) * mm});
            skLineSegment(sketch, "E1292", {"start": v(-53.54, -34.1) * mm, "end": v(-53.3, -34.13) * mm});
            skLineSegment(sketch, "E1293", {"start": v(-53.3, -34.13) * mm, "end": v(-53.38, -34.46) * mm});
            skLineSegment(sketch, "E1294", {"start": v(-53.38, -34.46) * mm, "end": v(-53.62, -34.71) * mm});
            skLineSegment(sketch, "E1295", {"start": v(-53.62, -34.71) * mm, "end": v(-53.85, -34.51) * mm});
            skLineSegment(sketch, "E1296", {"start": v(-53.85, -34.51) * mm, "end": v(-54.05, -34.7) * mm});
            skLineSegment(sketch, "E1297", {"start": v(-54.05, -34.7) * mm, "end": v(-54.43, -34.4) * mm});
            skLineSegment(sketch, "E1298", {"start": v(-54.43, -34.4) * mm, "end": v(-54.94, -34.75) * mm});
            skLineSegment(sketch, "E1299", {"start": v(-54.94, -34.75) * mm, "end": v(-55.68, -35.38) * mm});
            skLineSegment(sketch, "E1300", {"start": v(-55.68, -35.38) * mm, "end": v(-56.54, -35.38) * mm});
            skLineSegment(sketch, "E1301", {"start": v(-56.54, -35.38) * mm, "end": v(-56.58, -35.08) * mm});
            skLineSegment(sketch, "E1302", {"start": v(-56.58, -35.08) * mm, "end": v(-56.01, -35) * mm});
            skLineSegment(sketch, "E1303", {"start": v(-56.01, -35) * mm, "end": v(-55.98, -34.74) * mm});
            skLineSegment(sketch, "E1304", {"start": v(-55.98, -34.74) * mm, "end": v(-56.4, -34.64) * mm});
            skLineSegment(sketch, "E1305", {"start": v(-56.4, -34.64) * mm, "end": v(-55.64, -33.18) * mm});
            skLineSegment(sketch, "E1306", {"start": v(-55.64, -33.18) * mm, "end": v(-55.17, -32.94) * mm});
            skLineSegment(sketch, "E1307", {"start": v(-55.17, -32.94) * mm, "end": v(-54.97, -33.14) * mm});
            skLineSegment(sketch, "E1308", {"start": v(-54.97, -33.14) * mm, "end": v(-54.54, -33.16) * mm});
            skLineSegment(sketch, "E1309", {"start": v(-54.54, -33.16) * mm, "end": v(-54.75, -32.7) * mm});
            skLineSegment(sketch, "E1310", {"start": v(-54.75, -32.7) * mm, "end": v(-55.27, -32.6) * mm});
            skLineSegment(sketch, "E1311", {"start": v(-55.27, -32.6) * mm, "end": v(-56.15, -33.06) * mm});
            skLineSegment(sketch, "E1312", {"start": v(-56.15, -33.06) * mm, "end": v(-56.9, -34.37) * mm});
            skLineSegment(sketch, "E1313", {"start": v(-56.9, -34.37) * mm, "end": v(-57.63, -34.63) * mm});
            skLineSegment(sketch, "E1314", {"start": v(-57.63, -34.63) * mm, "end": v(-58.1, -35.05) * mm});
            skLineSegment(sketch, "E1315", {"start": v(-58.1, -35.05) * mm, "end": v(-58.1, -35.24) * mm});
            skLineSegment(sketch, "E1316", {"start": v(-58.1, -35.24) * mm, "end": v(-57.84, -35.42) * mm});
            skLineSegment(sketch, "E1317", {"start": v(-57.84, -35.42) * mm, "end": v(-57.64, -35.75) * mm});
            skLineSegment(sketch, "E1318", {"start": v(-57.64, -35.75) * mm, "end": v(-58.03, -36.18) * mm});
            skLineSegment(sketch, "E1319", {"start": v(-58.03, -36.18) * mm, "end": v(-60.6, -37.7) * mm});
            skLineSegment(sketch, "E1320", {"start": v(-60.6, -37.7) * mm, "end": v(-62.18, -38.23) * mm});
            skLineSegment(sketch, "E1321", {"start": v(-62.18, -38.23) * mm, "end": v(-61.96, -38.46) * mm});
            skLineSegment(sketch, "E1322", {"start": v(-61.96, -38.46) * mm, "end": v(-62.27, -38.84) * mm});
            skLineSegment(sketch, "E1323", {"start": v(-62.27, -38.84) * mm, "end": v(-62.67, -38.7) * mm});
            skLineSegment(sketch, "E1324", {"start": v(-62.67, -38.7) * mm, "end": v(-63.08, -38.7) * mm});
            skLineSegment(sketch, "E1325", {"start": v(-63.08, -38.7) * mm, "end": v(-63.24, -38.94) * mm});
            skLineSegment(sketch, "E1326", {"start": v(-63.24, -38.94) * mm, "end": v(-63.35, -38.74) * mm});
            skLineSegment(sketch, "E1327", {"start": v(-63.35, -38.74) * mm, "end": v(-64.3, -39.05) * mm});
            skLineSegment(sketch, "E1328", {"start": v(-64.3, -39.05) * mm, "end": v(-64.91, -38.82) * mm});
            skLineSegment(sketch, "E1329", {"start": v(-64.91, -38.82) * mm, "end": v(-65.3, -39.14) * mm});
            skLineSegment(sketch, "E1330", {"start": v(-65.3, -39.14) * mm, "end": v(-65.84, -39.13) * mm});
            skLineSegment(sketch, "E1331", {"start": v(-65.84, -39.13) * mm, "end": v(-66.36, -39.46) * mm});
            skLineSegment(sketch, "E1332", {"start": v(-66.36, -39.46) * mm, "end": v(-67.14, -39.28) * mm});
            skLineSegment(sketch, "E1333", {"start": v(-67.14, -39.28) * mm, "end": v(-67.64, -39.49) * mm});
            skLineSegment(sketch, "E1334", {"start": v(-67.64, -39.49) * mm, "end": v(-67.96, -39.31) * mm});
            skLineSegment(sketch, "E1335", {"start": v(-67.96, -39.31) * mm, "end": v(-67.92, -38.97) * mm});
            skLineSegment(sketch, "E1336", {"start": v(-67.92, -38.97) * mm, "end": v(-67.56, -38.78) * mm});
            skLineSegment(sketch, "E1337", {"start": v(-67.56, -38.78) * mm, "end": v(-66.56, -38.9) * mm});
            skLineSegment(sketch, "E1338", {"start": v(-66.56, -38.9) * mm, "end": v(-66.12, -38.76) * mm});
            skLineSegment(sketch, "E1339", {"start": v(-66.12, -38.76) * mm, "end": v(-65.92, -38.68) * mm});
            skLineSegment(sketch, "E1340", {"start": v(-65.92, -38.68) * mm, "end": v(-65.43, -38.24) * mm});
            skLineSegment(sketch, "E1341", {"start": v(-65.43, -38.24) * mm, "end": v(-65.11, -38.2) * mm});
            skLineSegment(sketch, "E1342", {"start": v(-65.11, -38.2) * mm, "end": v(-64.7, -38.06) * mm});
            skLineSegment(sketch, "E1343", {"start": v(-64.7, -38.06) * mm, "end": v(-64.4, -38.1) * mm});
            skLineSegment(sketch, "E1344", {"start": v(-64.4, -38.1) * mm, "end": v(-64.2, -38.32) * mm});
            skLineSegment(sketch, "E1345", {"start": v(-64.2, -38.32) * mm, "end": v(-63.89, -38.3) * mm});
            skLineSegment(sketch, "E1346", {"start": v(-63.89, -38.3) * mm, "end": v(-63.47, -37.8) * mm});
            skLineSegment(sketch, "E1347", {"start": v(-63.47, -37.8) * mm, "end": v(-62.35, -37.57) * mm});
            skLineSegment(sketch, "E1348", {"start": v(-62.35, -37.57) * mm, "end": v(-62.2, -37.62) * mm});
            skLineSegment(sketch, "E1349", {"start": v(-62.2, -37.62) * mm, "end": v(-62, -37.06) * mm});
            skLineSegment(sketch, "E1350", {"start": v(-62, -37.06) * mm, "end": v(-61.31, -36.81) * mm});
            skLineSegment(sketch, "E1351", {"start": v(-61.31, -36.81) * mm, "end": v(-60.74, -35.59) * mm});
            skLineSegment(sketch, "E1352", {"start": v(-60.74, -35.59) * mm, "end": v(-60.39, -35.34) * mm});
            skLineSegment(sketch, "E1353", {"start": v(-60.39, -35.34) * mm, "end": v(-60.32, -34.86) * mm});
            skLineSegment(sketch, "E1354", {"start": v(-60.32, -34.86) * mm, "end": v(-60.94, -35.17) * mm});
            skLineSegment(sketch, "E1355", {"start": v(-60.94, -35.17) * mm, "end": v(-61.24, -34.88) * mm});
            skLineSegment(sketch, "E1356", {"start": v(-61.24, -34.88) * mm, "end": v(-61.43, -34.84) * mm});
            skLineSegment(sketch, "E1357", {"start": v(-61.43, -34.84) * mm, "end": v(-61.69, -34.94) * mm});
            skLineSegment(sketch, "E1358", {"start": v(-61.69, -34.94) * mm, "end": v(-61.72, -35.36) * mm});
            skLineSegment(sketch, "E1359", {"start": v(-61.72, -35.36) * mm, "end": v(-61.86, -35.36) * mm});
            skLineSegment(sketch, "E1360", {"start": v(-61.86, -35.36) * mm, "end": v(-62.04, -34.43) * mm});
            skLineSegment(sketch, "E1361", {"start": v(-62.04, -34.43) * mm, "end": v(-62.25, -34.6) * mm});
            skLineSegment(sketch, "E1362", {"start": v(-62.25, -34.6) * mm, "end": v(-62.4, -34.62) * mm});
            skLineSegment(sketch, "E1363", {"start": v(-62.4, -34.62) * mm, "end": v(-62.46, -34.32) * mm});
            skLineSegment(sketch, "E1364", {"start": v(-62.46, -34.32) * mm, "end": v(-63.12, -34.34) * mm});
            skLineSegment(sketch, "E1365", {"start": v(-63.12, -34.34) * mm, "end": v(-63.51, -34.52) * mm});
            skLineSegment(sketch, "E1366", {"start": v(-63.51, -34.52) * mm, "end": v(-63.91, -34.46) * mm});
            skLineSegment(sketch, "E1367", {"start": v(-63.91, -34.46) * mm, "end": v(-63.61, -34.1) * mm});
            skLineSegment(sketch, "E1368", {"start": v(-63.61, -34.1) * mm, "end": v(-63.65, -33.49) * mm});
            skLineSegment(sketch, "E1369", {"start": v(-63.65, -33.49) * mm, "end": v(-63.17, -33.4) * mm});
            skLineSegment(sketch, "E1370", {"start": v(-63.17, -33.4) * mm, "end": v(-63.35, -33.16) * mm});
            skLineSegment(sketch, "E1371", {"start": v(-63.35, -33.16) * mm, "end": v(-63.27, -32.45) * mm});
            skLineSegment(sketch, "E1372", {"start": v(-63.27, -32.45) * mm, "end": v(-63.54, -32.2) * mm});
            skLineSegment(sketch, "E1373", {"start": v(-63.54, -32.2) * mm, "end": v(-63.7, -32.46) * mm});
            skLineSegment(sketch, "E1374", {"start": v(-63.7, -32.46) * mm, "end": v(-64.57, -32.43) * mm});
            skLineSegment(sketch, "E1375", {"start": v(-64.57, -32.43) * mm, "end": v(-64.8, -32.25) * mm});
            skLineSegment(sketch, "E1376", {"start": v(-64.8, -32.25) * mm, "end": v(-64.89, -31.72) * mm});
            skLineSegment(sketch, "E1377", {"start": v(-64.89, -31.72) * mm, "end": v(-65.14, -31.18) * mm});
            skLineSegment(sketch, "E1378", {"start": v(-65.14, -31.18) * mm, "end": v(-65.2, -30.9) * mm});
            skLineSegment(sketch, "E1379", {"start": v(-65.2, -30.9) * mm, "end": v(-64.87, -30.82) * mm});
            skLineSegment(sketch, "E1380", {"start": v(-64.87, -30.82) * mm, "end": v(-64.89, -30.52) * mm});
            skLineSegment(sketch, "E1381", {"start": v(-64.89, -30.52) * mm, "end": v(-64.66, -30.37) * mm});
            skLineSegment(sketch, "E1382", {"start": v(-64.66, -30.37) * mm, "end": v(-64.8, -30.3) * mm});
            skLineSegment(sketch, "E1383", {"start": v(-64.8, -30.3) * mm, "end": v(-64.98, -30.32) * mm});
            skLineSegment(sketch, "E1384", {"start": v(-64.98, -30.32) * mm, "end": v(-65.17, -29.93) * mm});
            skLineSegment(sketch, "E1385", {"start": v(-65.17, -29.93) * mm, "end": v(-65.07, -29.07) * mm});
            skLineSegment(sketch, "E1386", {"start": v(-65.07, -29.07) * mm, "end": v(-63.95, -28.38) * mm});
            skLineSegment(sketch, "E1387", {"start": v(-63.95, -28.38) * mm, "end": v(-63.65, -27.82) * mm});
            skLineSegment(sketch, "E1388", {"start": v(-63.65, -27.82) * mm, "end": v(-63.24, -27.6) * mm});
            skLineSegment(sketch, "E1389", {"start": v(-63.24, -27.6) * mm, "end": v(-62.88, -27.68) * mm});
            skLineSegment(sketch, "E1390", {"start": v(-62.88, -27.68) * mm, "end": v(-62.76, -28.16) * mm});
            skLineSegment(sketch, "E1391", {"start": v(-62.76, -28.16) * mm, "end": v(-62.32, -28.07) * mm});
            skLineSegment(sketch, "E1392", {"start": v(-62.32, -28.07) * mm, "end": v(-61.85, -27.79) * mm});
            skLineSegment(sketch, "E1393", {"start": v(-61.85, -27.79) * mm, "end": v(-61.48, -27.98) * mm});
            skLineSegment(sketch, "E1394", {"start": v(-61.48, -27.98) * mm, "end": v(-61.25, -27.98) * mm});
            skLineSegment(sketch, "E1395", {"start": v(-61.25, -27.98) * mm, "end": v(-60.88, -27.7) * mm});
            skLineSegment(sketch, "E1396", {"start": v(-36.3, -30.87) * mm, "end": v(-36.58, -31.3) * mm});
            skLineSegment(sketch, "E1397", {"start": v(-36.58, -31.3) * mm, "end": v(-37.04, -31.31) * mm});
            skLineSegment(sketch, "E1398", {"start": v(-37.04, -31.31) * mm, "end": v(-36.78, -30.79) * mm});
            skLineSegment(sketch, "E1399", {"start": v(-36.78, -30.79) * mm, "end": v(-36.43, -30.72) * mm});
            skLineSegment(sketch, "E1400", {"start": v(-36.43, -30.72) * mm, "end": v(-36.3, -30.87) * mm});
            skLineSegment(sketch, "E1401", {"start": v(-34.57, -31.14) * mm, "end": v(-35.42, -30.73) * mm});
            skLineSegment(sketch, "E1402", {"start": v(-35.42, -30.73) * mm, "end": v(-35.36, -30.14) * mm});
            skLineSegment(sketch, "E1403", {"start": v(-35.36, -30.14) * mm, "end": v(-34.67, -29.87) * mm});
            skLineSegment(sketch, "E1404", {"start": v(-34.67, -29.87) * mm, "end": v(-34.05, -29.96) * mm});
            skLineSegment(sketch, "E1405", {"start": v(-34.05, -29.96) * mm, "end": v(-34, -30.51) * mm});
            skLineSegment(sketch, "E1406", {"start": v(-34, -30.51) * mm, "end": v(-34.12, -31.1) * mm});
            skLineSegment(sketch, "E1407", {"start": v(-34.12, -31.1) * mm, "end": v(-34.57, -31.14) * mm});
            skLineSegment(sketch, "E1408", {"start": v(-28.64, -32.95) * mm, "end": v(-29.09, -32.74) * mm});
            skLineSegment(sketch, "E1409", {"start": v(-29.09, -32.74) * mm, "end": v(-29.68, -31.58) * mm});
            skLineSegment(sketch, "E1410", {"start": v(-29.68, -31.58) * mm, "end": v(-30.65, -32.02) * mm});
            skLineSegment(sketch, "E1411", {"start": v(-30.65, -32.02) * mm, "end": v(-30.73, -32.3) * mm});
            skLineSegment(sketch, "E1412", {"start": v(-30.73, -32.3) * mm, "end": v(-30.15, -33.17) * mm});
            skLineSegment(sketch, "E1413", {"start": v(-30.15, -33.17) * mm, "end": v(-29.56, -33.05) * mm});
            skLineSegment(sketch, "E1414", {"start": v(-29.56, -33.05) * mm, "end": v(-29.36, -33.24) * mm});
            skLineSegment(sketch, "E1415", {"start": v(-29.36, -33.24) * mm, "end": v(-28.77, -33.23) * mm});
            skLineSegment(sketch, "E1416", {"start": v(-28.77, -33.23) * mm, "end": v(-28.64, -32.95) * mm});
            skLineSegment(sketch, "E1417", {"start": v(-27.4, -33.38) * mm, "end": v(-27.6, -33.68) * mm});
            skLineSegment(sketch, "E1418", {"start": v(-27.6, -33.68) * mm, "end": v(-26.98, -33.9) * mm});
            skLineSegment(sketch, "E1419", {"start": v(-26.98, -33.9) * mm, "end": v(-26.07, -34) * mm});
            skLineSegment(sketch, "E1420", {"start": v(-26.07, -34) * mm, "end": v(-25.66, -33.77) * mm});
            skLineSegment(sketch, "E1421", {"start": v(-25.66, -33.77) * mm, "end": v(-25.66, -33.52) * mm});
            skLineSegment(sketch, "E1422", {"start": v(-25.66, -33.52) * mm, "end": v(-26.6, -33.5) * mm});
            skLineSegment(sketch, "E1423", {"start": v(-26.6, -33.5) * mm, "end": v(-26.7, -33.63) * mm});
            skLineSegment(sketch, "E1424", {"start": v(-26.7, -33.63) * mm, "end": v(-27.04, -33.43) * mm});
            skLineSegment(sketch, "E1425", {"start": v(-27.04, -33.43) * mm, "end": v(-27.4, -33.38) * mm});
            skLineSegment(sketch, "E1426", {"start": v(-26.13, -34.33) * mm, "end": v(-25.96, -34.55) * mm});
            skLineSegment(sketch, "E1427", {"start": v(-25.96, -34.55) * mm, "end": v(-25.95, -34.85) * mm});
            skLineSegment(sketch, "E1428", {"start": v(-25.95, -34.85) * mm, "end": v(-26.5, -35.1) * mm});
            skLineSegment(sketch, "E1429", {"start": v(-26.5, -35.1) * mm, "end": v(-26.79, -34.4) * mm});
            skLineSegment(sketch, "E1430", {"start": v(-26.79, -34.4) * mm, "end": v(-26.13, -34.33) * mm});
            skLineSegment(sketch, "E1431", {"start": v(-25.71, -34.3) * mm, "end": v(-25.3, -33.81) * mm});
            skLineSegment(sketch, "E1432", {"start": v(-25.3, -33.81) * mm, "end": v(-24.63, -34.2) * mm});
            skLineSegment(sketch, "E1433", {"start": v(-24.63, -34.2) * mm, "end": v(-24.05, -34.37) * mm});
            skLineSegment(sketch, "E1434", {"start": v(-24.05, -34.37) * mm, "end": v(-23.25, -34.8) * mm});
            skLineSegment(sketch, "E1435", {"start": v(-23.25, -34.8) * mm, "end": v(-23.26, -35.07) * mm});
            skLineSegment(sketch, "E1436", {"start": v(-23.26, -35.07) * mm, "end": v(-24.52, -35.57) * mm});
            skLineSegment(sketch, "E1437", {"start": v(-24.52, -35.57) * mm, "end": v(-24.88, -35.36) * mm});
            skLineSegment(sketch, "E1438", {"start": v(-24.88, -35.36) * mm, "end": v(-25.71, -34.3) * mm});
            skLineSegment(sketch, "E1439", {"start": v(-20.96, -39.88) * mm, "end": v(-20.82, -39.99) * mm});
            skLineSegment(sketch, "E1440", {"start": v(-20.82, -39.99) * mm, "end": v(-20.11, -39.83) * mm});
            skLineSegment(sketch, "E1441", {"start": v(-20.11, -39.83) * mm, "end": v(-19.43, -39.2) * mm});
            skLineSegment(sketch, "E1442", {"start": v(-19.43, -39.2) * mm, "end": v(-20.15, -38.7) * mm});
            skLineSegment(sketch, "E1443", {"start": v(-20.15, -38.7) * mm, "end": v(-20.56, -37.72) * mm});
            skLineSegment(sketch, "E1444", {"start": v(-20.56, -37.72) * mm, "end": v(-22.83, -36.57) * mm});
            skLineSegment(sketch, "E1445", {"start": v(-22.83, -36.57) * mm, "end": v(-23.12, -36.7) * mm});
            skLineSegment(sketch, "E1446", {"start": v(-23.12, -36.7) * mm, "end": v(-22.81, -37.3) * mm});
            skLineSegment(sketch, "E1447", {"start": v(-22.81, -37.3) * mm, "end": v(-23.12, -37.84) * mm});
            skLineSegment(sketch, "E1448", {"start": v(-23.12, -37.84) * mm, "end": v(-23.5, -37.98) * mm});
            skLineSegment(sketch, "E1449", {"start": v(-23.5, -37.98) * mm, "end": v(-23.6, -38.44) * mm});
            skLineSegment(sketch, "E1450", {"start": v(-23.6, -38.44) * mm, "end": v(-23.22, -38.75) * mm});
            skLineSegment(sketch, "E1451", {"start": v(-23.22, -38.75) * mm, "end": v(-22.98, -39.68) * mm});
            skLineSegment(sketch, "E1452", {"start": v(-22.98, -39.68) * mm, "end": v(-23.05, -40.7) * mm});
            skLineSegment(sketch, "E1453", {"start": v(-23.05, -40.7) * mm, "end": v(-22.33, -41.2) * mm});
            skLineSegment(sketch, "E1454", {"start": v(-22.33, -41.2) * mm, "end": v(-21.44, -40.18) * mm});
            skLineSegment(sketch, "E1455", {"start": v(-21.44, -40.18) * mm, "end": v(-20.96, -39.88) * mm});
            skLineSegment(sketch, "E1456", {"start": v(36.73, -5.84) * mm, "end": v(36.73, -5.85) * mm});
            skLineSegment(sketch, "E1457", {"start": v(-15.04, -0.88) * mm, "end": v(-14.4, 9.48) * mm});
            skLineSegment(sketch, "E1458", {"start": v(-17.55, -0.7) * mm, "end": v(-15.04, -0.88) * mm});
            skLineSegment(sketch, "E1459", {"start": v(-15.04, -0.88) * mm, "end": v(0.22, -1.36) * mm});
            skLineSegment(sketch, "E1460", {"start": v(0.22, -1.36) * mm, "end": v(4.89, -1.39) * mm});
            skLineSegment(sketch, "E1461", {"start": v(-32.02, 14.71) * mm, "end": v(-24.92, 13.81) * mm});
            skLineSegment(sketch, "E1462", {"start": v(-24.92, 13.81) * mm, "end": v(-19.27, 13.3) * mm});
            skLineSegment(sketch, "E1463", {"start": v(-19.27, 13.3) * mm, "end": v(-14.18, 12.88) * mm});
            skLineSegment(sketch, "E1464", {"start": v(-18.72, 20.1) * mm, "end": v(-19.27, 13.3) * mm});
            skLineSegment(sketch, "E1465", {"start": v(-18.72, 20.1) * mm, "end": v(-18.19, 26.91) * mm});
            skLineSegment(sketch, "E1466", {"start": v(-42.62, -40.71) * mm, "end": v(-42.73, -41.22) * mm});
            skLineSegment(sketch, "E1467", {"start": v(-33.75, 1.04) * mm, "end": v(-17.55, -0.7) * mm});
            skLineSegment(sketch, "E1468", {"start": v(-47.13, 3.28) * mm, "end": v(-33.75, 1.04) * mm});
            skLineSegment(sketch, "E1469", {"start": v(-33.75, 1.04) * mm, "end": v(-36.49, -18.16) * mm});
            skLineSegment(sketch, "E1470", {"start": v(-33.75, 1.04) * mm, "end": v(-33.8, 1.05) * mm});
            skLineSegment(sketch, "E1471", {"start": v(-33.8, 1.05) * mm, "end": v(-36.54, -18.16) * mm});
            skSolve(sketch);
        }
        {
            var Q0;
            Q0=makeQuery(id+"F2.imprint","IMPRINT",FACE,{"disambiguationData":[TD([[makeQuery(id+"F2.imprint","IMPRINT",EDGE,{"derivedFrom":sQuery(id+"F2.wireOp",EDGE,"E11")}),1.0]])]});
            extrude(context, id + "F3", {"entities" : qUnion([Q0]), "operationType" : NewBodyOperationType.ADD, "depth" : 4.23 * mm, "offsetDistance" : 25.4 * mm});
        }
        {
            var Q0;
            {var subQ0=sQuery(id+"F2.wireOp",EDGE,"E18");Q0=makeQuery(id+"F2.imprint","IMPRINT",FACE,{"disambiguationData":[TD([[makeQuery(id+"F2.imprint","IMPRINT",EDGE,{"derivedFrom":subQ0}),1.0]])]});}
            extrude(context, id + "F4", {"entities" : qUnion([Q0]), "operationType" : NewBodyOperationType.ADD, "depth" : 30.8 * mm, "offsetDistance" : 25.4 * mm});
        }
        {
            var Q0;
            Q0=makeQuery(id+"F2.imprint","IMPRINT",FACE,{"disambiguationData":[TD([[makeQuery(id+"F2.imprint","IMPRINT",EDGE,{"derivedFrom":sQuery(id+"F2.wireOp",EDGE,"E1")}),-1.0]])]});
            extrude(context, id + "F5", {"entities" : qUnion([Q0]), "operationType" : NewBodyOperationType.ADD, "depth" : 21.25 * mm, "offsetDistance" : 25.4 * mm});
        }
        {
            var Q0;
            Q0=makeQuery(id+"F2.imprint","IMPRINT",FACE,{"disambiguationData":[TD([[makeQuery(id+"F2.imprint","IMPRINT",EDGE,{"derivedFrom":sQuery(id+"F2.wireOp",EDGE,"E44")}),1.0]])]});
            extrude(context, id + "F6", {"entities" : qUnion([Q0]), "operationType" : NewBodyOperationType.ADD, "depth" : 15.79 * mm, "offsetDistance" : 25.4 * mm});
        }
        {
            var Q0;
            Q0=makeQuery(id+"F2.imprint","IMPRINT",FACE,{"disambiguationData":[TD([[makeQuery(id+"F2.imprint","IMPRINT",EDGE,{"derivedFrom":sQuery(id+"F2.wireOp",EDGE,"E317")}),1.0]])]});
            extrude(context, id + "F7", {"entities" : qUnion([Q0]), "operationType" : NewBodyOperationType.ADD, "depth" : 15.71 * mm, "offsetDistance" : 25.4 * mm});
        }
        {
            var Q0;
            Q0=makeQuery(id+"F2.imprint","IMPRINT",FACE,{"disambiguationData":[TD([[makeQuery(id+"F2.imprint","IMPRINT",EDGE,{"derivedFrom":sQuery(id+"F2.wireOp",EDGE,"E40")}),-1.0]])]});
            extrude(context, id + "F8", {"entities" : qUnion([Q0]), "operationType" : NewBodyOperationType.ADD, "depth" : 128821350 / 8029672510.6 * mm, "offsetDistance" : 25.4 * mm});
        }
        {
            var Q0;
            Q0=makeQuery(id+"F2.imprint","IMPRINT",FACE,{"disambiguationData":[TD([[makeQuery(id+"F2.imprint","IMPRINT",EDGE,{"derivedFrom":sQuery(id+"F2.wireOp",EDGE,"E44")}),-1.0]])]});
            extrude(context, id + "F9", {"entities" : qUnion([Q0]), "operationType" : NewBodyOperationType.ADD, "depth" : 10.26 * mm, "offsetDistance" : 25.4 * mm});
        }
        {
            var Q0;
            {var subQ0=sQuery(id+"F2.wireOp",EDGE,"E43");Q0=makeQuery(id+"F2.imprint","IMPRINT",FACE,{"disambiguationData":[TD([[makeQuery(id+"F2.imprint","IMPRINT",EDGE,{"derivedFrom":subQ0}),-1.0]])]});}
            extrude(context, id + "F10", {"entities" : qUnion([Q0]), "operationType" : NewBodyOperationType.ADD, "depth" : 9.3 * mm, "offsetDistance" : 25.4 * mm});
        }
        {
            var Q0;
            {var subQ4=sQuery(id+"F2.wireOp",EDGE,"E307");Q0=makeQuery(id+"F2.imprint","IMPRINT",FACE,{"disambiguationData":[TD([[makeQuery(id+"F2.imprint","IMPRINT",EDGE,{"derivedFrom":subQ4}),1.0]])]});}
            extrude(context, id + "F11", {"entities" : qUnion([Q0]), "operationType" : NewBodyOperationType.ADD, "depth" : 8.03 * mm, "offsetDistance" : 25.4 * mm});
        }
        {
            var Q0;
            {var subQ0=sQuery(id+"F2.wireOp",EDGE,"E41");Q0=makeQuery(id+"F2.imprint","IMPRINT",FACE,{"disambiguationData":[TD([[makeQuery(id+"F2.imprint","IMPRINT",EDGE,{"derivedFrom":subQ0}),1.0]])]});}
            var Q1;
            Q1=makeQuery(id+"F2.imprint","IMPRINT",FACE,{"disambiguationData":[TD([[makeQuery(id+"F2.imprint","IMPRINT",EDGE,{"derivedFrom":sQuery(id+"F2.wireOp",EDGE,"E577")}),-1.0]])]});
            extrude(context, id + "F12", {"entities" : qUnion([Q0, Q1]), "operationType" : NewBodyOperationType.ADD, "depth" : 7.95 * mm, "offsetDistance" : 25.4 * mm});
        }
        {
            var Q0;
            {var subQ4=sQuery(id+"F2.wireOp",EDGE,"E692");Q0=makeQuery(id+"F2.imprint","IMPRINT",FACE,{"disambiguationData":[TD([[makeQuery(id+"F2.imprint","IMPRINT",EDGE,{"derivedFrom":subQ4}),-1.0]])]});}
            extrude(context, id + "F13", {"entities" : qUnion([Q0]), "operationType" : NewBodyOperationType.ADD, "depth" : 7.9 * mm, "offsetDistance" : 25.4 * mm});
        }
        {
            var Q0;
            Q0=makeQuery(id+"F2.imprint","IMPRINT",FACE,{"disambiguationData":[TD([[makeQuery(id+"F2.imprint","IMPRINT",EDGE,{"derivedFrom":sQuery(id+"F2.wireOp",EDGE,"E186")}),-1.0]])]});
            extrude(context, id + "F14", {"entities" : qUnion([Q0]), "operationType" : NewBodyOperationType.ADD, "depth" : 7.15 * mm, "offsetDistance" : 25.4 * mm});
        }
        {
            var Q0;
            {var subQ0=sQuery(id+"F2.wireOp",EDGE,"E708");Q0=makeQuery(id+"F2.imprint","IMPRINT",FACE,{"disambiguationData":[TD([[makeQuery(id+"F2.imprint","IMPRINT",EDGE,{"derivedFrom":subQ0}),-1.0]])]});}
            extrude(context, id + "F15", {"entities" : qUnion([Q0]), "operationType" : NewBodyOperationType.ADD, "depth" : 6.64 * mm, "offsetDistance" : 25.4 * mm});
        }
        {
            var Q0;
            {var subQ0=sQuery(id+"F2.wireOp",EDGE,"E49");Q0=makeQuery(id+"F2.imprint","IMPRINT",FACE,{"disambiguationData":[TD([[makeQuery(id+"F2.imprint","IMPRINT",EDGE,{"derivedFrom":subQ0}),-1.0]])]});}
            extrude(context, id + "F16", {"entities" : qUnion([Q0]), "operationType" : NewBodyOperationType.ADD, "depth" : 5.6 * mm, "offsetDistance" : 25.4 * mm});
        }
        {
            var Q0;
            {var subQ3=sQuery(id+"F2.wireOp",EDGE,"E201");Q0=makeQuery(id+"F2.imprint","IMPRINT",FACE,{"disambiguationData":[TD([[makeQuery(id+"F2.imprint","IMPRINT",EDGE,{"derivedFrom":subQ3}),-1.0]])]});}
            extrude(context, id + "F17", {"entities" : qUnion([Q0]), "operationType" : NewBodyOperationType.ADD, "depth" : 5.38 * mm, "offsetDistance" : 25.4 * mm});
        }
        {
            var Q0;
            {var subQ3=sQuery(id+"F2.wireOp",EDGE,"E41");Q0=makeQuery(id+"F2.imprint","IMPRINT",FACE,{"disambiguationData":[TD([[makeQuery(id+"F2.imprint","IMPRINT",EDGE,{"derivedFrom":subQ3}),-1.0]])]});}
            extrude(context, id + "F18", {"entities" : qUnion([Q0]), "operationType" : NewBodyOperationType.ADD, "depth" : 5.28 * mm, "offsetDistance" : 25.4 * mm});
        }
        {
            var Q0;
            Q0=makeQuery(id+"F2.imprint","IMPRINT",FACE,{"disambiguationData":[TD([[makeQuery(id+"F2.imprint","IMPRINT",EDGE,{"derivedFrom":sQuery(id+"F2.wireOp",EDGE,"E51")}),-1.0]])]});
            extrude(context, id + "F19", {"entities" : qUnion([Q0]), "operationType" : NewBodyOperationType.ADD, "depth" : 5.22 * mm, "offsetDistance" : 25.4 * mm});
        }
        {
            var Q0;
            Q0=makeQuery(id+"F2.imprint","IMPRINT",FACE,{"disambiguationData":[TD([[makeQuery(id+"F2.imprint","IMPRINT",EDGE,{"derivedFrom":sQuery(id+"F2.wireOp",EDGE,"E39")}),-1.0]])]});
            extrude(context, id + "F20", {"entities" : qUnion([Q0]), "operationType" : NewBodyOperationType.ADD, "depth" : 4.86 * mm, "offsetDistance" : 25.4 * mm});
        }
        {
            var Q0;
            {var subQ5=sQuery(id+"F2.wireOp",EDGE,"E606");Q0=makeQuery(id+"F2.imprint","IMPRINT",FACE,{"disambiguationData":[TD([[makeQuery(id+"F2.imprint","IMPRINT",EDGE,{"derivedFrom":subQ5}),-1.0]])]});}
            extrude(context, id + "F21", {"entities" : qUnion([Q0]), "operationType" : NewBodyOperationType.ADD, "depth" : 4.76 * mm, "offsetDistance" : 25.4 * mm});
        }
        {
            var Q0;
            Q0=makeQuery(id+"F2.imprint","IMPRINT",FACE,{"disambiguationData":[TD([[makeQuery(id+"F2.imprint","IMPRINT",EDGE,{"derivedFrom":sQuery(id+"F2.wireOp",EDGE,"E40")}),1.0]])]});
            extrude(context, id + "F22", {"entities" : qUnion([Q0]), "operationType" : NewBodyOperationType.ADD, "depth" : 4.61 * mm, "offsetDistance" : 25.4 * mm});
        }
        {
            var Q0;
            {var subQ1=sQuery(id+"F2.wireOp",EDGE,"E261");Q0=makeQuery(id+"F2.imprint","IMPRINT",FACE,{"disambiguationData":[TD([[makeQuery(id+"F2.imprint","IMPRINT",EDGE,{"derivedFrom":subQ1}),-1.0]])]});}
            extrude(context, id + "F23", {"entities" : qUnion([Q0]), "operationType" : NewBodyOperationType.ADD, "depth" : 4.36 * mm, "offsetDistance" : 25.4 * mm});
        }
        {
            var Q0;
            {var subQ0=sQuery(id+"F2.wireOp",EDGE,"E307");Q0=makeQuery(id+"F2.imprint","IMPRINT",FACE,{"disambiguationData":[TD([[makeQuery(id+"F2.imprint","IMPRINT",EDGE,{"derivedFrom":subQ0}),-1.0]])]});}
            extrude(context, id + "F24", {"entities" : qUnion([Q0]), "operationType" : NewBodyOperationType.ADD, "depth" : 3.88 * mm, "offsetDistance" : 25.4 * mm});
        }
        {
            var Q0;
            Q0=makeQuery(id+"F2.imprint","IMPRINT",FACE,{"disambiguationData":[TD([[makeQuery(id+"F2.imprint","IMPRINT",EDGE,{"derivedFrom":sQuery(id+"F2.wireOp",EDGE,"E1076")}),-1.0]])]});
            extrude(context, id + "F25", {"entities" : qUnion([Q0]), "operationType" : NewBodyOperationType.ADD, "depth" : 3.84 * mm, "offsetDistance" : 25.4 * mm});
        }
        {
            var Q0;
            Q0=makeQuery(id+"F2.imprint","IMPRINT",FACE,{"disambiguationData":[TD([[makeQuery(id+"F2.imprint","IMPRINT",EDGE,{"derivedFrom":sQuery(id+"F2.wireOp",EDGE,"E54")}),-1.0]])]});
            extrude(context, id + "F26", {"entities" : qUnion([Q0]), "operationType" : NewBodyOperationType.ADD, "depth" : 3.72 * mm, "offsetDistance" : 25.4 * mm});
        }
        {
            var Q0;
            Q0=makeQuery(id+"F2.imprint","IMPRINT",FACE,{"disambiguationData":[TD([[makeQuery(id+"F2.imprint","IMPRINT",EDGE,{"derivedFrom":sQuery(id+"F2.wireOp",EDGE,"E51")}),1.0]])]});
            extrude(context, id + "F27", {"entities" : qUnion([Q0]), "operationType" : NewBodyOperationType.ADD, "depth" : 3.53 * mm, "offsetDistance" : 25.4 * mm});
        }
        {
            var Q0;
            {var subQ2=sQuery(id+"F2.wireOp",EDGE,"E122");Q0=makeQuery(id+"F2.imprint","IMPRINT",FACE,{"disambiguationData":[TD([[makeQuery(id+"F2.imprint","IMPRINT",EDGE,{"derivedFrom":subQ2}),1.0]])]});}
            extrude(context, id + "F28", {"entities" : qUnion([Q0]), "operationType" : NewBodyOperationType.ADD, "depth" : 3.16 * mm, "offsetDistance" : 25.4 * mm});
        }
        {
            var Q0;
            Q0=makeQuery(id+"F2.imprint","IMPRINT",FACE,{"disambiguationData":[TD([[makeQuery(id+"F2.imprint","IMPRINT",EDGE,{"derivedFrom":sQuery(id+"F2.wireOp",EDGE,"E24")}),-1.0]])]});
            extrude(context, id + "F29", {"entities" : qUnion([Q0]), "operationType" : NewBodyOperationType.ADD, "depth" : 3.1 * mm, "offsetDistance" : 25.4 * mm});
        }
        {
            var Q0;
            Q0=makeQuery(id+"F2.imprint","IMPRINT",FACE,{"disambiguationData":[TD([[makeQuery(id+"F2.imprint","IMPRINT",EDGE,{"derivedFrom":sQuery(id+"F2.wireOp",EDGE,"E197")}),-1.0]])]});
            extrude(context, id + "F30", {"entities" : qUnion([Q0]), "operationType" : NewBodyOperationType.ADD, "depth" : 2.9 * mm, "offsetDistance" : 25.4 * mm});
        }
        {
            var Q0;
            Q0=makeQuery(id+"F2.imprint","IMPRINT",FACE,{"disambiguationData":[TD([[makeQuery(id+"F2.imprint","IMPRINT",EDGE,{"derivedFrom":sQuery(id+"F2.wireOp",EDGE,"E39")}),1.0]])]});
            extrude(context, id + "F31", {"entities" : qUnion([Q0]), "operationType" : NewBodyOperationType.ADD, "depth" : 2.48 * mm, "offsetDistance" : 25.4 * mm});
        }
        {
            var Q0;
            {var subQ0=sQuery(id+"F2.wireOp",EDGE,"E308");Q0=makeQuery(id+"F2.imprint","IMPRINT",FACE,{"disambiguationData":[TD([[makeQuery(id+"F2.imprint","IMPRINT",EDGE,{"derivedFrom":subQ0}),-1.0]])]});}
            extrude(context, id + "F32", {"entities" : qUnion([Q0]), "operationType" : NewBodyOperationType.ADD, "depth" : 2.4 * mm, "offsetDistance" : 25.4 * mm});
        }
        {
            var Q0;
            Q0=makeQuery(id+"F2.imprint","IMPRINT",FACE,{"disambiguationData":[TD([[makeQuery(id+"F2.imprint","IMPRINT",EDGE,{"derivedFrom":sQuery(id+"F2.wireOp",EDGE,"E47")}),-1.0]])]});
            extrude(context, id + "F33", {"entities" : qUnion([Q0]), "operationType" : NewBodyOperationType.ADD, "depth" : 2.38 * mm, "offsetDistance" : 25.4 * mm});
        }
        {
            var Q0;
            Q0=makeQuery(id+"F2.imprint","IMPRINT",FACE,{"disambiguationData":[TD([[makeQuery(id+"F2.imprint","IMPRINT",EDGE,{"derivedFrom":sQuery(id+"F2.wireOp",EDGE,"E11")}),-1.0]])]});
            extrude(context, id + "F34", {"entities" : qUnion([Q0]), "operationType" : NewBodyOperationType.ADD, "depth" : 2.33 * mm, "offsetDistance" : 25.4 * mm});
        }
        {
            var Q0;
            Q0=makeQuery(id+"F2.imprint","IMPRINT",FACE,{"disambiguationData":[TD([[makeQuery(id+"F2.imprint","IMPRINT",EDGE,{"derivedFrom":sQuery(id+"F2.wireOp",EDGE,"E37")}),-1.0]])]});
            extrude(context, id + "F35", {"entities" : qUnion([Q0]), "operationType" : NewBodyOperationType.ADD, "depth" : 2.33 * mm, "offsetDistance" : 25.4 * mm});
        }
        {
            var Q0;
            {var subQ0=sQuery(id+"F2.wireOp",EDGE,"E16");Q0=makeQuery(id+"F2.imprint","IMPRINT",FACE,{"disambiguationData":[TD([[makeQuery(id+"F2.imprint","IMPRINT",EDGE,{"derivedFrom":subQ0}),1.0]])]});}
            extrude(context, id + "F36", {"entities" : qUnion([Q0]), "operationType" : NewBodyOperationType.ADD, "depth" : 2.24 * mm, "offsetDistance" : 25.4 * mm});
        }
        {
            var Q0;
            Q0=makeQuery(id+"F2.imprint","IMPRINT",FACE,{"disambiguationData":[TD([[makeQuery(id+"F2.imprint","IMPRINT",EDGE,{"derivedFrom":sQuery(id+"F2.wireOp",EDGE,"E12")}),1.0]])]});
            extrude(context, id + "F37", {"entities" : qUnion([Q0]), "operationType" : NewBodyOperationType.ADD, "depth" : 1.5 * mm, "offsetDistance" : 25.4 * mm});
        }
        {
            var Q0;
            Q0=makeQuery(id+"F2.imprint","IMPRINT",FACE,{"disambiguationData":[TD([[makeQuery(id+"F2.imprint","IMPRINT",EDGE,{"derivedFrom":sQuery(id+"F2.wireOp",EDGE,"E711")}),-1.0]])]});
            extrude(context, id + "F38", {"entities" : qUnion([Q0]), "operationType" : NewBodyOperationType.ADD, "depth" : 1.49 * mm, "offsetDistance" : 25.4 * mm});
        }
        {
            var Q0;
            {var subQ2=sQuery(id+"F2.wireOp",EDGE,"E13");Q0=makeQuery(id+"F2.imprint","IMPRINT",FACE,{"disambiguationData":[TD([[makeQuery(id+"F2.imprint","IMPRINT",EDGE,{"derivedFrom":subQ2}),1.0]])]});}
            extrude(context, id + "F39", {"entities" : qUnion([Q0]), "operationType" : NewBodyOperationType.ADD, "depth" : 1.3 * mm, "offsetDistance" : 25.4 * mm});
        }
        {
            var Q0;
            Q0=makeQuery(id+"F2.imprint","IMPRINT",FACE,{"disambiguationData":[TD([[makeQuery(id+"F2.imprint","IMPRINT",EDGE,{"derivedFrom":sQuery(id+"F2.wireOp",EDGE,"E1431")}),-1.0]])]});
            var Q1;
            Q1=makeQuery(id+"F2.imprint","IMPRINT",FACE,{"disambiguationData":[TD([[makeQuery(id+"F2.imprint","IMPRINT",EDGE,{"derivedFrom":sQuery(id+"F2.wireOp",EDGE,"E1439")}),1.0]])]});
            var Q2;
            Q2=makeQuery(id+"F2.imprint","IMPRINT",FACE,{"disambiguationData":[TD([[makeQuery(id+"F2.imprint","IMPRINT",EDGE,{"derivedFrom":sQuery(id+"F2.wireOp",EDGE,"E1408")}),1.0]])]});
            var Q3;
            Q3=makeQuery(id+"F2.imprint","IMPRINT",FACE,{"disambiguationData":[TD([[makeQuery(id+"F2.imprint","IMPRINT",EDGE,{"derivedFrom":sQuery(id+"F2.wireOp",EDGE,"E1401")}),-1.0]])]});
            var Q4;
            Q4=makeQuery(id+"F2.imprint","IMPRINT",FACE,{"disambiguationData":[TD([[makeQuery(id+"F2.imprint","IMPRINT",EDGE,{"derivedFrom":sQuery(id+"F2.wireOp",EDGE,"E1417")}),1.0]])]});
            var Q5;
            Q5=makeQuery(id+"F2.imprint","IMPRINT",FACE,{"disambiguationData":[TD([[makeQuery(id+"F2.imprint","IMPRINT",EDGE,{"derivedFrom":sQuery(id+"F2.wireOp",EDGE,"E1426")}),-1.0]])]});
            var Q6;
            Q6=makeQuery(id+"F2.imprint","IMPRINT",FACE,{"disambiguationData":[TD([[makeQuery(id+"F2.imprint","IMPRINT",EDGE,{"derivedFrom":sQuery(id+"F2.wireOp",EDGE,"E1396")}),-1.0]])]});
            extrude(context, id + "F40", {"entities" : qUnion([Q0, Q1, Q2, Q3, Q4, Q5, Q6]), "operationType" : NewBodyOperationType.ADD, "depth" : 1.13 * mm, "offsetDistance" : 25.4 * mm});
        }
        {
            var Q0;
            Q0=makeQuery(id+"F2.imprint","IMPRINT",FACE,{"disambiguationData":[TD([[makeQuery(id+"F2.imprint","IMPRINT",EDGE,{"derivedFrom":sQuery(id+"F2.wireOp",EDGE,"E854")}),-1.0]])]});
            extrude(context, id + "F41", {"entities" : qUnion([Q0]), "operationType" : NewBodyOperationType.ADD, "depth" : 1.07 * mm, "offsetDistance" : 25.4 * mm});
        }
        {
            var Q0;
            {var subQ1=sQuery(id+"F2.wireOp",EDGE,"E621");Q0=makeQuery(id+"F2.imprint","IMPRINT",FACE,{"disambiguationData":[TD([[makeQuery(id+"F2.imprint","IMPRINT",EDGE,{"derivedFrom":subQ1}),1.0]])]});}
            extrude(context, id + "F42", {"entities" : qUnion([Q0]), "operationType" : NewBodyOperationType.ADD, "depth" : 1.06 * mm, "offsetDistance" : 25.4 * mm});
        }
        {
            var Q0;
            Q0=makeQuery(id+"F2.imprint","IMPRINT",FACE,{"disambiguationData":[TD([[makeQuery(id+"F2.imprint","IMPRINT",EDGE,{"derivedFrom":sQuery(id+"F2.wireOp",EDGE,"E608")}),-1.0]])]});
            extrude(context, id + "F43", {"entities" : qUnion([Q0]), "operationType" : NewBodyOperationType.ADD, "depth" : 0.84 * mm, "offsetDistance" : 25.4 * mm});
        }
        {
            var Q0;
            {var subQ5=sQuery(id+"F2.wireOp",EDGE,"E21");Q0=makeQuery(id+"F2.imprint","IMPRINT",FACE,{"disambiguationData":[TD([[makeQuery(id+"F2.imprint","IMPRINT",EDGE,{"derivedFrom":subQ5}),-1.0]])]});}
            extrude(context, id + "F44", {"entities" : qUnion([Q0]), "operationType" : NewBodyOperationType.ADD, "depth" : 0.82 * mm, "offsetDistance" : 25.4 * mm});
        }
        {
            var Q0;
            {var subQ3=sQuery(id+"F2.wireOp",EDGE,"E606");Q0=makeQuery(id+"F2.imprint","IMPRINT",FACE,{"disambiguationData":[TD([[makeQuery(id+"F2.imprint","IMPRINT",EDGE,{"derivedFrom":subQ3}),1.0]])]});}
            extrude(context, id + "F45", {"entities" : qUnion([Q0]), "operationType" : NewBodyOperationType.ADD, "depth" : 0.74 * mm, "offsetDistance" : 25.4 * mm});
        }
        {
            var Q0;
            Q0=makeQuery(id+"F2.imprint","IMPRINT",FACE,{"disambiguationData":[TD([[makeQuery(id+"F2.imprint","IMPRINT",EDGE,{"derivedFrom":sQuery(id+"F2.wireOp",EDGE,"E36")}),1.0]])]});
            extrude(context, id + "F46", {"entities" : qUnion([Q0]), "operationType" : NewBodyOperationType.ADD, "depth" : 0.68 * mm, "offsetDistance" : 25.4 * mm});
        }
        {
            var Q0;
            Q0=makeQuery(id+"F2.imprint","IMPRINT",FACE,{"disambiguationData":[TD([[makeQuery(id+"F2.imprint","IMPRINT",EDGE,{"derivedFrom":sQuery(id+"F2.wireOp",EDGE,"E1179")}),1.0]])]});
            extrude(context, id + "F47", {"entities" : qUnion([Q0]), "operationType" : NewBodyOperationType.ADD, "depth" : 0.6 * mm, "offsetDistance" : 25.4 * mm});
        }
        {
            var Q0;
            {var subQ4=sQuery(id+"F2.wireOp",EDGE,"E260");Q0=makeQuery(id+"F2.imprint","IMPRINT",FACE,{"disambiguationData":[TD([[makeQuery(id+"F2.imprint","IMPRINT",EDGE,{"derivedFrom":subQ4}),1.0]])]});}
            extrude(context, id + "F48", {"entities" : qUnion([Q0]), "operationType" : NewBodyOperationType.ADD, "depth" : 0.58 * mm, "offsetDistance" : 25.4 * mm});
        }
        {
            var Q0;
            {var subQ1=sQuery(id+"F2.wireOp",EDGE,"E202");Q0=makeQuery(id+"F2.imprint","IMPRINT",FACE,{"disambiguationData":[TD([[makeQuery(id+"F2.imprint","IMPRINT",EDGE,{"derivedFrom":subQ1}),-1.0]])]});}
            extrude(context, id + "F49", {"entities" : qUnion([Q0]), "operationType" : NewBodyOperationType.ADD, "depth" : 0.5 * mm, "offsetDistance" : 25.4 * mm});
        }
        {
            var Q0;
            {var subQ3=sQuery(id+"F2.wireOp",EDGE,"E14");Q0=makeQuery(id+"F2.imprint","IMPRINT",FACE,{"disambiguationData":[TD([[makeQuery(id+"F2.imprint","IMPRINT",EDGE,{"derivedFrom":subQ3}),1.0]])]});}
            extrude(context, id + "F50", {"entities" : qUnion([Q0]), "operationType" : NewBodyOperationType.ADD, "depth" : 0.47 * mm, "offsetDistance" : 25.4 * mm});
        }
        {
            var Q0;
            Q0=makeQuery(id+"F2.imprint","IMPRINT",FACE,{"disambiguationData":[TD([[makeQuery(id+"F2.imprint","IMPRINT",EDGE,{"derivedFrom":sQuery(id+"F2.wireOp",EDGE,"E22")}),1.0]])]});
            extrude(context, id + "F51", {"entities" : qUnion([Q0]), "operationType" : NewBodyOperationType.ADD, "depth" : 1.68 * mm, "offsetDistance" : 25.4 * mm});
        }
        {
            var Q0;
            {var subQ0=sQuery(id+"F2.wireOp",EDGE,"E30");Q0=makeQuery(id+"F2.imprint","IMPRINT",FACE,{"disambiguationData":[TD([[makeQuery(id+"F2.imprint","IMPRINT",EDGE,{"derivedFrom":subQ0}),1.0]])]});}
            extrude(context, id + "F52", {"entities" : qUnion([Q0]), "operationType" : NewBodyOperationType.ADD, "depth" : 5.33 * mm, "offsetDistance" : 25.4 * mm});
        }
        {
            var Q0;
            Q0=makeQuery(id+"F4.opExtrude","CAP_FACE",FACE,{"disambiguationData":[OSD([sQuery(id+"F2.wireOp",EDGE,"E17"),sQuery(id+"F2.wireOp",EDGE,"E18"),sQuery(id+"F2.wireOp",EDGE,"E19"),sQuery(id+"F2.wireOp",EDGE,"E64"),sQuery(id+"F2.wireOp",EDGE,"E66"),sQuery(id+"F2.wireOp",EDGE,"E67"),sQuery(id+"F2.wireOp",EDGE,"E68"),sQuery(id+"F2.wireOp",EDGE,"E69"),sQuery(id+"F2.wireOp",EDGE,"E70"),sQuery(id+"F2.wireOp",EDGE,"E71"),sQuery(id+"F2.wireOp",EDGE,"E72"),sQuery(id+"F2.wireOp",EDGE,"E73"),sQuery(id+"F2.wireOp",EDGE,"E74"),sQuery(id+"F2.wireOp",EDGE,"E75"),sQuery(id+"F2.wireOp",EDGE,"E76"),sQuery(id+"F2.wireOp",EDGE,"E77"),sQuery(id+"F2.wireOp",EDGE,"E78"),sQuery(id+"F2.wireOp",EDGE,"E79"),sQuery(id+"F2.wireOp",EDGE,"E80"),sQuery(id+"F2.wireOp",EDGE,"E81"),sQuery(id+"F2.wireOp",EDGE,"E82"),sQuery(id+"F2.wireOp",EDGE,"E83"),sQuery(id+"F2.wireOp",EDGE,"E84"),sQuery(id+"F2.wireOp",EDGE,"E85"),sQuery(id+"F2.wireOp",EDGE,"E86"),sQuery(id+"F2.wireOp",EDGE,"E87"),sQuery(id+"F2.wireOp",EDGE,"E88"),sQuery(id+"F2.wireOp",EDGE,"E89"),sQuery(id+"F2.wireOp",EDGE,"E90"),sQuery(id+"F2.wireOp",EDGE,"E91"),sQuery(id+"F2.wireOp",EDGE,"E92"),sQuery(id+"F2.wireOp",EDGE,"E93"),sQuery(id+"F2.wireOp",EDGE,"E94"),sQuery(id+"F2.wireOp",EDGE,"E95"),sQuery(id+"F2.wireOp",EDGE,"E96"),sQuery(id+"F2.wireOp",EDGE,"E97"),sQuery(id+"F2.wireOp",EDGE,"E98"),sQuery(id+"F2.wireOp",EDGE,"E99"),sQuery(id+"F2.wireOp",EDGE,"E100"),sQuery(id+"F2.wireOp",EDGE,"E101"),sQuery(id+"F2.wireOp",EDGE,"E102"),sQuery(id+"F2.wireOp",EDGE,"E103"),sQuery(id+"F2.wireOp",EDGE,"E104"),sQuery(id+"F2.wireOp",EDGE,"E105"),sQuery(id+"F2.wireOp",EDGE,"E106"),sQuery(id+"F2.wireOp",EDGE,"E107"),sQuery(id+"F2.wireOp",EDGE,"E108"),sQuery(id+"F2.wireOp",EDGE,"E109"),sQuery(id+"F2.wireOp",EDGE,"E110"),sQuery(id+"F2.wireOp",EDGE,"E111"),sQuery(id+"F2.wireOp",EDGE,"E112"),sQuery(id+"F2.wireOp",EDGE,"E113"),sQuery(id+"F2.wireOp",EDGE,"E114"),sQuery(id+"F2.wireOp",EDGE,"E115"),sQuery(id+"F2.wireOp",EDGE,"E116"),sQuery(id+"F2.wireOp",EDGE,"E117"),sQuery(id+"F2.wireOp",EDGE,"E118"),sQuery(id+"F2.wireOp",EDGE,"E119"),sQuery(id+"F2.wireOp",EDGE,"E120"),sQuery(id+"F2.wireOp",EDGE,"E121")])],"isStart":false});
            var sketch = newSketch(context, id + "F53", { "sketchPlane" : qUnion([Q0])});
            skText(sketch, "E1472", { "text": "CA", "fontName": "OpenSans-Bold.ttf"});
            const initialGuessF53  = {"E1472": [-0.06536, 0.00244, 1, 0, 0.00394]};
            skSetInitialGuess(sketch, initialGuessF53);
            skSolve(sketch);
        }
        {
            var Q0;
            Q0=makeQuery(id+"F53.imprint","IMPRINT",FACE,{"disambiguationData":[TD([[makeQuery(id+"F53.imprint","IMPRINT",EDGE,{"derivedFrom":sQuery(id+"F53.wireOp",EDGE,"E1472.sketch_text.stroke-15")}),-1.0]])]});
            var Q1;
            Q1=makeQuery(id+"F53.imprint","IMPRINT",FACE,{"disambiguationData":[TD([[makeQuery(id+"F53.imprint","IMPRINT",EDGE,{"derivedFrom":sQuery(id+"F53.wireOp",EDGE,"E1472.sketch_text.stroke-0")}),-1.0]])]});
            extrude(context, id + "F54", {"entities" : qUnion([Q0, Q1]), "operationType" : NewBodyOperationType.REMOVE, "oppositeDirection" : true, "depth" : 1.59 * mm, "offsetDistance" : 25.4 * mm});
        }
        {
            var Q0;
            Q0=makeQuery(id+"F28.opExtrude","CAP_FACE",FACE,{"disambiguationData":[OSD([sQuery(id+"F2.wireOp",EDGE,"E17"),sQuery(id+"F2.wireOp",EDGE,"E122"),sQuery(id+"F2.wireOp",EDGE,"E123"),sQuery(id+"F2.wireOp",EDGE,"E124"),sQuery(id+"F2.wireOp",EDGE,"E125"),sQuery(id+"F2.wireOp",EDGE,"E126"),sQuery(id+"F2.wireOp",EDGE,"E127"),sQuery(id+"F2.wireOp",EDGE,"E128"),sQuery(id+"F2.wireOp",EDGE,"E129"),sQuery(id+"F2.wireOp",EDGE,"E130"),sQuery(id+"F2.wireOp",EDGE,"E131"),sQuery(id+"F2.wireOp",EDGE,"E132"),sQuery(id+"F2.wireOp",EDGE,"E133"),sQuery(id+"F2.wireOp",EDGE,"E134"),sQuery(id+"F2.wireOp",EDGE,"E135"),sQuery(id+"F2.wireOp",EDGE,"E136"),sQuery(id+"F2.wireOp",EDGE,"E137"),sQuery(id+"F2.wireOp",EDGE,"E138"),sQuery(id+"F2.wireOp",EDGE,"E139"),sQuery(id+"F2.wireOp",EDGE,"E166"),sQuery(id+"F2.wireOp",EDGE,"E167"),sQuery(id+"F2.wireOp",EDGE,"E168"),sQuery(id+"F2.wireOp",EDGE,"E169"),sQuery(id+"F2.wireOp",EDGE,"E170"),sQuery(id+"F2.wireOp",EDGE,"E210"),sQuery(id+"F2.wireOp",EDGE,"E211"),sQuery(id+"F2.wireOp",EDGE,"E212"),sQuery(id+"F2.wireOp",EDGE,"E213"),sQuery(id+"F2.wireOp",EDGE,"E214"),sQuery(id+"F2.wireOp",EDGE,"E215")])],"isStart":false});
            var sketch = newSketch(context, id + "F55", { "sketchPlane" : qUnion([Q0])});
            skText(sketch, "E1473", { "text": "OR", "fontName": "OpenSans-Bold.ttf"});
            const initialGuessF55  = {"E1473": [-0.06233, 0.02864, 1, 0, 0.0036]};
            skSetInitialGuess(sketch, initialGuessF55);
            skSolve(sketch);
        }
        {
            var Q0;
            Q0=makeQuery(id+"F55.imprint","IMPRINT",FACE,{"disambiguationData":[TD([[makeQuery(id+"F55.imprint","IMPRINT",EDGE,{"derivedFrom":sQuery(id+"F55.wireOp",EDGE,"E1473.sketch_text.stroke-14")}),-1.0]])]});
            var Q1;
            Q1=makeQuery(id+"F55.imprint","IMPRINT",FACE,{"disambiguationData":[TD([[makeQuery(id+"F55.imprint","IMPRINT",EDGE,{"derivedFrom":sQuery(id+"F55.wireOp",EDGE,"E1473.sketch_text.stroke-0")}),-1.0]])]});
            extrude(context, id + "F56", {"entities" : qUnion([Q0, Q1]), "operationType" : NewBodyOperationType.REMOVE, "oppositeDirection" : true, "depth" : 1.59 * mm, "offsetDistance" : 25.4 * mm});
        }
        {
            var Q0;
            Q0=makeQuery(id+"F16.opExtrude","CAP_FACE",FACE,{"disambiguationData":[OSD([sQuery(id+"F2.wireOp",EDGE,"E34"),sQuery(id+"F2.wireOp",EDGE,"E49"),sQuery(id+"F2.wireOp",EDGE,"E126"),sQuery(id+"F2.wireOp",EDGE,"E127"),sQuery(id+"F2.wireOp",EDGE,"E128"),sQuery(id+"F2.wireOp",EDGE,"E129"),sQuery(id+"F2.wireOp",EDGE,"E130"),sQuery(id+"F2.wireOp",EDGE,"E131"),sQuery(id+"F2.wireOp",EDGE,"E132"),sQuery(id+"F2.wireOp",EDGE,"E133"),sQuery(id+"F2.wireOp",EDGE,"E134"),sQuery(id+"F2.wireOp",EDGE,"E135"),sQuery(id+"F2.wireOp",EDGE,"E136"),sQuery(id+"F2.wireOp",EDGE,"E137"),sQuery(id+"F2.wireOp",EDGE,"E138"),sQuery(id+"F2.wireOp",EDGE,"E139"),sQuery(id+"F2.wireOp",EDGE,"E140"),sQuery(id+"F2.wireOp",EDGE,"E141"),sQuery(id+"F2.wireOp",EDGE,"E142"),sQuery(id+"F2.wireOp",EDGE,"E143"),sQuery(id+"F2.wireOp",EDGE,"E144"),sQuery(id+"F2.wireOp",EDGE,"E145"),sQuery(id+"F2.wireOp",EDGE,"E146"),sQuery(id+"F2.wireOp",EDGE,"E147"),sQuery(id+"F2.wireOp",EDGE,"E148"),sQuery(id+"F2.wireOp",EDGE,"E149"),sQuery(id+"F2.wireOp",EDGE,"E150"),sQuery(id+"F2.wireOp",EDGE,"E151"),sQuery(id+"F2.wireOp",EDGE,"E152"),sQuery(id+"F2.wireOp",EDGE,"E153"),sQuery(id+"F2.wireOp",EDGE,"E154"),sQuery(id+"F2.wireOp",EDGE,"E155"),sQuery(id+"F2.wireOp",EDGE,"E156"),sQuery(id+"F2.wireOp",EDGE,"E157"),sQuery(id+"F2.wireOp",EDGE,"E158"),sQuery(id+"F2.wireOp",EDGE,"E159"),sQuery(id+"F2.wireOp",EDGE,"E160"),sQuery(id+"F2.wireOp",EDGE,"E161"),sQuery(id+"F2.wireOp",EDGE,"E162"),sQuery(id+"F2.wireOp",EDGE,"E163"),sQuery(id+"F2.wireOp",EDGE,"E164"),sQuery(id+"F2.wireOp",EDGE,"E165")])],"isStart":false});
            var sketch = newSketch(context, id + "F57", { "sketchPlane" : qUnion([Q0])});
            skText(sketch, "E1474", { "text": "WA", "fontName": "OpenSans-Bold.ttf"});
            const initialGuessF57  = {"E1474": [-0.05847, 0.03968, 1, 0, 0.00319]};
            skSetInitialGuess(sketch, initialGuessF57);
            skSolve(sketch);
        }
        {
            var Q0;
            Q0=makeQuery(id+"F57.imprint","IMPRINT",FACE,{"disambiguationData":[TD([[makeQuery(id+"F57.imprint","IMPRINT",EDGE,{"derivedFrom":sQuery(id+"F57.wireOp",EDGE,"E1474.sketch_text.stroke-24")}),-1.0]])]});
            var Q1;
            Q1=makeQuery(id+"F57.imprint","IMPRINT",FACE,{"disambiguationData":[TD([[makeQuery(id+"F57.imprint","IMPRINT",EDGE,{"derivedFrom":sQuery(id+"F57.wireOp",EDGE,"E1474.sketch_text.stroke-0")}),-1.0]])]});
            extrude(context, id + "F58", {"entities" : qUnion([Q0, Q1]), "operationType" : NewBodyOperationType.REMOVE, "oppositeDirection" : true, "depth" : 1.59 * mm, "offsetDistance" : 25.4 * mm});
        }
        {
            var Q0;
            Q0=makeQuery(id+"F47.opExtrude","CAP_FACE",FACE,{"disambiguationData":[OSD([sQuery(id+"F2.wireOp",EDGE,"E1179"),sQuery(id+"F2.wireOp",EDGE,"E1180"),sQuery(id+"F2.wireOp",EDGE,"E1181"),sQuery(id+"F2.wireOp",EDGE,"E1182"),sQuery(id+"F2.wireOp",EDGE,"E1183"),sQuery(id+"F2.wireOp",EDGE,"E1184"),sQuery(id+"F2.wireOp",EDGE,"E1185"),sQuery(id+"F2.wireOp",EDGE,"E1186"),sQuery(id+"F2.wireOp",EDGE,"E1187"),sQuery(id+"F2.wireOp",EDGE,"E1188"),sQuery(id+"F2.wireOp",EDGE,"E1189"),sQuery(id+"F2.wireOp",EDGE,"E1190"),sQuery(id+"F2.wireOp",EDGE,"E1191"),sQuery(id+"F2.wireOp",EDGE,"E1192"),sQuery(id+"F2.wireOp",EDGE,"E1193"),sQuery(id+"F2.wireOp",EDGE,"E1194"),sQuery(id+"F2.wireOp",EDGE,"E1195"),sQuery(id+"F2.wireOp",EDGE,"E1196"),sQuery(id+"F2.wireOp",EDGE,"E1197"),sQuery(id+"F2.wireOp",EDGE,"E1198"),sQuery(id+"F2.wireOp",EDGE,"E1199"),sQuery(id+"F2.wireOp",EDGE,"E1200"),sQuery(id+"F2.wireOp",EDGE,"E1201"),sQuery(id+"F2.wireOp",EDGE,"E1202"),sQuery(id+"F2.wireOp",EDGE,"E1203"),sQuery(id+"F2.wireOp",EDGE,"E1204"),sQuery(id+"F2.wireOp",EDGE,"E1205"),sQuery(id+"F2.wireOp",EDGE,"E1206"),sQuery(id+"F2.wireOp",EDGE,"E1207"),sQuery(id+"F2.wireOp",EDGE,"E1208"),sQuery(id+"F2.wireOp",EDGE,"E1209"),sQuery(id+"F2.wireOp",EDGE,"E1210"),sQuery(id+"F2.wireOp",EDGE,"E1211"),sQuery(id+"F2.wireOp",EDGE,"E1212"),sQuery(id+"F2.wireOp",EDGE,"E1213"),sQuery(id+"F2.wireOp",EDGE,"E1214"),sQuery(id+"F2.wireOp",EDGE,"E1215"),sQuery(id+"F2.wireOp",EDGE,"E1216"),sQuery(id+"F2.wireOp",EDGE,"E1217"),sQuery(id+"F2.wireOp",EDGE,"E1218"),sQuery(id+"F2.wireOp",EDGE,"E1219"),sQuery(id+"F2.wireOp",EDGE,"E1220"),sQuery(id+"F2.wireOp",EDGE,"E1221"),sQuery(id+"F2.wireOp",EDGE,"E1222"),sQuery(id+"F2.wireOp",EDGE,"E1223"),sQuery(id+"F2.wireOp",EDGE,"E1224"),sQuery(id+"F2.wireOp",EDGE,"E1225"),sQuery(id+"F2.wireOp",EDGE,"E1226"),sQuery(id+"F2.wireOp",EDGE,"E1227"),sQuery(id+"F2.wireOp",EDGE,"E1228"),sQuery(id+"F2.wireOp",EDGE,"E1229"),sQuery(id+"F2.wireOp",EDGE,"E1230"),sQuery(id+"F2.wireOp",EDGE,"E1231"),sQuery(id+"F2.wireOp",EDGE,"E1232"),sQuery(id+"F2.wireOp",EDGE,"E1233"),sQuery(id+"F2.wireOp",EDGE,"E1234"),sQuery(id+"F2.wireOp",EDGE,"E1235"),sQuery(id+"F2.wireOp",EDGE,"E1236"),sQuery(id+"F2.wireOp",EDGE,"E1237"),sQuery(id+"F2.wireOp",EDGE,"E1238"),sQuery(id+"F2.wireOp",EDGE,"E1239"),sQuery(id+"F2.wireOp",EDGE,"E1240"),sQuery(id+"F2.wireOp",EDGE,"E1241"),sQuery(id+"F2.wireOp",EDGE,"E1242"),sQuery(id+"F2.wireOp",EDGE,"E1243"),sQuery(id+"F2.wireOp",EDGE,"E1244"),sQuery(id+"F2.wireOp",EDGE,"E1245"),sQuery(id+"F2.wireOp",EDGE,"E1246"),sQuery(id+"F2.wireOp",EDGE,"E1247"),sQuery(id+"F2.wireOp",EDGE,"E1248"),sQuery(id+"F2.wireOp",EDGE,"E1249"),sQuery(id+"F2.wireOp",EDGE,"E1250"),sQuery(id+"F2.wireOp",EDGE,"E1251"),sQuery(id+"F2.wireOp",EDGE,"E1252"),sQuery(id+"F2.wireOp",EDGE,"E1253"),sQuery(id+"F2.wireOp",EDGE,"E1254"),sQuery(id+"F2.wireOp",EDGE,"E1255"),sQuery(id+"F2.wireOp",EDGE,"E1256"),sQuery(id+"F2.wireOp",EDGE,"E1257"),sQuery(id+"F2.wireOp",EDGE,"E1258"),sQuery(id+"F2.wireOp",EDGE,"E1259"),sQuery(id+"F2.wireOp",EDGE,"E1260"),sQuery(id+"F2.wireOp",EDGE,"E1261"),sQuery(id+"F2.wireOp",EDGE,"E1262"),sQuery(id+"F2.wireOp",EDGE,"E1263"),sQuery(id+"F2.wireOp",EDGE,"E1264"),sQuery(id+"F2.wireOp",EDGE,"E1265"),sQuery(id+"F2.wireOp",EDGE,"E1266"),sQuery(id+"F2.wireOp",EDGE,"E1267"),sQuery(id+"F2.wireOp",EDGE,"E1268"),sQuery(id+"F2.wireOp",EDGE,"E1269"),sQuery(id+"F2.wireOp",EDGE,"E1270"),sQuery(id+"F2.wireOp",EDGE,"E1271"),sQuery(id+"F2.wireOp",EDGE,"E1272"),sQuery(id+"F2.wireOp",EDGE,"E1273"),sQuery(id+"F2.wireOp",EDGE,"E1274"),sQuery(id+"F2.wireOp",EDGE,"E1275"),sQuery(id+"F2.wireOp",EDGE,"E1276"),sQuery(id+"F2.wireOp",EDGE,"E1277"),sQuery(id+"F2.wireOp",EDGE,"E1278"),sQuery(id+"F2.wireOp",EDGE,"E1279"),sQuery(id+"F2.wireOp",EDGE,"E1280"),sQuery(id+"F2.wireOp",EDGE,"E1281"),sQuery(id+"F2.wireOp",EDGE,"E1282"),sQuery(id+"F2.wireOp",EDGE,"E1283"),sQuery(id+"F2.wireOp",EDGE,"E1284"),sQuery(id+"F2.wireOp",EDGE,"E1285"),sQuery(id+"F2.wireOp",EDGE,"E1286"),sQuery(id+"F2.wireOp",EDGE,"E1287"),sQuery(id+"F2.wireOp",EDGE,"E1288"),sQuery(id+"F2.wireOp",EDGE,"E1289"),sQuery(id+"F2.wireOp",EDGE,"E1290"),sQuery(id+"F2.wireOp",EDGE,"E1291"),sQuery(id+"F2.wireOp",EDGE,"E1292"),sQuery(id+"F2.wireOp",EDGE,"E1293"),sQuery(id+"F2.wireOp",EDGE,"E1294"),sQuery(id+"F2.wireOp",EDGE,"E1295"),sQuery(id+"F2.wireOp",EDGE,"E1296"),sQuery(id+"F2.wireOp",EDGE,"E1297"),sQuery(id+"F2.wireOp",EDGE,"E1298"),sQuery(id+"F2.wireOp",EDGE,"E1299"),sQuery(id+"F2.wireOp",EDGE,"E1300"),sQuery(id+"F2.wireOp",EDGE,"E1301"),sQuery(id+"F2.wireOp",EDGE,"E1302"),sQuery(id+"F2.wireOp",EDGE,"E1303"),sQuery(id+"F2.wireOp",EDGE,"E1304"),sQuery(id+"F2.wireOp",EDGE,"E1305"),sQuery(id+"F2.wireOp",EDGE,"E1306"),sQuery(id+"F2.wireOp",EDGE,"E1307"),sQuery(id+"F2.wireOp",EDGE,"E1308"),sQuery(id+"F2.wireOp",EDGE,"E1309"),sQuery(id+"F2.wireOp",EDGE,"E1310"),sQuery(id+"F2.wireOp",EDGE,"E1311"),sQuery(id+"F2.wireOp",EDGE,"E1312"),sQuery(id+"F2.wireOp",EDGE,"E1313"),sQuery(id+"F2.wireOp",EDGE,"E1314"),sQuery(id+"F2.wireOp",EDGE,"E1315"),sQuery(id+"F2.wireOp",EDGE,"E1316"),sQuery(id+"F2.wireOp",EDGE,"E1317"),sQuery(id+"F2.wireOp",EDGE,"E1318"),sQuery(id+"F2.wireOp",EDGE,"E1319"),sQuery(id+"F2.wireOp",EDGE,"E1320"),sQuery(id+"F2.wireOp",EDGE,"E1321"),sQuery(id+"F2.wireOp",EDGE,"E1322"),sQuery(id+"F2.wireOp",EDGE,"E1323"),sQuery(id+"F2.wireOp",EDGE,"E1324"),sQuery(id+"F2.wireOp",EDGE,"E1325"),sQuery(id+"F2.wireOp",EDGE,"E1326"),sQuery(id+"F2.wireOp",EDGE,"E1327"),sQuery(id+"F2.wireOp",EDGE,"E1328"),sQuery(id+"F2.wireOp",EDGE,"E1329"),sQuery(id+"F2.wireOp",EDGE,"E1330"),sQuery(id+"F2.wireOp",EDGE,"E1331"),sQuery(id+"F2.wireOp",EDGE,"E1332"),sQuery(id+"F2.wireOp",EDGE,"E1333"),sQuery(id+"F2.wireOp",EDGE,"E1334"),sQuery(id+"F2.wireOp",EDGE,"E1335"),sQuery(id+"F2.wireOp",EDGE,"E1336"),sQuery(id+"F2.wireOp",EDGE,"E1337"),sQuery(id+"F2.wireOp",EDGE,"E1338"),sQuery(id+"F2.wireOp",EDGE,"E1339"),sQuery(id+"F2.wireOp",EDGE,"E1340"),sQuery(id+"F2.wireOp",EDGE,"E1341"),sQuery(id+"F2.wireOp",EDGE,"E1342"),sQuery(id+"F2.wireOp",EDGE,"E1343"),sQuery(id+"F2.wireOp",EDGE,"E1344"),sQuery(id+"F2.wireOp",EDGE,"E1345"),sQuery(id+"F2.wireOp",EDGE,"E1346"),sQuery(id+"F2.wireOp",EDGE,"E1347"),sQuery(id+"F2.wireOp",EDGE,"E1348"),sQuery(id+"F2.wireOp",EDGE,"E1349"),sQuery(id+"F2.wireOp",EDGE,"E1350"),sQuery(id+"F2.wireOp",EDGE,"E1351"),sQuery(id+"F2.wireOp",EDGE,"E1352"),sQuery(id+"F2.wireOp",EDGE,"E1353"),sQuery(id+"F2.wireOp",EDGE,"E1354"),sQuery(id+"F2.wireOp",EDGE,"E1355"),sQuery(id+"F2.wireOp",EDGE,"E1356"),sQuery(id+"F2.wireOp",EDGE,"E1357"),sQuery(id+"F2.wireOp",EDGE,"E1358"),sQuery(id+"F2.wireOp",EDGE,"E1359"),sQuery(id+"F2.wireOp",EDGE,"E1360"),sQuery(id+"F2.wireOp",EDGE,"E1361"),sQuery(id+"F2.wireOp",EDGE,"E1362"),sQuery(id+"F2.wireOp",EDGE,"E1363"),sQuery(id+"F2.wireOp",EDGE,"E1364"),sQuery(id+"F2.wireOp",EDGE,"E1365"),sQuery(id+"F2.wireOp",EDGE,"E1366"),sQuery(id+"F2.wireOp",EDGE,"E1367"),sQuery(id+"F2.wireOp",EDGE,"E1368"),sQuery(id+"F2.wireOp",EDGE,"E1369"),sQuery(id+"F2.wireOp",EDGE,"E1370"),sQuery(id+"F2.wireOp",EDGE,"E1371"),sQuery(id+"F2.wireOp",EDGE,"E1372"),sQuery(id+"F2.wireOp",EDGE,"E1373"),sQuery(id+"F2.wireOp",EDGE,"E1374"),sQuery(id+"F2.wireOp",EDGE,"E1375"),sQuery(id+"F2.wireOp",EDGE,"E1376"),sQuery(id+"F2.wireOp",EDGE,"E1377"),sQuery(id+"F2.wireOp",EDGE,"E1378"),sQuery(id+"F2.wireOp",EDGE,"E1379"),sQuery(id+"F2.wireOp",EDGE,"E1380"),sQuery(id+"F2.wireOp",EDGE,"E1381"),sQuery(id+"F2.wireOp",EDGE,"E1382"),sQuery(id+"F2.wireOp",EDGE,"E1383"),sQuery(id+"F2.wireOp",EDGE,"E1384"),sQuery(id+"F2.wireOp",EDGE,"E1385"),sQuery(id+"F2.wireOp",EDGE,"E1386"),sQuery(id+"F2.wireOp",EDGE,"E1387"),sQuery(id+"F2.wireOp",EDGE,"E1388"),sQuery(id+"F2.wireOp",EDGE,"E1389"),sQuery(id+"F2.wireOp",EDGE,"E1390"),sQuery(id+"F2.wireOp",EDGE,"E1391"),sQuery(id+"F2.wireOp",EDGE,"E1392"),sQuery(id+"F2.wireOp",EDGE,"E1393"),sQuery(id+"F2.wireOp",EDGE,"E1394"),sQuery(id+"F2.wireOp",EDGE,"E1395"),sQuery(id+"F2.wireOp",EDGE,"E1466")])],"isStart":false});
            var sketch = newSketch(context, id + "F59", { "sketchPlane" : qUnion([Q0])});
            skText(sketch, "E1475", { "text": "AK", "fontName": "OpenSans-Bold.ttf"});
            const initialGuessF59  = {"E1475": [-0.05846, -0.02919, 1, 0, 0.00387]};
            skSetInitialGuess(sketch, initialGuessF59);
            skSolve(sketch);
        }
        {
            var Q0;
            Q0=makeQuery(id+"F59.imprint","IMPRINT",FACE,{"disambiguationData":[TD([[makeQuery(id+"F59.imprint","IMPRINT",EDGE,{"derivedFrom":sQuery(id+"F59.wireOp",EDGE,"E1475.sketch_text.stroke-12")}),-1.0]])]});
            var Q1;
            Q1=makeQuery(id+"F59.imprint","IMPRINT",FACE,{"disambiguationData":[TD([[makeQuery(id+"F59.imprint","IMPRINT",EDGE,{"derivedFrom":sQuery(id+"F59.wireOp",EDGE,"E1475.sketch_text.stroke-0")}),-1.0]])]});
            extrude(context, id + "F60", {"entities" : qUnion([Q0, Q1]), "operationType" : NewBodyOperationType.REMOVE, "oppositeDirection" : true, "depth" : 1.59 * mm, "offsetDistance" : 25.4 * mm});
        }
        {
            var Q0;
            Q0=makeQuery(id+"F2.imprint","IMPRINT",FACE,{"disambiguationData":[TD([[makeQuery(id+"F2.imprint","IMPRINT",EDGE,{"derivedFrom":sQuery(id+"F2.wireOp",EDGE,"E1")}),1.0]])]});
            var sketch = newSketch(context, id + "F61", { "sketchPlane" : qUnion([Q0])});
            skText(sketch, "E1476", { "text": "HI", "fontName": "OpenSans-Bold.ttf"});
            const initialGuessF61  = {"E1476": [-0.03177, -0.04127, 1, 0, 0.00512]};
            skSetInitialGuess(sketch, initialGuessF61);
            skSolve(sketch);
        }
        {
            var Q0;
            Q0=makeQuery(id+"F61.imprint","IMPRINT",FACE,{"disambiguationData":[TD([[makeQuery(id+"F61.imprint","IMPRINT",EDGE,{"derivedFrom":sQuery(id+"F61.wireOp",EDGE,"E1476.sketch_text.stroke-0")}),-1.0]])]});
            var Q1;
            Q1=makeQuery(id+"F61.imprint","IMPRINT",FACE,{"disambiguationData":[TD([[makeQuery(id+"F61.imprint","IMPRINT",EDGE,{"derivedFrom":sQuery(id+"F61.wireOp",EDGE,"E1476.sketch_text.stroke-12")}),-1.0]])]});
            extrude(context, id + "F62", {"entities" : qUnion([Q0, Q1]), "operationType" : NewBodyOperationType.REMOVE, "oppositeDirection" : true, "depth" : 1.59 * mm, "offsetDistance" : 25.4 * mm});
        }
        {
            var Q0;
            Q0=makeQuery(id+"F5.opExtrude","CAP_FACE",FACE,{"disambiguationData":[OSD([sQuery(id+"F2.wireOp",EDGE,"E1"),sQuery(id+"F2.wireOp",EDGE,"E2"),sQuery(id+"F2.wireOp",EDGE,"E3"),sQuery(id+"F2.wireOp",EDGE,"E4"),sQuery(id+"F2.wireOp",EDGE,"E5"),sQuery(id+"F2.wireOp",EDGE,"E6"),sQuery(id+"F2.wireOp",EDGE,"E7"),sQuery(id+"F2.wireOp",EDGE,"E8"),sQuery(id+"F2.wireOp",EDGE,"E9"),sQuery(id+"F2.wireOp",EDGE,"E10"),sQuery(id+"F2.wireOp",EDGE,"E22"),sQuery(id+"F2.wireOp",EDGE,"E23"),sQuery(id+"F2.wireOp",EDGE,"E28"),sQuery(id+"F2.wireOp",EDGE,"E29"),sQuery(id+"F2.wireOp",EDGE,"E32"),sQuery(id+"F2.wireOp",EDGE,"E33"),sQuery(id+"F2.wireOp",EDGE,"E241"),sQuery(id+"F2.wireOp",EDGE,"E242"),sQuery(id+"F2.wireOp",EDGE,"E243"),sQuery(id+"F2.wireOp",EDGE,"E244"),sQuery(id+"F2.wireOp",EDGE,"E245"),sQuery(id+"F2.wireOp",EDGE,"E246"),sQuery(id+"F2.wireOp",EDGE,"E247"),sQuery(id+"F2.wireOp",EDGE,"E248"),sQuery(id+"F2.wireOp",EDGE,"E249"),sQuery(id+"F2.wireOp",EDGE,"E250"),sQuery(id+"F2.wireOp",EDGE,"E251"),sQuery(id+"F2.wireOp",EDGE,"E252"),sQuery(id+"F2.wireOp",EDGE,"E253"),sQuery(id+"F2.wireOp",EDGE,"E268"),sQuery(id+"F2.wireOp",EDGE,"E269"),sQuery(id+"F2.wireOp",EDGE,"E270"),sQuery(id+"F2.wireOp",EDGE,"E271"),sQuery(id+"F2.wireOp",EDGE,"E272"),sQuery(id+"F2.wireOp",EDGE,"E273"),sQuery(id+"F2.wireOp",EDGE,"E274"),sQuery(id+"F2.wireOp",EDGE,"E275"),sQuery(id+"F2.wireOp",EDGE,"E276"),sQuery(id+"F2.wireOp",EDGE,"E277"),sQuery(id+"F2.wireOp",EDGE,"E278"),sQuery(id+"F2.wireOp",EDGE,"E279"),sQuery(id+"F2.wireOp",EDGE,"E280"),sQuery(id+"F2.wireOp",EDGE,"E281"),sQuery(id+"F2.wireOp",EDGE,"E282"),sQuery(id+"F2.wireOp",EDGE,"E283"),sQuery(id+"F2.wireOp",EDGE,"E284"),sQuery(id+"F2.wireOp",EDGE,"E285"),sQuery(id+"F2.wireOp",EDGE,"E286"),sQuery(id+"F2.wireOp",EDGE,"E287"),sQuery(id+"F2.wireOp",EDGE,"E288"),sQuery(id+"F2.wireOp",EDGE,"E289"),sQuery(id+"F2.wireOp",EDGE,"E290"),sQuery(id+"F2.wireOp",EDGE,"E291"),sQuery(id+"F2.wireOp",EDGE,"E292"),sQuery(id+"F2.wireOp",EDGE,"E293"),sQuery(id+"F2.wireOp",EDGE,"E294"),sQuery(id+"F2.wireOp",EDGE,"E295"),sQuery(id+"F2.wireOp",EDGE,"E296"),sQuery(id+"F2.wireOp",EDGE,"E297"),sQuery(id+"F2.wireOp",EDGE,"E298"),sQuery(id+"F2.wireOp",EDGE,"E299"),sQuery(id+"F2.wireOp",EDGE,"E300"),sQuery(id+"F2.wireOp",EDGE,"E301"),sQuery(id+"F2.wireOp",EDGE,"E302"),sQuery(id+"F2.wireOp",EDGE,"E303"),sQuery(id+"F2.wireOp",EDGE,"E304"),sQuery(id+"F2.wireOp",EDGE,"E305"),sQuery(id+"F2.wireOp",EDGE,"E306"),sQuery(id+"F2.wireOp",EDGE,"E360"),sQuery(id+"F2.wireOp",EDGE,"E361"),sQuery(id+"F2.wireOp",EDGE,"E362"),sQuery(id+"F2.wireOp",EDGE,"E363"),sQuery(id+"F2.wireOp",EDGE,"E364"),sQuery(id+"F2.wireOp",EDGE,"E365"),sQuery(id+"F2.wireOp",EDGE,"E366"),sQuery(id+"F2.wireOp",EDGE,"E367"),sQuery(id+"F2.wireOp",EDGE,"E368"),sQuery(id+"F2.wireOp",EDGE,"E369"),sQuery(id+"F2.wireOp",EDGE,"E370"),sQuery(id+"F2.wireOp",EDGE,"E371"),sQuery(id+"F2.wireOp",EDGE,"E372"),sQuery(id+"F2.wireOp",EDGE,"E373"),sQuery(id+"F2.wireOp",EDGE,"E374"),sQuery(id+"F2.wireOp",EDGE,"E375"),sQuery(id+"F2.wireOp",EDGE,"E376"),sQuery(id+"F2.wireOp",EDGE,"E377"),sQuery(id+"F2.wireOp",EDGE,"E378"),sQuery(id+"F2.wireOp",EDGE,"E379"),sQuery(id+"F2.wireOp",EDGE,"E380"),sQuery(id+"F2.wireOp",EDGE,"E381"),sQuery(id+"F2.wireOp",EDGE,"E382"),sQuery(id+"F2.wireOp",EDGE,"E383"),sQuery(id+"F2.wireOp",EDGE,"E384"),sQuery(id+"F2.wireOp",EDGE,"E385"),sQuery(id+"F2.wireOp",EDGE,"E386"),sQuery(id+"F2.wireOp",EDGE,"E387"),sQuery(id+"F2.wireOp",EDGE,"E388"),sQuery(id+"F2.wireOp",EDGE,"E389"),sQuery(id+"F2.wireOp",EDGE,"E390"),sQuery(id+"F2.wireOp",EDGE,"E391"),sQuery(id+"F2.wireOp",EDGE,"E392"),sQuery(id+"F2.wireOp",EDGE,"E393"),sQuery(id+"F2.wireOp",EDGE,"E394")])],"isStart":false});
            var sketch = newSketch(context, id + "F63", { "sketchPlane" : qUnion([Q0])});
            skText(sketch, "E1477", { "text": "TX", "fontName": "OpenSans-Bold.ttf"});
            const initialGuessF63  = {"E1477": [-0.01055, -0.02209, 1, 0, 0.00419]};
            skSetInitialGuess(sketch, initialGuessF63);
            skSolve(sketch);
        }
        {
            var Q0;
            Q0=makeQuery(id+"F63.imprint","IMPRINT",FACE,{"disambiguationData":[TD([[makeQuery(id+"F63.imprint","IMPRINT",EDGE,{"derivedFrom":sQuery(id+"F63.wireOp",EDGE,"E1477.sketch_text.stroke-0")}),-1.0]])]});
            var Q1;
            Q1=makeQuery(id+"F63.imprint","IMPRINT",FACE,{"disambiguationData":[TD([[makeQuery(id+"F63.imprint","IMPRINT",EDGE,{"derivedFrom":sQuery(id+"F63.wireOp",EDGE,"E1477.sketch_text.stroke-8")}),-1.0]])]});
            extrude(context, id + "F64", {"entities" : qUnion([Q0, Q1]), "operationType" : NewBodyOperationType.REMOVE, "oppositeDirection" : true, "depth" : 1.59 * mm, "offsetDistance" : 25.4 * mm});
        }
        {
            var Q0;
            Q0=makeQuery(id+"F2.imprint","IMPRINT",FACE,{"disambiguationData":[TD([[makeQuery(id+"F2.imprint","IMPRINT",EDGE,{"derivedFrom":sQuery(id+"F2.wireOp",EDGE,"E1")}),1.0]])]});
            var sketch = newSketch(context, id + "F65", { "sketchPlane" : qUnion([Q0])});
            skText(sketch, "E1478", { "text": "THE", "fontName": "OpenSans-Regular.ttf"});
            skText(sketch, "E1479", { "text": "USA", "fontName": "OpenSans-Regular.ttf"});
            const initialGuessF65  = {"E1478": [-0.02264, 0.04386, 1, 0, 0.01037], "E1479": [0.00623, 0.04336, 1, 0, 0.0113]};
            skSetInitialGuess(sketch, initialGuessF65);
            skSolve(sketch);
        }
        {
            var Q0;
            Q0 = qSketchRegion(id + "F65", true);
            extrude(context, id + "F66", {"entities" : qUnion([Q0]), "operationType" : NewBodyOperationType.REMOVE, "oppositeDirection" : true, "depth" : 1.59 * mm, "offsetDistance" : 25.4 * mm});
        }
    });
